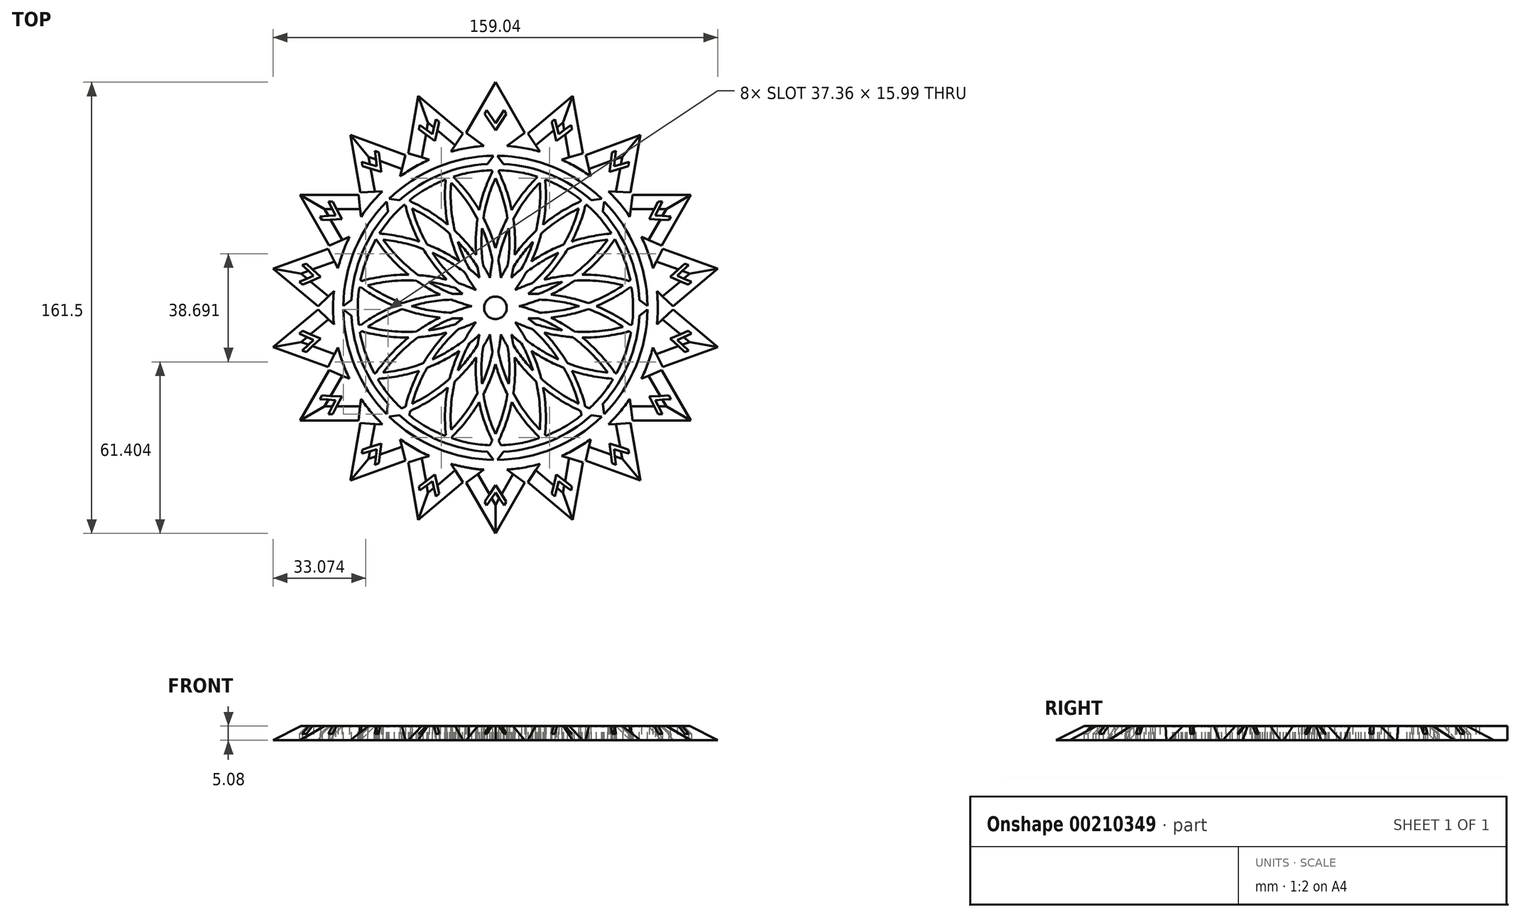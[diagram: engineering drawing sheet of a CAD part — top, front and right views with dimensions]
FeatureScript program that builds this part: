
annotation { "Feature Type Name" : "Feature", "Feature Type Description" : "" }
export const myFeature = defineFeature(function(context is Context, id is Id, definition is map)
    precondition{}
    {
        {
            var Q0;
            Q0=qCreatedBy(makeId("Top.planeOp"),FACE);
            var sketch = newSketch(context, id + "F0", { "sketchPlane" : qUnion([Q0])});
            skLineSegment(sketch, "E0", {"start": v(0, 0) * mm, "end": v(0, 63.5) * mm});
            skLineSegment(sketch, "E1", {"start": v(4.14, 57.94) * mm, "end": v(10.44, 62.64) * mm});
            skLineSegment(sketch, "E2", {"start": v(10.44, 62.64) * mm, "end": v(0, 80.75) * mm});
            skLineSegment(sketch, "E3", {"start": v(0, 80.75) * mm, "end": v(-10.44, 62.64) * mm});
            skLineSegment(sketch, "E4", {"start": v(-10.44, 62.64) * mm, "end": v(-4.14, 57.94) * mm});
            skLineSegment(sketch, "E5", {"start": v(0, 63.5) * mm, "end": v(3.84, 69.42) * mm});
            skLineSegment(sketch, "E6", {"start": v(3.08, 70.74) * mm, "end": v(0, 66.1) * mm});
            skLineSegment(sketch, "E7", {"start": v(0, 66.1) * mm, "end": v(-3.08, 70.74) * mm});
            skLineSegment(sketch, "E8", {"start": v(-3.84, 69.42) * mm, "end": v(0, 63.5) * mm});
            skLineSegment(sketch, "E9", {"start": v(0, 66.1) * mm, "end": v(0, 71.75) * mm});
            skLineSegment(sketch, "E10", {"start": v(-3.08, 70.74) * mm, "end": v(-3.84, 69.42) * mm});
            skLineSegment(sketch, "E11", {"start": v(3.08, 70.74) * mm, "end": v(3.84, 69.42) * mm});
            skLineSegment(sketch, "E12.1.0", {"start": v(31.24, 55.29) * mm, "end": v(27.62, 75.88) * mm});
            skLineSegment(sketch, "E12.1.1", {"start": v(27.62, 75.88) * mm, "end": v(11.6, 62.43) * mm});
            skLineSegment(sketch, "E12.1.2", {"start": v(22.61, 62.12) * mm, "end": v(21.3, 67.53) * mm});
            skLineSegment(sketch, "E12.1.3", {"start": v(21.3, 67.53) * mm, "end": v(20.13, 66.55) * mm});
            skLineSegment(sketch, "E12.1.4", {"start": v(20.13, 66.55) * mm, "end": v(21.72, 59.67) * mm});
            skLineSegment(sketch, "E12.1.5", {"start": v(21.72, 59.67) * mm, "end": v(27.35, 63.92) * mm});
            skLineSegment(sketch, "E12.1.6", {"start": v(27.09, 65.43) * mm, "end": v(27.35, 63.92) * mm});
            skLineSegment(sketch, "E12.1.7", {"start": v(27.09, 65.43) * mm, "end": v(22.61, 62.12) * mm});
            skLineSegment(sketch, "E12.1.10", {"start": v(11.6, 62.43) * mm, "end": v(15.93, 55.86) * mm});
            skLineSegment(sketch, "E12.1.11", {"start": v(23.7, 53.03) * mm, "end": v(31.24, 55.29) * mm});
            skLineSegment(sketch, "E12.2.0", {"start": v(48.26, 41.27) * mm, "end": v(51.9, 61.86) * mm});
            skLineSegment(sketch, "E12.2.1", {"start": v(51.9, 61.86) * mm, "end": v(32.26, 54.7) * mm});
            skLineSegment(sketch, "E12.2.2", {"start": v(42.5, 50.64) * mm, "end": v(43.12, 56.17) * mm});
            skLineSegment(sketch, "E12.2.3", {"start": v(43.12, 56.17) * mm, "end": v(41.68, 55.65) * mm});
            skLineSegment(sketch, "E12.2.4", {"start": v(41.68, 55.65) * mm, "end": v(40.82, 48.64) * mm});
            skLineSegment(sketch, "E12.2.5", {"start": v(40.82, 48.64) * mm, "end": v(47.56, 50.7) * mm});
            skLineSegment(sketch, "E12.2.6", {"start": v(47.83, 52.22) * mm, "end": v(47.56, 50.7) * mm});
            skLineSegment(sketch, "E12.2.7", {"start": v(47.83, 52.22) * mm, "end": v(42.5, 50.64) * mm});
            skLineSegment(sketch, "E12.2.10", {"start": v(32.26, 54.7) * mm, "end": v(34.07, 47.05) * mm});
            skLineSegment(sketch, "E12.2.11", {"start": v(40.41, 41.73) * mm, "end": v(48.26, 41.27) * mm});
            skLineSegment(sketch, "E12.3.0", {"start": v(59.47, 22.27) * mm, "end": v(69.93, 40.37) * mm});
            skLineSegment(sketch, "E12.3.1", {"start": v(69.93, 40.37) * mm, "end": v(49.02, 40.36) * mm});
            skLineSegment(sketch, "E12.3.2", {"start": v(57.25, 33.05) * mm, "end": v(59.73, 38.04) * mm});
            skLineSegment(sketch, "E12.3.3", {"start": v(59.73, 38.04) * mm, "end": v(58.2, 38.04) * mm});
            skLineSegment(sketch, "E12.3.4", {"start": v(58.2, 38.04) * mm, "end": v(55, 31.75) * mm});
            skLineSegment(sketch, "E12.3.5", {"start": v(55, 31.75) * mm, "end": v(62.04, 31.38) * mm});
            skLineSegment(sketch, "E12.3.6", {"start": v(62.8, 32.7) * mm, "end": v(62.04, 31.38) * mm});
            skLineSegment(sketch, "E12.3.7", {"start": v(62.8, 32.7) * mm, "end": v(57.25, 33.05) * mm});
            skLineSegment(sketch, "E12.3.10", {"start": v(49.02, 40.36) * mm, "end": v(48.1, 32.56) * mm});
            skLineSegment(sketch, "E12.3.11", {"start": v(52.25, 25.39) * mm, "end": v(59.47, 22.27) * mm});
            skLineSegment(sketch, "E12.4.0", {"start": v(63.5, 0.6) * mm, "end": v(79.52, 14.02) * mm});
            skLineSegment(sketch, "E12.4.1", {"start": v(79.52, 14.02) * mm, "end": v(59.87, 21.16) * mm});
            skLineSegment(sketch, "E12.4.2", {"start": v(65.1, 11.48) * mm, "end": v(69.14, 15.31) * mm});
            skLineSegment(sketch, "E12.4.3", {"start": v(69.14, 15.31) * mm, "end": v(67.7, 15.84) * mm});
            skLineSegment(sketch, "E12.4.4", {"start": v(67.7, 15.84) * mm, "end": v(62.54, 11.03) * mm});
            skLineSegment(sketch, "E12.4.5", {"start": v(62.54, 11.03) * mm, "end": v(69.03, 8.27) * mm});
            skLineSegment(sketch, "E12.4.6", {"start": v(70.2, 9.26) * mm, "end": v(69.03, 8.27) * mm});
            skLineSegment(sketch, "E12.4.7", {"start": v(70.2, 9.26) * mm, "end": v(65.1, 11.48) * mm});
            skLineSegment(sketch, "E12.4.10", {"start": v(59.87, 21.16) * mm, "end": v(56.34, 14.14) * mm});
            skLineSegment(sketch, "E12.4.11", {"start": v(57.78, 5.99) * mm, "end": v(63.5, 0.6) * mm});
            skLineSegment(sketch, "E12.5.0", {"start": v(59.87, -21.16) * mm, "end": v(79.52, -14.02) * mm});
            skLineSegment(sketch, "E12.5.1", {"start": v(79.52, -14.02) * mm, "end": v(63.5, -0.6) * mm});
            skLineSegment(sketch, "E12.5.2", {"start": v(65.1, -11.48) * mm, "end": v(70.2, -9.26) * mm});
            skLineSegment(sketch, "E12.5.3", {"start": v(70.2, -9.26) * mm, "end": v(69.03, -8.27) * mm});
            skLineSegment(sketch, "E12.5.4", {"start": v(69.03, -8.27) * mm, "end": v(62.54, -11.03) * mm});
            skLineSegment(sketch, "E12.5.5", {"start": v(62.54, -11.03) * mm, "end": v(67.7, -15.84) * mm});
            skLineSegment(sketch, "E12.5.6", {"start": v(69.14, -15.31) * mm, "end": v(67.7, -15.84) * mm});
            skLineSegment(sketch, "E12.5.7", {"start": v(69.14, -15.31) * mm, "end": v(65.1, -11.48) * mm});
            skLineSegment(sketch, "E12.5.10", {"start": v(63.5, -0.6) * mm, "end": v(57.78, -5.98) * mm});
            skLineSegment(sketch, "E12.5.11", {"start": v(56.34, -14.14) * mm, "end": v(59.87, -21.16) * mm});
            skLineSegment(sketch, "E12.6.0", {"start": v(49.02, -40.36) * mm, "end": v(69.93, -40.37) * mm});
            skLineSegment(sketch, "E12.6.1", {"start": v(69.93, -40.37) * mm, "end": v(59.47, -22.27) * mm});
            skLineSegment(sketch, "E12.6.2", {"start": v(57.25, -33.05) * mm, "end": v(62.8, -32.7) * mm});
            skLineSegment(sketch, "E12.6.3", {"start": v(62.8, -32.7) * mm, "end": v(62.04, -31.38) * mm});
            skLineSegment(sketch, "E12.6.4", {"start": v(62.04, -31.38) * mm, "end": v(55, -31.75) * mm});
            skLineSegment(sketch, "E12.6.5", {"start": v(55, -31.75) * mm, "end": v(58.2, -38.04) * mm});
            skLineSegment(sketch, "E12.6.6", {"start": v(59.73, -38.04) * mm, "end": v(58.2, -38.04) * mm});
            skLineSegment(sketch, "E12.6.7", {"start": v(59.73, -38.04) * mm, "end": v(57.25, -33.05) * mm});
            skLineSegment(sketch, "E12.6.10", {"start": v(59.47, -22.27) * mm, "end": v(52.25, -25.39) * mm});
            skLineSegment(sketch, "E12.6.11", {"start": v(48.1, -32.56) * mm, "end": v(49.02, -40.36) * mm});
            skLineSegment(sketch, "E12.7.0", {"start": v(32.26, -54.7) * mm, "end": v(51.9, -61.86) * mm});
            skLineSegment(sketch, "E12.7.1", {"start": v(51.9, -61.86) * mm, "end": v(48.26, -41.27) * mm});
            skLineSegment(sketch, "E12.7.2", {"start": v(42.5, -50.64) * mm, "end": v(47.83, -52.22) * mm});
            skLineSegment(sketch, "E12.7.3", {"start": v(47.83, -52.22) * mm, "end": v(47.56, -50.7) * mm});
            skLineSegment(sketch, "E12.7.4", {"start": v(47.56, -50.7) * mm, "end": v(40.82, -48.64) * mm});
            skLineSegment(sketch, "E12.7.5", {"start": v(40.82, -48.64) * mm, "end": v(41.68, -55.65) * mm});
            skLineSegment(sketch, "E12.7.6", {"start": v(43.12, -56.17) * mm, "end": v(41.68, -55.65) * mm});
            skLineSegment(sketch, "E12.7.7", {"start": v(43.12, -56.17) * mm, "end": v(42.5, -50.64) * mm});
            skLineSegment(sketch, "E12.7.10", {"start": v(48.26, -41.27) * mm, "end": v(40.42, -41.72) * mm});
            skLineSegment(sketch, "E12.7.11", {"start": v(34.07, -47.05) * mm, "end": v(32.26, -54.7) * mm});
            skLineSegment(sketch, "E12.8.0", {"start": v(11.6, -62.43) * mm, "end": v(27.62, -75.88) * mm});
            skLineSegment(sketch, "E12.8.1", {"start": v(27.62, -75.88) * mm, "end": v(31.24, -55.29) * mm});
            skLineSegment(sketch, "E12.8.2", {"start": v(22.61, -62.12) * mm, "end": v(27.09, -65.43) * mm});
            skLineSegment(sketch, "E12.8.3", {"start": v(27.09, -65.43) * mm, "end": v(27.35, -63.92) * mm});
            skLineSegment(sketch, "E12.8.4", {"start": v(27.35, -63.92) * mm, "end": v(21.72, -59.67) * mm});
            skLineSegment(sketch, "E12.8.5", {"start": v(21.72, -59.67) * mm, "end": v(20.13, -66.55) * mm});
            skLineSegment(sketch, "E12.8.6", {"start": v(21.3, -67.53) * mm, "end": v(20.13, -66.55) * mm});
            skLineSegment(sketch, "E12.8.7", {"start": v(21.3, -67.53) * mm, "end": v(22.61, -62.12) * mm});
            skLineSegment(sketch, "E12.8.10", {"start": v(31.24, -55.29) * mm, "end": v(23.7, -53.03) * mm});
            skLineSegment(sketch, "E12.8.11", {"start": v(15.93, -55.86) * mm, "end": v(11.6, -62.43) * mm});
            skLineSegment(sketch, "E12.9.0", {"start": v(-10.44, -62.64) * mm, "end": v(0, -80.75) * mm});
            skLineSegment(sketch, "E12.9.1", {"start": v(0, -80.75) * mm, "end": v(10.44, -62.64) * mm});
            skLineSegment(sketch, "E12.9.2", {"start": v(0, -66.1) * mm, "end": v(3.08, -70.74) * mm});
            skLineSegment(sketch, "E12.9.3", {"start": v(3.08, -70.74) * mm, "end": v(3.84, -69.42) * mm});
            skLineSegment(sketch, "E12.9.4", {"start": v(3.84, -69.42) * mm, "end": v(0, -63.5) * mm});
            skLineSegment(sketch, "E12.9.5", {"start": v(0, -63.5) * mm, "end": v(-3.84, -69.42) * mm});
            skLineSegment(sketch, "E12.9.6", {"start": v(-3.08, -70.74) * mm, "end": v(-3.84, -69.42) * mm});
            skLineSegment(sketch, "E12.9.7", {"start": v(-3.08, -70.74) * mm, "end": v(0, -66.1) * mm});
            skLineSegment(sketch, "E12.9.10", {"start": v(10.44, -62.64) * mm, "end": v(4.14, -57.94) * mm});
            skLineSegment(sketch, "E12.9.11", {"start": v(-4.14, -57.94) * mm, "end": v(-10.44, -62.64) * mm});
            skPoint(sketch, "E12.center", {"position": v(0, 0) * mm});
            skLineSegment(sketch, "E12.anchor1", {"start": v(0, 0) * mm, "end": v(10.44, 62.64) * mm, "construction": true});
            skLineSegment(sketch, "E12.anchor2", {"start": v(0, 0) * mm, "end": v(-10.44, -62.64) * mm, "construction": true});
            skLineSegment(sketch, "E13.1.0", {"start": v(-27.62, -75.88) * mm, "end": v(-11.6, -62.43) * mm});
            skLineSegment(sketch, "E13.1.1", {"start": v(-31.24, -55.29) * mm, "end": v(-27.62, -75.88) * mm});
            skLineSegment(sketch, "E13.1.2", {"start": v(-23.7, -53.03) * mm, "end": v(-31.24, -55.29) * mm});
            skLineSegment(sketch, "E13.1.5", {"start": v(-11.6, -62.43) * mm, "end": v(-15.93, -55.86) * mm});
            skLineSegment(sketch, "E13.1.6", {"start": v(-20.13, -66.55) * mm, "end": v(-21.72, -59.67) * mm});
            skLineSegment(sketch, "E13.1.7", {"start": v(-21.72, -59.67) * mm, "end": v(-27.35, -63.92) * mm});
            skLineSegment(sketch, "E13.1.8", {"start": v(-27.09, -65.43) * mm, "end": v(-27.35, -63.92) * mm});
            skLineSegment(sketch, "E13.1.9", {"start": v(-27.09, -65.43) * mm, "end": v(-22.61, -62.12) * mm});
            skLineSegment(sketch, "E13.1.10", {"start": v(-22.61, -62.12) * mm, "end": v(-21.3, -67.53) * mm});
            skLineSegment(sketch, "E13.1.11", {"start": v(-21.3, -67.53) * mm, "end": v(-20.13, -66.55) * mm});
            skLineSegment(sketch, "E13.2.0", {"start": v(-51.9, -61.86) * mm, "end": v(-32.26, -54.7) * mm});
            skLineSegment(sketch, "E13.2.1", {"start": v(-48.26, -41.27) * mm, "end": v(-51.9, -61.86) * mm});
            skLineSegment(sketch, "E13.2.2", {"start": v(-40.41, -41.73) * mm, "end": v(-48.26, -41.27) * mm});
            skLineSegment(sketch, "E13.2.5", {"start": v(-32.26, -54.7) * mm, "end": v(-34.07, -47.05) * mm});
            skLineSegment(sketch, "E13.2.6", {"start": v(-41.68, -55.65) * mm, "end": v(-40.82, -48.64) * mm});
            skLineSegment(sketch, "E13.2.7", {"start": v(-40.82, -48.64) * mm, "end": v(-47.56, -50.7) * mm});
            skLineSegment(sketch, "E13.2.8", {"start": v(-47.83, -52.22) * mm, "end": v(-47.56, -50.7) * mm});
            skLineSegment(sketch, "E13.2.9", {"start": v(-47.83, -52.22) * mm, "end": v(-42.5, -50.64) * mm});
            skLineSegment(sketch, "E13.2.10", {"start": v(-42.5, -50.64) * mm, "end": v(-43.12, -56.17) * mm});
            skLineSegment(sketch, "E13.2.11", {"start": v(-43.12, -56.17) * mm, "end": v(-41.68, -55.65) * mm});
            skLineSegment(sketch, "E13.3.0", {"start": v(-69.93, -40.37) * mm, "end": v(-49.02, -40.36) * mm});
            skLineSegment(sketch, "E13.3.1", {"start": v(-59.47, -22.27) * mm, "end": v(-69.93, -40.37) * mm});
            skLineSegment(sketch, "E13.3.2", {"start": v(-52.25, -25.39) * mm, "end": v(-59.47, -22.27) * mm});
            skLineSegment(sketch, "E13.3.5", {"start": v(-49.02, -40.36) * mm, "end": v(-48.1, -32.56) * mm});
            skLineSegment(sketch, "E13.3.6", {"start": v(-58.2, -38.04) * mm, "end": v(-55, -31.75) * mm});
            skLineSegment(sketch, "E13.3.7", {"start": v(-55, -31.75) * mm, "end": v(-62.04, -31.38) * mm});
            skLineSegment(sketch, "E13.3.8", {"start": v(-62.8, -32.7) * mm, "end": v(-62.04, -31.38) * mm});
            skLineSegment(sketch, "E13.3.9", {"start": v(-62.8, -32.7) * mm, "end": v(-57.25, -33.05) * mm});
            skLineSegment(sketch, "E13.3.10", {"start": v(-57.25, -33.05) * mm, "end": v(-59.73, -38.04) * mm});
            skLineSegment(sketch, "E13.3.11", {"start": v(-59.73, -38.04) * mm, "end": v(-58.2, -38.04) * mm});
            skLineSegment(sketch, "E13.4.0", {"start": v(-79.52, -14.02) * mm, "end": v(-59.87, -21.16) * mm});
            skLineSegment(sketch, "E13.4.1", {"start": v(-63.5, -0.6) * mm, "end": v(-79.52, -14.02) * mm});
            skLineSegment(sketch, "E13.4.2", {"start": v(-57.78, -5.99) * mm, "end": v(-63.5, -0.6) * mm});
            skLineSegment(sketch, "E13.4.5", {"start": v(-59.87, -21.16) * mm, "end": v(-56.34, -14.14) * mm});
            skLineSegment(sketch, "E13.4.6", {"start": v(-67.7, -15.84) * mm, "end": v(-62.54, -11.03) * mm});
            skLineSegment(sketch, "E13.4.7", {"start": v(-62.54, -11.03) * mm, "end": v(-69.03, -8.27) * mm});
            skLineSegment(sketch, "E13.4.8", {"start": v(-70.2, -9.26) * mm, "end": v(-69.03, -8.27) * mm});
            skLineSegment(sketch, "E13.4.9", {"start": v(-70.2, -9.26) * mm, "end": v(-65.1, -11.48) * mm});
            skLineSegment(sketch, "E13.4.10", {"start": v(-65.1, -11.48) * mm, "end": v(-69.14, -15.31) * mm});
            skLineSegment(sketch, "E13.4.11", {"start": v(-69.14, -15.31) * mm, "end": v(-67.7, -15.84) * mm});
            skLineSegment(sketch, "E13.5.0", {"start": v(-79.52, 14.02) * mm, "end": v(-63.5, 0.6) * mm});
            skLineSegment(sketch, "E13.5.1", {"start": v(-59.87, 21.16) * mm, "end": v(-79.52, 14.02) * mm});
            skLineSegment(sketch, "E13.5.2", {"start": v(-56.34, 14.14) * mm, "end": v(-59.87, 21.16) * mm});
            skLineSegment(sketch, "E13.5.5", {"start": v(-63.5, 0.6) * mm, "end": v(-57.78, 5.98) * mm});
            skLineSegment(sketch, "E13.5.6", {"start": v(-69.03, 8.27) * mm, "end": v(-62.54, 11.03) * mm});
            skLineSegment(sketch, "E13.5.7", {"start": v(-62.54, 11.03) * mm, "end": v(-67.7, 15.84) * mm});
            skLineSegment(sketch, "E13.5.8", {"start": v(-69.14, 15.31) * mm, "end": v(-67.7, 15.84) * mm});
            skLineSegment(sketch, "E13.5.9", {"start": v(-69.14, 15.31) * mm, "end": v(-65.1, 11.48) * mm});
            skLineSegment(sketch, "E13.5.10", {"start": v(-65.1, 11.48) * mm, "end": v(-70.2, 9.26) * mm});
            skLineSegment(sketch, "E13.5.11", {"start": v(-70.2, 9.26) * mm, "end": v(-69.03, 8.27) * mm});
            skLineSegment(sketch, "E13.6.0", {"start": v(-69.93, 40.37) * mm, "end": v(-59.47, 22.27) * mm});
            skLineSegment(sketch, "E13.6.1", {"start": v(-49.02, 40.36) * mm, "end": v(-69.93, 40.37) * mm});
            skLineSegment(sketch, "E13.6.2", {"start": v(-48.1, 32.56) * mm, "end": v(-49.02, 40.36) * mm});
            skLineSegment(sketch, "E13.6.5", {"start": v(-59.47, 22.27) * mm, "end": v(-52.25, 25.39) * mm});
            skLineSegment(sketch, "E13.6.6", {"start": v(-62.04, 31.38) * mm, "end": v(-55, 31.75) * mm});
            skLineSegment(sketch, "E13.6.7", {"start": v(-55, 31.75) * mm, "end": v(-58.2, 38.04) * mm});
            skLineSegment(sketch, "E13.6.8", {"start": v(-59.73, 38.04) * mm, "end": v(-58.2, 38.04) * mm});
            skLineSegment(sketch, "E13.6.9", {"start": v(-59.73, 38.04) * mm, "end": v(-57.25, 33.05) * mm});
            skLineSegment(sketch, "E13.6.10", {"start": v(-57.25, 33.05) * mm, "end": v(-62.8, 32.7) * mm});
            skLineSegment(sketch, "E13.6.11", {"start": v(-62.8, 32.7) * mm, "end": v(-62.04, 31.38) * mm});
            skLineSegment(sketch, "E13.7.0", {"start": v(-51.9, 61.86) * mm, "end": v(-48.26, 41.27) * mm});
            skLineSegment(sketch, "E13.7.1", {"start": v(-32.26, 54.7) * mm, "end": v(-51.9, 61.86) * mm});
            skLineSegment(sketch, "E13.7.2", {"start": v(-34.07, 47.05) * mm, "end": v(-32.26, 54.7) * mm});
            skLineSegment(sketch, "E13.7.5", {"start": v(-48.26, 41.27) * mm, "end": v(-40.42, 41.72) * mm});
            skLineSegment(sketch, "E13.7.6", {"start": v(-47.56, 50.7) * mm, "end": v(-40.82, 48.64) * mm});
            skLineSegment(sketch, "E13.7.7", {"start": v(-40.82, 48.64) * mm, "end": v(-41.68, 55.65) * mm});
            skLineSegment(sketch, "E13.7.8", {"start": v(-43.12, 56.17) * mm, "end": v(-41.68, 55.65) * mm});
            skLineSegment(sketch, "E13.7.9", {"start": v(-43.12, 56.17) * mm, "end": v(-42.5, 50.64) * mm});
            skLineSegment(sketch, "E13.7.10", {"start": v(-42.5, 50.64) * mm, "end": v(-47.83, 52.22) * mm});
            skLineSegment(sketch, "E13.7.11", {"start": v(-47.83, 52.22) * mm, "end": v(-47.56, 50.7) * mm});
            skLineSegment(sketch, "E13.8.0", {"start": v(-27.62, 75.88) * mm, "end": v(-31.24, 55.29) * mm});
            skLineSegment(sketch, "E13.8.1", {"start": v(-11.6, 62.43) * mm, "end": v(-27.62, 75.88) * mm});
            skLineSegment(sketch, "E13.8.2", {"start": v(-15.93, 55.86) * mm, "end": v(-11.6, 62.43) * mm});
            skLineSegment(sketch, "E13.8.5", {"start": v(-31.24, 55.29) * mm, "end": v(-23.7, 53.03) * mm});
            skLineSegment(sketch, "E13.8.6", {"start": v(-27.35, 63.92) * mm, "end": v(-21.72, 59.67) * mm});
            skLineSegment(sketch, "E13.8.7", {"start": v(-21.72, 59.67) * mm, "end": v(-20.13, 66.55) * mm});
            skLineSegment(sketch, "E13.8.8", {"start": v(-21.3, 67.53) * mm, "end": v(-20.13, 66.55) * mm});
            skLineSegment(sketch, "E13.8.9", {"start": v(-21.3, 67.53) * mm, "end": v(-22.61, 62.12) * mm});
            skLineSegment(sketch, "E13.8.10", {"start": v(-22.61, 62.12) * mm, "end": v(-27.09, 65.43) * mm});
            skLineSegment(sketch, "E13.8.11", {"start": v(-27.09, 65.43) * mm, "end": v(-27.35, 63.92) * mm});
            skLineSegment(sketch, "E13.anchor1", {"start": v(0, 0) * mm, "end": v(0, -80.75) * mm, "construction": true});
            skLineSegment(sketch, "E13.anchor2", {"start": v(0, 0) * mm, "end": v(0, 80.75) * mm, "construction": true});
            skArc(sketch, "E14", {"start": v(-56.34, -14.14) * mm, "mid": v(-54.59, -19.87) * mm, "end": v(-52.25, -25.39) * mm});
            skCircle(sketch, "E15", {"center": v(0, 0) * mm, "radius": 53.43 * mm});
            skArc(sketch, "E16.trimOffspring", {"start": v(10.44, -62.64) * mm, "mid": v(11.03, -62.54) * mm, "end": v(11.6, -62.43) * mm});
            skArc(sketch, "E17.trimOffspring", {"start": v(59.87, 21.16) * mm, "mid": v(59.67, 21.72) * mm, "end": v(59.47, 22.27) * mm});
            skArc(sketch, "E18.trimOffspring", {"start": v(-10.44, 62.64) * mm, "mid": v(-11.03, 62.54) * mm, "end": v(-11.6, 62.43) * mm});
            skArc(sketch, "E19.trimOffspring", {"start": v(-59.47, 22.27) * mm, "mid": v(-59.67, 21.72) * mm, "end": v(-59.87, 21.16) * mm});
            skArc(sketch, "E20.trimOffspring", {"start": v(-57.78, 5.98) * mm, "mid": v(-58.09, 0) * mm, "end": v(-57.78, -5.99) * mm});
            skArc(sketch, "E21.trimOffspring", {"start": v(-52.25, 25.39) * mm, "mid": v(-54.59, 19.87) * mm, "end": v(-56.34, 14.14) * mm});
            skArc(sketch, "E22.trimOffspring", {"start": v(-48.1, -32.56) * mm, "mid": v(-44.5, -37.34) * mm, "end": v(-40.41, -41.73) * mm});
            skArc(sketch, "E23.trimOffspring", {"start": v(-34.07, -47.05) * mm, "mid": v(-29.04, -50.3) * mm, "end": v(-23.7, -53.03) * mm});
            skArc(sketch, "E24.trimOffspring", {"start": v(-40.42, 41.72) * mm, "mid": v(-44.5, 37.34) * mm, "end": v(-48.1, 32.56) * mm});
            skArc(sketch, "E25.trimOffspring", {"start": v(-23.7, 53.03) * mm, "mid": v(-29.04, 50.3) * mm, "end": v(-34.07, 47.05) * mm});
            skArc(sketch, "E26.trimOffspring", {"start": v(-4.14, 57.94) * mm, "mid": v(-10.09, 57.2) * mm, "end": v(-15.93, 55.86) * mm});
            skArc(sketch, "E27.trimOffspring", {"start": v(15.93, 55.86) * mm, "mid": v(10.09, 57.2) * mm, "end": v(4.14, 57.94) * mm});
            skArc(sketch, "E28.trimOffspring", {"start": v(-15.93, -55.86) * mm, "mid": v(-12.76, -56.67) * mm, "end": v(-9.55, -57.3) * mm});
            skArc(sketch, "E29.trimOffspring", {"start": v(4.14, -57.94) * mm, "mid": v(10.09, -57.2) * mm, "end": v(15.93, -55.86) * mm});
            skArc(sketch, "E30.trimOffspring", {"start": v(23.7, -53.03) * mm, "mid": v(29.04, -50.3) * mm, "end": v(34.07, -47.05) * mm});
            skArc(sketch, "E31.trimOffspring", {"start": v(40.42, -41.72) * mm, "mid": v(44.5, -37.34) * mm, "end": v(48.1, -32.56) * mm});
            skArc(sketch, "E32.trimOffspring", {"start": v(52.25, -25.39) * mm, "mid": v(54.59, -19.87) * mm, "end": v(56.34, -14.14) * mm});
            skArc(sketch, "E33.trimOffspring", {"start": v(57.78, -5.98) * mm, "mid": v(58.09, 0) * mm, "end": v(57.78, 5.99) * mm});
            skArc(sketch, "E34.trimOffspring", {"start": v(56.34, 14.14) * mm, "mid": v(54.59, 19.87) * mm, "end": v(52.25, 25.39) * mm});
            skArc(sketch, "E35.trimOffspring", {"start": v(48.1, 32.56) * mm, "mid": v(44.5, 37.34) * mm, "end": v(40.41, 41.73) * mm});
            skArc(sketch, "E36.trimOffspring", {"start": v(34.07, 47.05) * mm, "mid": v(29.04, 50.3) * mm, "end": v(23.7, 53.03) * mm});
            skArc(sketch, "E37", {"start": v(-9.55, -57.3) * mm, "mid": v(-6.86, -57.72) * mm, "end": v(-4.14, -57.94) * mm});
            skSolve(sketch);
        }
        {
            var Q0;
            Q0=makeQuery(id+"F0.imprint","IMPRINT",FACE,{"disambiguationData":[TD([[makeQuery(id+"F0.imprint","IMPRINT",EDGE,{"derivedFrom":sQuery(id+"F0.wireOp",EDGE,"E12.1.0")}),1.0]])]});
            extrude(context, id + "F1", {"entities" : qUnion([Q0]), "depth" : 5.08 * mm});
        }
        {
            var Q0;
            Q0=makeQuery(id+"F1.opExtrude","CAP_EDGE",EDGE,{"disambiguationData":[OSD([sQuery(id+"F0.wireOp",EDGE,"E13.2.1")])],"isStart":false});
            var Q1;
            Q1=makeQuery(id+"F1.opExtrude","CAP_EDGE",EDGE,{"disambiguationData":[OSD([sQuery(id+"F0.wireOp",EDGE,"E13.2.0")])],"isStart":false});
            var Q2;
            Q2=makeQuery(id+"F1.opExtrude","CAP_EDGE",EDGE,{"disambiguationData":[OSD([sQuery(id+"F0.wireOp",EDGE,"E13.1.1")])],"isStart":false});
            var Q3;
            Q3=makeQuery(id+"F1.opExtrude","CAP_EDGE",EDGE,{"disambiguationData":[OSD([sQuery(id+"F0.wireOp",EDGE,"E13.1.0")])],"isStart":false});
            var Q4;
            Q4=makeQuery(id+"F1.opExtrude","CAP_EDGE",EDGE,{"disambiguationData":[OSD([sQuery(id+"F0.wireOp",EDGE,"E12.9.0")])],"isStart":false});
            var Q5;
            Q5=makeQuery(id+"F1.opExtrude","CAP_EDGE",EDGE,{"disambiguationData":[OSD([sQuery(id+"F0.wireOp",EDGE,"E12.9.1")])],"isStart":false});
            var Q6;
            Q6=makeQuery(id+"F1.opExtrude","CAP_EDGE",EDGE,{"disambiguationData":[OSD([sQuery(id+"F0.wireOp",EDGE,"E12.8.0")])],"isStart":false});
            var Q7;
            Q7=makeQuery(id+"F1.opExtrude","CAP_EDGE",EDGE,{"disambiguationData":[OSD([sQuery(id+"F0.wireOp",EDGE,"E12.8.1")])],"isStart":false});
            var Q8;
            Q8=makeQuery(id+"F1.opExtrude","CAP_EDGE",EDGE,{"disambiguationData":[OSD([sQuery(id+"F0.wireOp",EDGE,"E12.7.0")])],"isStart":false});
            var Q9;
            Q9=makeQuery(id+"F1.opExtrude","CAP_EDGE",EDGE,{"disambiguationData":[OSD([sQuery(id+"F0.wireOp",EDGE,"E12.7.1")])],"isStart":false});
            var Q10;
            Q10=makeQuery(id+"F1.opExtrude","CAP_EDGE",EDGE,{"disambiguationData":[OSD([sQuery(id+"F0.wireOp",EDGE,"E12.6.0")])],"isStart":false});
            var Q11;
            Q11=makeQuery(id+"F1.opExtrude","CAP_EDGE",EDGE,{"disambiguationData":[OSD([sQuery(id+"F0.wireOp",EDGE,"E12.6.1")])],"isStart":false});
            var Q12;
            Q12=makeQuery(id+"F1.opExtrude","CAP_EDGE",EDGE,{"disambiguationData":[OSD([sQuery(id+"F0.wireOp",EDGE,"E12.5.0")])],"isStart":false});
            var Q13;
            Q13=makeQuery(id+"F1.opExtrude","CAP_EDGE",EDGE,{"disambiguationData":[OSD([sQuery(id+"F0.wireOp",EDGE,"E12.5.1")])],"isStart":false});
            var Q14;
            Q14=makeQuery(id+"F1.opExtrude","CAP_EDGE",EDGE,{"disambiguationData":[OSD([sQuery(id+"F0.wireOp",EDGE,"E12.4.0")])],"isStart":false});
            var Q15;
            Q15=makeQuery(id+"F1.opExtrude","CAP_EDGE",EDGE,{"disambiguationData":[OSD([sQuery(id+"F0.wireOp",EDGE,"E12.4.1")])],"isStart":false});
            var Q16;
            Q16=makeQuery(id+"F1.opExtrude","CAP_EDGE",EDGE,{"disambiguationData":[OSD([sQuery(id+"F0.wireOp",EDGE,"E3")])],"isStart":false});
            var Q17;
            Q17=makeQuery(id+"F1.opExtrude","CAP_EDGE",EDGE,{"disambiguationData":[OSD([sQuery(id+"F0.wireOp",EDGE,"E13.8.1")])],"isStart":false});
            var Q18;
            Q18=makeQuery(id+"F1.opExtrude","CAP_EDGE",EDGE,{"disambiguationData":[OSD([sQuery(id+"F0.wireOp",EDGE,"E13.8.0")])],"isStart":false});
            var Q19;
            Q19=makeQuery(id+"F1.opExtrude","CAP_EDGE",EDGE,{"disambiguationData":[OSD([sQuery(id+"F0.wireOp",EDGE,"E13.7.1")])],"isStart":false});
            var Q20;
            Q20=makeQuery(id+"F1.opExtrude","CAP_EDGE",EDGE,{"disambiguationData":[OSD([sQuery(id+"F0.wireOp",EDGE,"E13.7.0")])],"isStart":false});
            var Q21;
            Q21=makeQuery(id+"F1.opExtrude","CAP_EDGE",EDGE,{"disambiguationData":[OSD([sQuery(id+"F0.wireOp",EDGE,"E13.6.1")])],"isStart":false});
            var Q22;
            Q22=makeQuery(id+"F1.opExtrude","CAP_EDGE",EDGE,{"disambiguationData":[OSD([sQuery(id+"F0.wireOp",EDGE,"E13.6.0")])],"isStart":false});
            var Q23;
            Q23=makeQuery(id+"F1.opExtrude","CAP_EDGE",EDGE,{"disambiguationData":[OSD([sQuery(id+"F0.wireOp",EDGE,"E13.5.1")])],"isStart":false});
            var Q24;
            Q24=makeQuery(id+"F1.opExtrude","CAP_EDGE",EDGE,{"disambiguationData":[OSD([sQuery(id+"F0.wireOp",EDGE,"E13.5.0")])],"isStart":false});
            var Q25;
            Q25=makeQuery(id+"F1.opExtrude","CAP_EDGE",EDGE,{"disambiguationData":[OSD([sQuery(id+"F0.wireOp",EDGE,"E13.4.1")])],"isStart":false});
            var Q26;
            Q26=makeQuery(id+"F1.opExtrude","CAP_EDGE",EDGE,{"disambiguationData":[OSD([sQuery(id+"F0.wireOp",EDGE,"E13.4.0")])],"isStart":false});
            var Q27;
            Q27=makeQuery(id+"F1.opExtrude","CAP_EDGE",EDGE,{"disambiguationData":[OSD([sQuery(id+"F0.wireOp",EDGE,"E13.3.1")])],"isStart":false});
            var Q28;
            Q28=makeQuery(id+"F1.opExtrude","CAP_EDGE",EDGE,{"disambiguationData":[OSD([sQuery(id+"F0.wireOp",EDGE,"E13.3.0")])],"isStart":false});
            var Q29;
            Q29=makeQuery(id+"F1.opExtrude","CAP_EDGE",EDGE,{"disambiguationData":[OSD([sQuery(id+"F0.wireOp",EDGE,"E2")])],"isStart":false});
            var Q30;
            Q30=makeQuery(id+"F1.opExtrude","CAP_EDGE",EDGE,{"disambiguationData":[OSD([sQuery(id+"F0.wireOp",EDGE,"E12.1.1")])],"isStart":false});
            var Q31;
            Q31=makeQuery(id+"F1.opExtrude","CAP_EDGE",EDGE,{"disambiguationData":[OSD([sQuery(id+"F0.wireOp",EDGE,"E12.1.0")])],"isStart":false});
            var Q32;
            Q32=makeQuery(id+"F1.opExtrude","CAP_EDGE",EDGE,{"disambiguationData":[OSD([sQuery(id+"F0.wireOp",EDGE,"E12.2.1")])],"isStart":false});
            var Q33;
            Q33=makeQuery(id+"F1.opExtrude","CAP_EDGE",EDGE,{"disambiguationData":[OSD([sQuery(id+"F0.wireOp",EDGE,"E12.2.0")])],"isStart":false});
            var Q34;
            Q34=makeQuery(id+"F1.opExtrude","CAP_EDGE",EDGE,{"disambiguationData":[OSD([sQuery(id+"F0.wireOp",EDGE,"E12.3.1")])],"isStart":false});
            var Q35;
            Q35=makeQuery(id+"F1.opExtrude","CAP_EDGE",EDGE,{"disambiguationData":[OSD([sQuery(id+"F0.wireOp",EDGE,"E12.3.0")])],"isStart":false});
            chamfer(context, id + "F2", {"entities" : qUnion([Q0, Q1, Q2, Q3, Q4, Q5, Q6, Q7, Q8, Q9, Q10, Q11, Q12, Q13, Q14, Q15, Q16, Q17, Q18, Q19, Q20, Q21, Q22, Q23, Q24, Q25, Q26, Q27, Q28, Q29, Q30, Q31, Q32, Q33, Q34, Q35]), "width" : 5.08 * mm, "tangentPropagation" : true});
        }
        {
            var Q0;
            Q0=makeQuery(id+"F1.opExtrude","CAP_FACE",FACE,{"disambiguationData":[OSD([sQuery(id+"F0.wireOp",EDGE,"E12.1.0"),sQuery(id+"F0.wireOp",EDGE,"E12.1.1"),sQuery(id+"F0.wireOp",EDGE,"E12.1.2"),sQuery(id+"F0.wireOp",EDGE,"E12.1.3"),sQuery(id+"F0.wireOp",EDGE,"E12.1.4"),sQuery(id+"F0.wireOp",EDGE,"E12.1.5"),sQuery(id+"F0.wireOp",EDGE,"E12.1.6"),sQuery(id+"F0.wireOp",EDGE,"E12.1.7"),sQuery(id+"F0.wireOp",EDGE,"E12.1.10"),sQuery(id+"F0.wireOp",EDGE,"E12.1.11"),sQuery(id+"F0.wireOp",EDGE,"E12.2.0"),sQuery(id+"F0.wireOp",EDGE,"E12.2.1"),sQuery(id+"F0.wireOp",EDGE,"E12.2.2"),sQuery(id+"F0.wireOp",EDGE,"E12.2.3"),sQuery(id+"F0.wireOp",EDGE,"E12.2.4"),sQuery(id+"F0.wireOp",EDGE,"E12.2.5"),sQuery(id+"F0.wireOp",EDGE,"E12.2.6"),sQuery(id+"F0.wireOp",EDGE,"E12.2.7"),sQuery(id+"F0.wireOp",EDGE,"E12.2.10"),sQuery(id+"F0.wireOp",EDGE,"E12.2.11"),sQuery(id+"F0.wireOp",EDGE,"E12.3.0"),sQuery(id+"F0.wireOp",EDGE,"E12.3.1"),sQuery(id+"F0.wireOp",EDGE,"E12.3.2"),sQuery(id+"F0.wireOp",EDGE,"E12.3.3"),sQuery(id+"F0.wireOp",EDGE,"E12.3.4"),sQuery(id+"F0.wireOp",EDGE,"E12.3.5"),sQuery(id+"F0.wireOp",EDGE,"E12.3.6"),sQuery(id+"F0.wireOp",EDGE,"E12.3.7"),sQuery(id+"F0.wireOp",EDGE,"E12.3.10"),sQuery(id+"F0.wireOp",EDGE,"E12.3.11"),sQuery(id+"F0.wireOp",EDGE,"E12.4.0"),sQuery(id+"F0.wireOp",EDGE,"E12.4.1"),sQuery(id+"F0.wireOp",EDGE,"E12.4.2"),sQuery(id+"F0.wireOp",EDGE,"E12.4.3"),sQuery(id+"F0.wireOp",EDGE,"E12.4.4"),sQuery(id+"F0.wireOp",EDGE,"E12.4.5"),sQuery(id+"F0.wireOp",EDGE,"E12.4.6"),sQuery(id+"F0.wireOp",EDGE,"E12.4.7"),sQuery(id+"F0.wireOp",EDGE,"E12.4.10"),sQuery(id+"F0.wireOp",EDGE,"E12.4.11"),sQuery(id+"F0.wireOp",EDGE,"E12.5.0"),sQuery(id+"F0.wireOp",EDGE,"E12.5.1"),sQuery(id+"F0.wireOp",EDGE,"E12.5.2"),sQuery(id+"F0.wireOp",EDGE,"E12.5.3"),sQuery(id+"F0.wireOp",EDGE,"E12.5.4"),sQuery(id+"F0.wireOp",EDGE,"E12.5.5"),sQuery(id+"F0.wireOp",EDGE,"E12.5.6"),sQuery(id+"F0.wireOp",EDGE,"E12.5.7"),sQuery(id+"F0.wireOp",EDGE,"E12.5.10"),sQuery(id+"F0.wireOp",EDGE,"E12.5.11"),sQuery(id+"F0.wireOp",EDGE,"E12.6.0"),sQuery(id+"F0.wireOp",EDGE,"E12.6.1"),sQuery(id+"F0.wireOp",EDGE,"E12.6.2"),sQuery(id+"F0.wireOp",EDGE,"E12.6.3"),sQuery(id+"F0.wireOp",EDGE,"E12.6.4"),sQuery(id+"F0.wireOp",EDGE,"E12.6.5"),sQuery(id+"F0.wireOp",EDGE,"E12.6.6"),sQuery(id+"F0.wireOp",EDGE,"E12.6.7"),sQuery(id+"F0.wireOp",EDGE,"E12.6.10"),sQuery(id+"F0.wireOp",EDGE,"E12.6.11"),sQuery(id+"F0.wireOp",EDGE,"E12.7.0"),sQuery(id+"F0.wireOp",EDGE,"E12.7.1"),sQuery(id+"F0.wireOp",EDGE,"E12.7.2"),sQuery(id+"F0.wireOp",EDGE,"E12.7.3"),sQuery(id+"F0.wireOp",EDGE,"E12.7.4"),sQuery(id+"F0.wireOp",EDGE,"E12.7.5"),sQuery(id+"F0.wireOp",EDGE,"E12.7.6"),sQuery(id+"F0.wireOp",EDGE,"E12.7.7"),sQuery(id+"F0.wireOp",EDGE,"E12.7.10"),sQuery(id+"F0.wireOp",EDGE,"E12.7.11"),sQuery(id+"F0.wireOp",EDGE,"E12.8.0"),sQuery(id+"F0.wireOp",EDGE,"E12.8.1"),sQuery(id+"F0.wireOp",EDGE,"E12.8.2"),sQuery(id+"F0.wireOp",EDGE,"E12.8.3"),sQuery(id+"F0.wireOp",EDGE,"E12.8.4"),sQuery(id+"F0.wireOp",EDGE,"E12.8.5"),sQuery(id+"F0.wireOp",EDGE,"E12.8.6"),sQuery(id+"F0.wireOp",EDGE,"E12.8.7"),sQuery(id+"F0.wireOp",EDGE,"E12.8.10"),sQuery(id+"F0.wireOp",EDGE,"E12.8.11"),sQuery(id+"F0.wireOp",EDGE,"E12.9.0"),sQuery(id+"F0.wireOp",EDGE,"E12.9.1"),sQuery(id+"F0.wireOp",EDGE,"E12.9.2"),sQuery(id+"F0.wireOp",EDGE,"E12.9.3"),sQuery(id+"F0.wireOp",EDGE,"E12.9.4"),sQuery(id+"F0.wireOp",EDGE,"E12.9.5"),sQuery(id+"F0.wireOp",EDGE,"E12.9.6"),sQuery(id+"F0.wireOp",EDGE,"E12.9.7"),sQuery(id+"F0.wireOp",EDGE,"E12.9.10"),sQuery(id+"F0.wireOp",EDGE,"E12.9.11"),sQuery(id+"F0.wireOp",EDGE,"E13.1.0"),sQuery(id+"F0.wireOp",EDGE,"E13.1.1"),sQuery(id+"F0.wireOp",EDGE,"E13.1.2"),sQuery(id+"F0.wireOp",EDGE,"E13.1.5"),sQuery(id+"F0.wireOp",EDGE,"E13.1.6"),sQuery(id+"F0.wireOp",EDGE,"E13.1.7"),sQuery(id+"F0.wireOp",EDGE,"E13.1.8"),sQuery(id+"F0.wireOp",EDGE,"E13.1.9"),sQuery(id+"F0.wireOp",EDGE,"E13.1.10"),sQuery(id+"F0.wireOp",EDGE,"E13.1.11"),sQuery(id+"F0.wireOp",EDGE,"E13.2.0"),sQuery(id+"F0.wireOp",EDGE,"E13.2.1"),sQuery(id+"F0.wireOp",EDGE,"E13.2.2"),sQuery(id+"F0.wireOp",EDGE,"E13.2.5"),sQuery(id+"F0.wireOp",EDGE,"E13.2.6"),sQuery(id+"F0.wireOp",EDGE,"E13.2.7"),sQuery(id+"F0.wireOp",EDGE,"E13.2.8"),sQuery(id+"F0.wireOp",EDGE,"E13.2.9"),sQuery(id+"F0.wireOp",EDGE,"E13.2.10"),sQuery(id+"F0.wireOp",EDGE,"E13.2.11"),sQuery(id+"F0.wireOp",EDGE,"E13.3.0"),sQuery(id+"F0.wireOp",EDGE,"E13.3.1"),sQuery(id+"F0.wireOp",EDGE,"E13.3.2"),sQuery(id+"F0.wireOp",EDGE,"E13.3.5"),sQuery(id+"F0.wireOp",EDGE,"E13.3.6"),sQuery(id+"F0.wireOp",EDGE,"E13.3.7"),sQuery(id+"F0.wireOp",EDGE,"E13.3.8"),sQuery(id+"F0.wireOp",EDGE,"E13.3.9"),sQuery(id+"F0.wireOp",EDGE,"E13.3.10"),sQuery(id+"F0.wireOp",EDGE,"E13.3.11"),sQuery(id+"F0.wireOp",EDGE,"E13.4.0"),sQuery(id+"F0.wireOp",EDGE,"E13.4.1"),sQuery(id+"F0.wireOp",EDGE,"E13.4.2"),sQuery(id+"F0.wireOp",EDGE,"E13.4.5"),sQuery(id+"F0.wireOp",EDGE,"E13.4.6"),sQuery(id+"F0.wireOp",EDGE,"E13.4.7"),sQuery(id+"F0.wireOp",EDGE,"E13.4.8"),sQuery(id+"F0.wireOp",EDGE,"E13.4.9"),sQuery(id+"F0.wireOp",EDGE,"E13.4.10"),sQuery(id+"F0.wireOp",EDGE,"E13.4.11"),sQuery(id+"F0.wireOp",EDGE,"E13.5.0"),sQuery(id+"F0.wireOp",EDGE,"E13.5.1"),sQuery(id+"F0.wireOp",EDGE,"E13.5.2"),sQuery(id+"F0.wireOp",EDGE,"E13.5.5"),sQuery(id+"F0.wireOp",EDGE,"E13.5.6"),sQuery(id+"F0.wireOp",EDGE,"E13.5.7"),sQuery(id+"F0.wireOp",EDGE,"E13.5.8"),sQuery(id+"F0.wireOp",EDGE,"E13.5.9"),sQuery(id+"F0.wireOp",EDGE,"E13.5.10"),sQuery(id+"F0.wireOp",EDGE,"E13.5.11"),sQuery(id+"F0.wireOp",EDGE,"E13.6.0"),sQuery(id+"F0.wireOp",EDGE,"E13.6.1"),sQuery(id+"F0.wireOp",EDGE,"E13.6.2"),sQuery(id+"F0.wireOp",EDGE,"E13.6.5"),sQuery(id+"F0.wireOp",EDGE,"E13.6.6"),sQuery(id+"F0.wireOp",EDGE,"E13.6.7"),sQuery(id+"F0.wireOp",EDGE,"E13.6.8"),sQuery(id+"F0.wireOp",EDGE,"E13.6.9"),sQuery(id+"F0.wireOp",EDGE,"E13.6.10"),sQuery(id+"F0.wireOp",EDGE,"E13.6.11"),sQuery(id+"F0.wireOp",EDGE,"E13.7.0"),sQuery(id+"F0.wireOp",EDGE,"E13.7.1"),sQuery(id+"F0.wireOp",EDGE,"E13.7.2"),sQuery(id+"F0.wireOp",EDGE,"E13.7.5"),sQuery(id+"F0.wireOp",EDGE,"E13.7.6"),sQuery(id+"F0.wireOp",EDGE,"E13.7.7"),sQuery(id+"F0.wireOp",EDGE,"E13.7.8"),sQuery(id+"F0.wireOp",EDGE,"E13.7.9"),sQuery(id+"F0.wireOp",EDGE,"E13.7.10"),sQuery(id+"F0.wireOp",EDGE,"E13.7.11"),sQuery(id+"F0.wireOp",EDGE,"E13.8.0"),sQuery(id+"F0.wireOp",EDGE,"E13.8.1"),sQuery(id+"F0.wireOp",EDGE,"E13.8.2"),sQuery(id+"F0.wireOp",EDGE,"E13.8.5"),sQuery(id+"F0.wireOp",EDGE,"E13.8.6"),sQuery(id+"F0.wireOp",EDGE,"E13.8.7"),sQuery(id+"F0.wireOp",EDGE,"E13.8.8"),sQuery(id+"F0.wireOp",EDGE,"E13.8.9"),sQuery(id+"F0.wireOp",EDGE,"E13.8.10"),sQuery(id+"F0.wireOp",EDGE,"E13.8.11"),sQuery(id+"F0.wireOp",EDGE,"E3"),sQuery(id+"F0.wireOp",EDGE,"E2"),sQuery(id+"F0.wireOp",EDGE,"E1"),sQuery(id+"F0.wireOp",EDGE,"E4"),sQuery(id+"F0.wireOp",EDGE,"E8"),sQuery(id+"F0.wireOp",EDGE,"E5"),sQuery(id+"F0.wireOp",EDGE,"E11"),sQuery(id+"F0.wireOp",EDGE,"E6"),sQuery(id+"F0.wireOp",EDGE,"E7"),sQuery(id+"F0.wireOp",EDGE,"E10"),sQuery(id+"F0.wireOp",EDGE,"E14"),sQuery(id+"F0.wireOp",EDGE,"E15"),sQuery(id+"F0.wireOp",EDGE,"E20.trimOffspring"),sQuery(id+"F0.wireOp",EDGE,"E21.trimOffspring"),sQuery(id+"F0.wireOp",EDGE,"E22.trimOffspring"),sQuery(id+"F0.wireOp",EDGE,"E23.trimOffspring"),sQuery(id+"F0.wireOp",EDGE,"E24.trimOffspring"),sQuery(id+"F0.wireOp",EDGE,"E25.trimOffspring"),sQuery(id+"F0.wireOp",EDGE,"E26.trimOffspring"),sQuery(id+"F0.wireOp",EDGE,"E27.trimOffspring"),sQuery(id+"F0.wireOp",EDGE,"E28.trimOffspring"),sQuery(id+"F0.wireOp",EDGE,"E29.trimOffspring"),sQuery(id+"F0.wireOp",EDGE,"E30.trimOffspring"),sQuery(id+"F0.wireOp",EDGE,"E31.trimOffspring"),sQuery(id+"F0.wireOp",EDGE,"E32.trimOffspring"),sQuery(id+"F0.wireOp",EDGE,"E33.trimOffspring"),sQuery(id+"F0.wireOp",EDGE,"E34.trimOffspring"),sQuery(id+"F0.wireOp",EDGE,"E35.trimOffspring"),sQuery(id+"F0.wireOp",EDGE,"E36.trimOffspring"),sQuery(id+"F0.wireOp",EDGE,"E37")])],"isStart":true});
            var sketch = newSketch(context, id + "F3", { "sketchPlane" : qUnion([Q0])});
            skCircle(sketch, "E38", {"center": v(0, 0) * mm, "radius": 53.54 * mm});
            skLineSegment(sketch, "E39", {"start": v(0, 0) * mm, "end": v(0, -53.43) * mm});
            skLineSegment(sketch, "E40", {"start": v(0, -53.43) * mm, "end": v(3.81, -53.43) * mm});
            skLineSegment(sketch, "E41", {"start": v(0, -53.43) * mm, "end": v(-3.8, -53.43) * mm});
            skArc(sketch, "E42", {"start": v(-3.8, -53.43) * mm, "mid": v(-2.42, -51.12) * mm, "end": v(-1.14, -48.75) * mm});
            skArc(sketch, "E43.0", {"start": v(-2.1, -54.52) * mm, "mid": v(-1.02, -52.76) * mm, "end": v(0, -50.96) * mm});
            skLineSegment(sketch, "E44", {"start": v(-2.1, -54.52) * mm, "end": v(-3.8, -53.43) * mm});
            skLineSegment(sketch, "E45", {"start": v(2.1, -54.52) * mm, "end": v(3.81, -53.43) * mm});
            skArc(sketch, "E46.trimOffspring", {"start": v(0, -46.4) * mm, "mid": v(4.44, -31.13) * mm, "end": v(4.44, -15.23) * mm});
            skArc(sketch, "E47.trimOffspring", {"start": v(1.14, -48.75) * mm, "mid": v(2.42, -51.12) * mm, "end": v(3.81, -53.43) * mm});
            skArc(sketch, "E48.trimOffspring", {"start": v(1.14, -48.75) * mm, "mid": v(5.99, -34.21) * mm, "end": v(6.88, -18.9) * mm});
            skArc(sketch, "E49.trimOffspring", {"start": v(0, -50.96) * mm, "mid": v(1.02, -52.76) * mm, "end": v(2.1, -54.52) * mm});
            skArc(sketch, "E50.1.0", {"start": v(32.2, -36.62) * mm, "mid": v(26.58, -22.36) * mm, "end": v(17.42, -10.06) * mm});
            skArc(sketch, "E50.1.1", {"start": v(29.82, -35.54) * mm, "mid": v(23.42, -21) * mm, "end": v(13.2, -8.82) * mm});
            skArc(sketch, "E50.1.5", {"start": v(32.2, -36.62) * mm, "mid": v(34.71, -37.6) * mm, "end": v(37.26, -38.48) * mm});
            skArc(sketch, "E50.1.6", {"start": v(32.76, -39.04) * mm, "mid": v(34.7, -39.76) * mm, "end": v(36.65, -40.42) * mm});
            skLineSegment(sketch, "E50.1.7", {"start": v(36.65, -40.42) * mm, "end": v(37.26, -38.48) * mm});
            skArc(sketch, "E50.1.8", {"start": v(33.44, -43.11) * mm, "mid": v(33.13, -41.07) * mm, "end": v(32.76, -39.04) * mm});
            skLineSegment(sketch, "E50.1.9", {"start": v(33.44, -43.11) * mm, "end": v(31.42, -43.38) * mm});
            skArc(sketch, "E50.1.10", {"start": v(31.42, -43.38) * mm, "mid": v(31.01, -40.72) * mm, "end": v(30.47, -38.08) * mm});
            skArc(sketch, "E50.2.0", {"start": v(48.21, -7.35) * mm, "mid": v(34.73, -0.04) * mm, "end": v(19.81, 3.5) * mm});
            skArc(sketch, "E50.2.1", {"start": v(45.69, -8.06) * mm, "mid": v(31.43, -1.03) * mm, "end": v(15.77, 1.73) * mm});
            skArc(sketch, "E50.2.5", {"start": v(48.21, -7.35) * mm, "mid": v(50.77, -6.5) * mm, "end": v(53.28, -5.53) * mm});
            skArc(sketch, "E50.2.6", {"start": v(50.19, -8.85) * mm, "mid": v(52.13, -8.16) * mm, "end": v(54.06, -7.4) * mm});
            skLineSegment(sketch, "E50.2.7", {"start": v(54.06, -7.4) * mm, "end": v(53.28, -5.53) * mm});
            skArc(sketch, "E50.2.8", {"start": v(53.33, -11.53) * mm, "mid": v(51.78, -10.16) * mm, "end": v(50.19, -8.85) * mm});
            skLineSegment(sketch, "E50.2.9", {"start": v(53.33, -11.53) * mm, "end": v(51.96, -13.03) * mm});
            skArc(sketch, "E50.2.10", {"start": v(51.96, -13.03) * mm, "mid": v(49.93, -11.26) * mm, "end": v(47.82, -9.58) * mm});
            skArc(sketch, "E50.3.0", {"start": v(41.65, 25.36) * mm, "mid": v(26.63, 22.3) * mm, "end": v(12.93, 15.41) * mm});
            skArc(sketch, "E50.3.1", {"start": v(40.18, 23.2) * mm, "mid": v(24.74, 19.41) * mm, "end": v(10.97, 11.46) * mm});
            skArc(sketch, "E50.3.5", {"start": v(41.65, 25.36) * mm, "mid": v(43.07, 27.65) * mm, "end": v(44.37, 30.01) * mm});
            skArc(sketch, "E50.3.6", {"start": v(44.13, 25.48) * mm, "mid": v(45.18, 27.26) * mm, "end": v(46.17, 29.08) * mm});
            skLineSegment(sketch, "E50.3.7", {"start": v(46.17, 29.08) * mm, "end": v(44.37, 30.01) * mm});
            skArc(sketch, "E50.3.8", {"start": v(48.27, 25.44) * mm, "mid": v(46.2, 25.5) * mm, "end": v(44.13, 25.48) * mm});
            skLineSegment(sketch, "E50.3.9", {"start": v(48.27, 25.44) * mm, "end": v(48.18, 23.41) * mm});
            skArc(sketch, "E50.3.10", {"start": v(48.18, 23.41) * mm, "mid": v(45.48, 23.47) * mm, "end": v(42.79, 23.4) * mm});
            skArc(sketch, "E50.4.0", {"start": v(15.6, 46.2) * mm, "mid": v(6.07, 34.2) * mm, "end": v(0, 20.12) * mm});
            skArc(sketch, "E50.4.1", {"start": v(15.87, 43.6) * mm, "mid": v(6.47, 30.77) * mm, "end": v(1.04, 15.83) * mm});
            skArc(sketch, "E50.4.5", {"start": v(15.6, 46.2) * mm, "mid": v(15.21, 48.87) * mm, "end": v(14.7, 51.5) * mm});
            skArc(sketch, "E50.4.6", {"start": v(17.43, 47.89) * mm, "mid": v(17.09, 49.93) * mm, "end": v(16.68, 51.95) * mm});
            skLineSegment(sketch, "E50.4.7", {"start": v(16.68, 51.95) * mm, "end": v(14.7, 51.5) * mm});
            skArc(sketch, "E50.4.8", {"start": v(20.62, 50.52) * mm, "mid": v(19, 49.23) * mm, "end": v(17.43, 47.89) * mm});
            skLineSegment(sketch, "E50.4.9", {"start": v(20.62, 50.52) * mm, "end": v(21.85, 48.9) * mm});
            skArc(sketch, "E50.4.10", {"start": v(21.85, 48.9) * mm, "mid": v(19.76, 47.21) * mm, "end": v(17.74, 45.43) * mm});
            skArc(sketch, "E50.5.0", {"start": v(-17.74, 45.43) * mm, "mid": v(-17.33, 30.1) * mm, "end": v(-12.93, 15.41) * mm});
            skArc(sketch, "E50.5.1", {"start": v(-15.87, 43.6) * mm, "mid": v(-14.82, 27.73) * mm, "end": v(-9.38, 12.8) * mm});
            skArc(sketch, "E50.5.5", {"start": v(-17.74, 45.43) * mm, "mid": v(-19.76, 47.21) * mm, "end": v(-21.85, 48.9) * mm});
            skArc(sketch, "E50.5.6", {"start": v(-17.43, 47.89) * mm, "mid": v(-19, 49.23) * mm, "end": v(-20.62, 50.52) * mm});
            skLineSegment(sketch, "E50.5.7", {"start": v(-20.62, 50.52) * mm, "end": v(-21.85, 48.9) * mm});
            skArc(sketch, "E50.5.8", {"start": v(-16.68, 51.95) * mm, "mid": v(-17.09, 49.93) * mm, "end": v(-17.43, 47.89) * mm});
            skLineSegment(sketch, "E50.5.9", {"start": v(-16.68, 51.95) * mm, "end": v(-14.7, 51.5) * mm});
            skArc(sketch, "E50.5.10", {"start": v(-14.7, 51.5) * mm, "mid": v(-15.21, 48.87) * mm, "end": v(-15.6, 46.2) * mm});
            skArc(sketch, "E50.6.0", {"start": v(-42.79, 23.4) * mm, "mid": v(-32.62, 11.92) * mm, "end": v(-19.81, 3.5) * mm});
            skArc(sketch, "E50.6.1", {"start": v(-40.18, 23.2) * mm, "mid": v(-29.18, 11.72) * mm, "end": v(-15.41, 3.77) * mm});
            skArc(sketch, "E50.6.5", {"start": v(-42.79, 23.4) * mm, "mid": v(-45.48, 23.47) * mm, "end": v(-48.18, 23.41) * mm});
            skArc(sketch, "E50.6.6", {"start": v(-44.13, 25.48) * mm, "mid": v(-46.2, 25.5) * mm, "end": v(-48.27, 25.44) * mm});
            skLineSegment(sketch, "E50.6.7", {"start": v(-48.27, 25.44) * mm, "end": v(-48.18, 23.41) * mm});
            skArc(sketch, "E50.6.8", {"start": v(-46.17, 29.08) * mm, "mid": v(-45.18, 27.26) * mm, "end": v(-44.13, 25.48) * mm});
            skLineSegment(sketch, "E50.6.9", {"start": v(-46.17, 29.08) * mm, "end": v(-44.37, 30.01) * mm});
            skArc(sketch, "E50.6.10", {"start": v(-44.37, 30.01) * mm, "mid": v(-43.07, 27.65) * mm, "end": v(-41.65, 25.36) * mm});
            skArc(sketch, "E50.7.0", {"start": v(-47.82, -9.58) * mm, "mid": v(-32.65, -11.84) * mm, "end": v(-17.42, -10.06) * mm});
            skArc(sketch, "E50.7.1", {"start": v(-45.69, -8.06) * mm, "mid": v(-29.89, -9.78) * mm, "end": v(-14.23, -7.02) * mm});
            skArc(sketch, "E50.7.5", {"start": v(-47.82, -9.58) * mm, "mid": v(-49.93, -11.26) * mm, "end": v(-51.96, -13.03) * mm});
            skArc(sketch, "E50.7.6", {"start": v(-50.19, -8.85) * mm, "mid": v(-51.78, -10.16) * mm, "end": v(-53.33, -11.53) * mm});
            skLineSegment(sketch, "E50.7.7", {"start": v(-53.33, -11.53) * mm, "end": v(-51.96, -13.03) * mm});
            skArc(sketch, "E50.7.8", {"start": v(-54.06, -7.4) * mm, "mid": v(-52.13, -8.16) * mm, "end": v(-50.19, -8.85) * mm});
            skLineSegment(sketch, "E50.7.9", {"start": v(-54.06, -7.4) * mm, "end": v(-53.28, -5.53) * mm});
            skArc(sketch, "E50.7.10", {"start": v(-53.28, -5.53) * mm, "mid": v(-50.77, -6.5) * mm, "end": v(-48.21, -7.35) * mm});
            skArc(sketch, "E50.8.0", {"start": v(-30.47, -38.08) * mm, "mid": v(-17.4, -30.06) * mm, "end": v(-6.88, -18.9) * mm});
            skArc(sketch, "E50.8.1", {"start": v(-29.82, -35.54) * mm, "mid": v(-16.6, -26.7) * mm, "end": v(-6.4, -14.52) * mm});
            skArc(sketch, "E50.8.5", {"start": v(-30.47, -38.08) * mm, "mid": v(-31.01, -40.72) * mm, "end": v(-31.42, -43.38) * mm});
            skArc(sketch, "E50.8.6", {"start": v(-32.76, -39.04) * mm, "mid": v(-33.13, -41.07) * mm, "end": v(-33.44, -43.11) * mm});
            skLineSegment(sketch, "E50.8.7", {"start": v(-33.44, -43.11) * mm, "end": v(-31.42, -43.38) * mm});
            skArc(sketch, "E50.8.8", {"start": v(-36.65, -40.42) * mm, "mid": v(-34.7, -39.76) * mm, "end": v(-32.76, -39.04) * mm});
            skLineSegment(sketch, "E50.8.9", {"start": v(-36.65, -40.42) * mm, "end": v(-37.26, -38.48) * mm});
            skArc(sketch, "E50.8.10", {"start": v(-37.26, -38.48) * mm, "mid": v(-34.71, -37.6) * mm, "end": v(-32.2, -36.62) * mm});
            skArc(sketch, "E51.trimOffspring", {"start": v(-17.42, -10.06) * mm, "mid": v(-26.58, -22.36) * mm, "end": v(-32.2, -36.62) * mm});
            skArc(sketch, "E52.trimOffspring", {"start": v(-13.2, -8.82) * mm, "mid": v(-8.55, -7.03) * mm, "end": v(-4.08, -4.86) * mm});
            skArc(sketch, "E53.trimOffspring", {"start": v(-13.2, -8.82) * mm, "mid": v(-23.42, -21) * mm, "end": v(-29.82, -35.54) * mm});
            skArc(sketch, "E54.trimOffspring", {"start": v(-15.77, 1.73) * mm, "mid": v(-11.07, 0.1) * mm, "end": v(-6.25, -1.1) * mm});
            skArc(sketch, "E55.trimOffspring", {"start": v(-19.81, 3.5) * mm, "mid": v(-34.73, -0.04) * mm, "end": v(-48.21, -7.35) * mm});
            skArc(sketch, "E56.trimOffspring", {"start": v(-15.77, 1.73) * mm, "mid": v(-31.43, -1.03) * mm, "end": v(-45.69, -8.06) * mm});
            skArc(sketch, "E57.trimOffspring", {"start": v(-10.97, 11.46) * mm, "mid": v(-24.74, 19.41) * mm, "end": v(-40.18, 23.2) * mm});
            skArc(sketch, "E58.trimOffspring", {"start": v(-12.93, 15.41) * mm, "mid": v(-26.63, 22.3) * mm, "end": v(-41.65, 25.36) * mm});
            skArc(sketch, "E59.trimOffspring", {"start": v(-10.97, 11.46) * mm, "mid": v(-8.41, 7.2) * mm, "end": v(-5.5, 3.17) * mm});
            skArc(sketch, "E60.trimOffspring", {"start": v(-1.04, 15.83) * mm, "mid": v(-6.47, 30.77) * mm, "end": v(-15.87, 43.6) * mm});
            skArc(sketch, "E61.trimOffspring", {"start": v(-1.04, 15.83) * mm, "mid": v(-1.81, 10.92) * mm, "end": v(-2.17, 5.96) * mm});
            skArc(sketch, "E62.trimOffspring", {"start": v(0, 20.12) * mm, "mid": v(-6.07, 34.2) * mm, "end": v(-15.6, 46.2) * mm});
            skArc(sketch, "E63.trimOffspring", {"start": v(9.38, 12.8) * mm, "mid": v(14.82, 27.73) * mm, "end": v(15.87, 43.6) * mm});
            skArc(sketch, "E64.trimOffspring", {"start": v(9.38, 12.8) * mm, "mid": v(5.63, 9.53) * mm, "end": v(2.17, 5.96) * mm});
            skArc(sketch, "E65.trimOffspring", {"start": v(12.93, 15.41) * mm, "mid": v(17.33, 30.1) * mm, "end": v(17.74, 45.43) * mm});
            skArc(sketch, "E66.trimOffspring", {"start": v(19.81, 3.5) * mm, "mid": v(32.62, 11.92) * mm, "end": v(42.79, 23.4) * mm});
            skArc(sketch, "E67.trimOffspring", {"start": v(15.41, 3.77) * mm, "mid": v(10.44, 3.68) * mm, "end": v(5.5, 3.17) * mm});
            skArc(sketch, "E68.trimOffspring", {"start": v(15.41, 3.77) * mm, "mid": v(29.18, 11.72) * mm, "end": v(40.18, 23.2) * mm});
            skArc(sketch, "E69.trimOffspring", {"start": v(14.23, -7.02) * mm, "mid": v(29.89, -9.78) * mm, "end": v(45.69, -8.06) * mm});
            skArc(sketch, "E70.trimOffspring", {"start": v(17.42, -10.06) * mm, "mid": v(32.65, -11.84) * mm, "end": v(47.82, -9.58) * mm});
            skArc(sketch, "E71.trimOffspring", {"start": v(14.23, -7.02) * mm, "mid": v(10.37, -3.89) * mm, "end": v(6.25, -1.1) * mm});
            skArc(sketch, "E72.trimOffspring", {"start": v(6.88, -18.9) * mm, "mid": v(17.4, -30.06) * mm, "end": v(30.47, -38.08) * mm});
            skArc(sketch, "E73.trimOffspring", {"start": v(6.4, -14.52) * mm, "mid": v(5.44, -9.64) * mm, "end": v(4.08, -4.86) * mm});
            skArc(sketch, "E74.trimOffspring", {"start": v(6.4, -14.52) * mm, "mid": v(16.6, -26.7) * mm, "end": v(29.82, -35.54) * mm});
            skArc(sketch, "E75.trimOffspring", {"start": v(-4.44, -15.23) * mm, "mid": v(-4.44, -31.13) * mm, "end": v(0, -46.4) * mm});
            skArc(sketch, "E76.trimOffspring", {"start": v(-4.44, -15.23) * mm, "mid": v(-2.03, -10.88) * mm, "end": v(0, -6.35) * mm});
            skArc(sketch, "E77.trimOffspring", {"start": v(-6.88, -18.9) * mm, "mid": v(-5.99, -34.21) * mm, "end": v(-1.14, -48.75) * mm});
            skArc(sketch, "E78.trimOffspring", {"start": v(-6.25, -1.1) * mm, "mid": v(-10.37, -3.89) * mm, "end": v(-14.23, -7.02) * mm});
            skArc(sketch, "E79.trimOffspring", {"start": v(-4.08, -4.86) * mm, "mid": v(-5.44, -9.64) * mm, "end": v(-6.4, -14.52) * mm});
            skArc(sketch, "E80.trimOffspring", {"start": v(0, -6.35) * mm, "mid": v(2.03, -10.88) * mm, "end": v(4.44, -15.23) * mm});
            skArc(sketch, "E81.trimOffspring", {"start": v(4.08, -4.86) * mm, "mid": v(8.55, -7.03) * mm, "end": v(13.2, -8.82) * mm});
            skArc(sketch, "E82.trimOffspring", {"start": v(6.25, -1.1) * mm, "mid": v(11.07, 0.1) * mm, "end": v(15.77, 1.73) * mm});
            skArc(sketch, "E83.trimOffspring", {"start": v(5.5, 3.17) * mm, "mid": v(8.41, 7.2) * mm, "end": v(10.97, 11.46) * mm});
            skArc(sketch, "E84.trimOffspring", {"start": v(2.17, 5.96) * mm, "mid": v(1.81, 10.92) * mm, "end": v(1.04, 15.83) * mm});
            skArc(sketch, "E85.trimOffspring", {"start": v(-2.17, 5.96) * mm, "mid": v(-5.63, 9.53) * mm, "end": v(-9.38, 12.8) * mm});
            skArc(sketch, "E86.trimOffspring", {"start": v(-5.5, 3.17) * mm, "mid": v(-10.44, 3.68) * mm, "end": v(-15.41, 3.77) * mm});
            skSolve(sketch);
        }
        {
            var Q0;
            Q0=makeQuery(id+"F3.imprint","IMPRINT",FACE,{"disambiguationData":[TD([[makeQuery(id+"F3.imprint","IMPRINT",EDGE,{"derivedFrom":sQuery(id+"F3.wireOp",EDGE,"E46.trimOffspring")}),-1.0]])]});
            extrude(context, id + "F4", {"entities" : qUnion([Q0]), "operationType" : NewBodyOperationType.ADD, "oppositeDirection" : true, "depth" : 5.08 * mm});
        }
        {
            var Q0;
            {var subQ0=sQuery(id+"F0.wireOp",EDGE,"E15");Q0=makeQuery(id+"F4.boolean.opBoolean","MERGE",FACE,{"derivedFrom":[makeQuery(id+"F2.opChamfer","SPLIT",FACE,{"disambiguationData":[OD(18.0)],"derivedFrom":makeQuery(id+"F1.opExtrude","CAP_FACE",FACE,{"disambiguationData":[OSD([sQuery(id+"F0.wireOp",EDGE,"E12.1.0"),sQuery(id+"F0.wireOp",EDGE,"E12.1.1"),sQuery(id+"F0.wireOp",EDGE,"E12.1.2"),sQuery(id+"F0.wireOp",EDGE,"E12.1.3"),sQuery(id+"F0.wireOp",EDGE,"E12.1.4"),sQuery(id+"F0.wireOp",EDGE,"E12.1.5"),sQuery(id+"F0.wireOp",EDGE,"E12.1.6"),sQuery(id+"F0.wireOp",EDGE,"E12.1.7"),sQuery(id+"F0.wireOp",EDGE,"E12.1.10"),sQuery(id+"F0.wireOp",EDGE,"E12.1.11"),sQuery(id+"F0.wireOp",EDGE,"E12.2.0"),sQuery(id+"F0.wireOp",EDGE,"E12.2.1"),sQuery(id+"F0.wireOp",EDGE,"E12.2.2"),sQuery(id+"F0.wireOp",EDGE,"E12.2.3"),sQuery(id+"F0.wireOp",EDGE,"E12.2.4"),sQuery(id+"F0.wireOp",EDGE,"E12.2.5"),sQuery(id+"F0.wireOp",EDGE,"E12.2.6"),sQuery(id+"F0.wireOp",EDGE,"E12.2.7"),sQuery(id+"F0.wireOp",EDGE,"E12.2.10"),sQuery(id+"F0.wireOp",EDGE,"E12.2.11"),sQuery(id+"F0.wireOp",EDGE,"E12.3.0"),sQuery(id+"F0.wireOp",EDGE,"E12.3.1"),sQuery(id+"F0.wireOp",EDGE,"E12.3.2"),sQuery(id+"F0.wireOp",EDGE,"E12.3.3"),sQuery(id+"F0.wireOp",EDGE,"E12.3.4"),sQuery(id+"F0.wireOp",EDGE,"E12.3.5"),sQuery(id+"F0.wireOp",EDGE,"E12.3.6"),sQuery(id+"F0.wireOp",EDGE,"E12.3.7"),sQuery(id+"F0.wireOp",EDGE,"E12.3.10"),sQuery(id+"F0.wireOp",EDGE,"E12.3.11"),sQuery(id+"F0.wireOp",EDGE,"E12.4.0"),sQuery(id+"F0.wireOp",EDGE,"E12.4.1"),sQuery(id+"F0.wireOp",EDGE,"E12.4.2"),sQuery(id+"F0.wireOp",EDGE,"E12.4.3"),sQuery(id+"F0.wireOp",EDGE,"E12.4.4"),sQuery(id+"F0.wireOp",EDGE,"E12.4.5"),sQuery(id+"F0.wireOp",EDGE,"E12.4.6"),sQuery(id+"F0.wireOp",EDGE,"E12.4.7"),sQuery(id+"F0.wireOp",EDGE,"E12.4.10"),sQuery(id+"F0.wireOp",EDGE,"E12.4.11"),sQuery(id+"F0.wireOp",EDGE,"E12.5.0"),sQuery(id+"F0.wireOp",EDGE,"E12.5.1"),sQuery(id+"F0.wireOp",EDGE,"E12.5.2"),sQuery(id+"F0.wireOp",EDGE,"E12.5.3"),sQuery(id+"F0.wireOp",EDGE,"E12.5.4"),sQuery(id+"F0.wireOp",EDGE,"E12.5.5"),sQuery(id+"F0.wireOp",EDGE,"E12.5.6"),sQuery(id+"F0.wireOp",EDGE,"E12.5.7"),sQuery(id+"F0.wireOp",EDGE,"E12.5.10"),sQuery(id+"F0.wireOp",EDGE,"E12.5.11"),sQuery(id+"F0.wireOp",EDGE,"E12.6.0"),sQuery(id+"F0.wireOp",EDGE,"E12.6.1"),sQuery(id+"F0.wireOp",EDGE,"E12.6.2"),sQuery(id+"F0.wireOp",EDGE,"E12.6.3"),sQuery(id+"F0.wireOp",EDGE,"E12.6.4"),sQuery(id+"F0.wireOp",EDGE,"E12.6.5"),sQuery(id+"F0.wireOp",EDGE,"E12.6.6"),sQuery(id+"F0.wireOp",EDGE,"E12.6.7"),sQuery(id+"F0.wireOp",EDGE,"E12.6.10"),sQuery(id+"F0.wireOp",EDGE,"E12.6.11"),sQuery(id+"F0.wireOp",EDGE,"E12.7.0"),sQuery(id+"F0.wireOp",EDGE,"E12.7.1"),sQuery(id+"F0.wireOp",EDGE,"E12.7.2"),sQuery(id+"F0.wireOp",EDGE,"E12.7.3"),sQuery(id+"F0.wireOp",EDGE,"E12.7.4"),sQuery(id+"F0.wireOp",EDGE,"E12.7.5"),sQuery(id+"F0.wireOp",EDGE,"E12.7.6"),sQuery(id+"F0.wireOp",EDGE,"E12.7.7"),sQuery(id+"F0.wireOp",EDGE,"E12.7.10"),sQuery(id+"F0.wireOp",EDGE,"E12.7.11"),sQuery(id+"F0.wireOp",EDGE,"E12.8.0"),sQuery(id+"F0.wireOp",EDGE,"E12.8.1"),sQuery(id+"F0.wireOp",EDGE,"E12.8.2"),sQuery(id+"F0.wireOp",EDGE,"E12.8.3"),sQuery(id+"F0.wireOp",EDGE,"E12.8.4"),sQuery(id+"F0.wireOp",EDGE,"E12.8.5"),sQuery(id+"F0.wireOp",EDGE,"E12.8.6"),sQuery(id+"F0.wireOp",EDGE,"E12.8.7"),sQuery(id+"F0.wireOp",EDGE,"E12.8.10"),sQuery(id+"F0.wireOp",EDGE,"E12.8.11"),sQuery(id+"F0.wireOp",EDGE,"E12.9.0"),sQuery(id+"F0.wireOp",EDGE,"E12.9.1"),sQuery(id+"F0.wireOp",EDGE,"E12.9.2"),sQuery(id+"F0.wireOp",EDGE,"E12.9.3"),sQuery(id+"F0.wireOp",EDGE,"E12.9.4"),sQuery(id+"F0.wireOp",EDGE,"E12.9.5"),sQuery(id+"F0.wireOp",EDGE,"E12.9.6"),sQuery(id+"F0.wireOp",EDGE,"E12.9.7"),sQuery(id+"F0.wireOp",EDGE,"E12.9.10"),sQuery(id+"F0.wireOp",EDGE,"E12.9.11"),sQuery(id+"F0.wireOp",EDGE,"E13.1.0"),sQuery(id+"F0.wireOp",EDGE,"E13.1.1"),sQuery(id+"F0.wireOp",EDGE,"E13.1.2"),sQuery(id+"F0.wireOp",EDGE,"E13.1.5"),sQuery(id+"F0.wireOp",EDGE,"E13.1.6"),sQuery(id+"F0.wireOp",EDGE,"E13.1.7"),sQuery(id+"F0.wireOp",EDGE,"E13.1.8"),sQuery(id+"F0.wireOp",EDGE,"E13.1.9"),sQuery(id+"F0.wireOp",EDGE,"E13.1.10"),sQuery(id+"F0.wireOp",EDGE,"E13.1.11"),sQuery(id+"F0.wireOp",EDGE,"E13.2.0"),sQuery(id+"F0.wireOp",EDGE,"E13.2.1"),sQuery(id+"F0.wireOp",EDGE,"E13.2.2"),sQuery(id+"F0.wireOp",EDGE,"E13.2.5"),sQuery(id+"F0.wireOp",EDGE,"E13.2.6"),sQuery(id+"F0.wireOp",EDGE,"E13.2.7"),sQuery(id+"F0.wireOp",EDGE,"E13.2.8"),sQuery(id+"F0.wireOp",EDGE,"E13.2.9"),sQuery(id+"F0.wireOp",EDGE,"E13.2.10"),sQuery(id+"F0.wireOp",EDGE,"E13.2.11"),sQuery(id+"F0.wireOp",EDGE,"E13.3.0"),sQuery(id+"F0.wireOp",EDGE,"E13.3.1"),sQuery(id+"F0.wireOp",EDGE,"E13.3.2"),sQuery(id+"F0.wireOp",EDGE,"E13.3.5"),sQuery(id+"F0.wireOp",EDGE,"E13.3.6"),sQuery(id+"F0.wireOp",EDGE,"E13.3.7"),sQuery(id+"F0.wireOp",EDGE,"E13.3.8"),sQuery(id+"F0.wireOp",EDGE,"E13.3.9"),sQuery(id+"F0.wireOp",EDGE,"E13.3.10"),sQuery(id+"F0.wireOp",EDGE,"E13.3.11"),sQuery(id+"F0.wireOp",EDGE,"E13.4.0"),sQuery(id+"F0.wireOp",EDGE,"E13.4.1"),sQuery(id+"F0.wireOp",EDGE,"E13.4.2"),sQuery(id+"F0.wireOp",EDGE,"E13.4.5"),sQuery(id+"F0.wireOp",EDGE,"E13.4.6"),sQuery(id+"F0.wireOp",EDGE,"E13.4.7"),sQuery(id+"F0.wireOp",EDGE,"E13.4.8"),sQuery(id+"F0.wireOp",EDGE,"E13.4.9"),sQuery(id+"F0.wireOp",EDGE,"E13.4.10"),sQuery(id+"F0.wireOp",EDGE,"E13.4.11"),sQuery(id+"F0.wireOp",EDGE,"E13.5.0"),sQuery(id+"F0.wireOp",EDGE,"E13.5.1"),sQuery(id+"F0.wireOp",EDGE,"E13.5.2"),sQuery(id+"F0.wireOp",EDGE,"E13.5.5"),sQuery(id+"F0.wireOp",EDGE,"E13.5.6"),sQuery(id+"F0.wireOp",EDGE,"E13.5.7"),sQuery(id+"F0.wireOp",EDGE,"E13.5.8"),sQuery(id+"F0.wireOp",EDGE,"E13.5.9"),sQuery(id+"F0.wireOp",EDGE,"E13.5.10"),sQuery(id+"F0.wireOp",EDGE,"E13.5.11"),sQuery(id+"F0.wireOp",EDGE,"E13.6.0"),sQuery(id+"F0.wireOp",EDGE,"E13.6.1"),sQuery(id+"F0.wireOp",EDGE,"E13.6.2"),sQuery(id+"F0.wireOp",EDGE,"E13.6.5"),sQuery(id+"F0.wireOp",EDGE,"E13.6.6"),sQuery(id+"F0.wireOp",EDGE,"E13.6.7"),sQuery(id+"F0.wireOp",EDGE,"E13.6.8"),sQuery(id+"F0.wireOp",EDGE,"E13.6.9"),sQuery(id+"F0.wireOp",EDGE,"E13.6.10"),sQuery(id+"F0.wireOp",EDGE,"E13.6.11"),sQuery(id+"F0.wireOp",EDGE,"E13.7.0"),sQuery(id+"F0.wireOp",EDGE,"E13.7.1"),sQuery(id+"F0.wireOp",EDGE,"E13.7.2"),sQuery(id+"F0.wireOp",EDGE,"E13.7.5"),sQuery(id+"F0.wireOp",EDGE,"E13.7.6"),sQuery(id+"F0.wireOp",EDGE,"E13.7.7"),sQuery(id+"F0.wireOp",EDGE,"E13.7.8"),sQuery(id+"F0.wireOp",EDGE,"E13.7.9"),sQuery(id+"F0.wireOp",EDGE,"E13.7.10"),sQuery(id+"F0.wireOp",EDGE,"E13.7.11"),sQuery(id+"F0.wireOp",EDGE,"E13.8.0"),sQuery(id+"F0.wireOp",EDGE,"E13.8.1"),sQuery(id+"F0.wireOp",EDGE,"E13.8.2"),sQuery(id+"F0.wireOp",EDGE,"E13.8.5"),sQuery(id+"F0.wireOp",EDGE,"E13.8.6"),sQuery(id+"F0.wireOp",EDGE,"E13.8.7"),sQuery(id+"F0.wireOp",EDGE,"E13.8.8"),sQuery(id+"F0.wireOp",EDGE,"E13.8.9"),sQuery(id+"F0.wireOp",EDGE,"E13.8.10"),sQuery(id+"F0.wireOp",EDGE,"E13.8.11"),sQuery(id+"F0.wireOp",EDGE,"E3"),sQuery(id+"F0.wireOp",EDGE,"E2"),sQuery(id+"F0.wireOp",EDGE,"E1"),sQuery(id+"F0.wireOp",EDGE,"E4"),sQuery(id+"F0.wireOp",EDGE,"E8"),sQuery(id+"F0.wireOp",EDGE,"E5"),sQuery(id+"F0.wireOp",EDGE,"E11"),sQuery(id+"F0.wireOp",EDGE,"E6"),sQuery(id+"F0.wireOp",EDGE,"E7"),sQuery(id+"F0.wireOp",EDGE,"E10"),sQuery(id+"F0.wireOp",EDGE,"E14"),subQ0,sQuery(id+"F0.wireOp",EDGE,"E20.trimOffspring"),sQuery(id+"F0.wireOp",EDGE,"E21.trimOffspring"),sQuery(id+"F0.wireOp",EDGE,"E22.trimOffspring"),sQuery(id+"F0.wireOp",EDGE,"E23.trimOffspring"),sQuery(id+"F0.wireOp",EDGE,"E24.trimOffspring"),sQuery(id+"F0.wireOp",EDGE,"E25.trimOffspring"),sQuery(id+"F0.wireOp",EDGE,"E26.trimOffspring"),sQuery(id+"F0.wireOp",EDGE,"E27.trimOffspring"),sQuery(id+"F0.wireOp",EDGE,"E28.trimOffspring"),sQuery(id+"F0.wireOp",EDGE,"E29.trimOffspring"),sQuery(id+"F0.wireOp",EDGE,"E30.trimOffspring"),sQuery(id+"F0.wireOp",EDGE,"E31.trimOffspring"),sQuery(id+"F0.wireOp",EDGE,"E32.trimOffspring"),sQuery(id+"F0.wireOp",EDGE,"E33.trimOffspring"),sQuery(id+"F0.wireOp",EDGE,"E34.trimOffspring"),sQuery(id+"F0.wireOp",EDGE,"E35.trimOffspring"),sQuery(id+"F0.wireOp",EDGE,"E36.trimOffspring"),sQuery(id+"F0.wireOp",EDGE,"E37")])],"isStart":false})}),makeQuery(id+"F4.opExtrude","CAP_FACE",FACE,{"disambiguationData":[OSD([subQ0,sQuery(id+"F3.wireOp",EDGE,"E42"),sQuery(id+"F3.wireOp",EDGE,"E43.0"),sQuery(id+"F3.wireOp",EDGE,"E46.trimOffspring"),sQuery(id+"F3.wireOp",EDGE,"E47.trimOffspring"),sQuery(id+"F3.wireOp",EDGE,"E48.trimOffspring"),sQuery(id+"F3.wireOp",EDGE,"E49.trimOffspring"),sQuery(id+"F3.wireOp",EDGE,"E50.1.0"),sQuery(id+"F3.wireOp",EDGE,"E50.1.1"),sQuery(id+"F3.wireOp",EDGE,"E50.1.5"),sQuery(id+"F3.wireOp",EDGE,"E50.1.6"),sQuery(id+"F3.wireOp",EDGE,"E50.1.8"),sQuery(id+"F3.wireOp",EDGE,"E50.1.10"),sQuery(id+"F3.wireOp",EDGE,"E50.2.0"),sQuery(id+"F3.wireOp",EDGE,"E50.2.1"),sQuery(id+"F3.wireOp",EDGE,"E50.2.5"),sQuery(id+"F3.wireOp",EDGE,"E50.2.6"),sQuery(id+"F3.wireOp",EDGE,"E50.2.8"),sQuery(id+"F3.wireOp",EDGE,"E50.2.10"),sQuery(id+"F3.wireOp",EDGE,"E50.3.0"),sQuery(id+"F3.wireOp",EDGE,"E50.3.1"),sQuery(id+"F3.wireOp",EDGE,"E50.3.5"),sQuery(id+"F3.wireOp",EDGE,"E50.3.6"),sQuery(id+"F3.wireOp",EDGE,"E50.3.8"),sQuery(id+"F3.wireOp",EDGE,"E50.3.10"),sQuery(id+"F3.wireOp",EDGE,"E50.4.0"),sQuery(id+"F3.wireOp",EDGE,"E50.4.1"),sQuery(id+"F3.wireOp",EDGE,"E50.4.5"),sQuery(id+"F3.wireOp",EDGE,"E50.4.6"),sQuery(id+"F3.wireOp",EDGE,"E50.4.8"),sQuery(id+"F3.wireOp",EDGE,"E50.4.10"),sQuery(id+"F3.wireOp",EDGE,"E50.5.0"),sQuery(id+"F3.wireOp",EDGE,"E50.5.1"),sQuery(id+"F3.wireOp",EDGE,"E50.5.5"),sQuery(id+"F3.wireOp",EDGE,"E50.5.6"),sQuery(id+"F3.wireOp",EDGE,"E50.5.8"),sQuery(id+"F3.wireOp",EDGE,"E50.5.10"),sQuery(id+"F3.wireOp",EDGE,"E50.6.0"),sQuery(id+"F3.wireOp",EDGE,"E50.6.1"),sQuery(id+"F3.wireOp",EDGE,"E50.6.5"),sQuery(id+"F3.wireOp",EDGE,"E50.6.6"),sQuery(id+"F3.wireOp",EDGE,"E50.6.8"),sQuery(id+"F3.wireOp",EDGE,"E50.6.10"),sQuery(id+"F3.wireOp",EDGE,"E50.7.0"),sQuery(id+"F3.wireOp",EDGE,"E50.7.1"),sQuery(id+"F3.wireOp",EDGE,"E50.7.5"),sQuery(id+"F3.wireOp",EDGE,"E50.7.6"),sQuery(id+"F3.wireOp",EDGE,"E50.7.8"),sQuery(id+"F3.wireOp",EDGE,"E50.7.10"),sQuery(id+"F3.wireOp",EDGE,"E50.8.0"),sQuery(id+"F3.wireOp",EDGE,"E50.8.1"),sQuery(id+"F3.wireOp",EDGE,"E50.8.5"),sQuery(id+"F3.wireOp",EDGE,"E50.8.6"),sQuery(id+"F3.wireOp",EDGE,"E50.8.8"),sQuery(id+"F3.wireOp",EDGE,"E50.8.10"),sQuery(id+"F3.wireOp",EDGE,"E51.trimOffspring"),sQuery(id+"F3.wireOp",EDGE,"E52.trimOffspring"),sQuery(id+"F3.wireOp",EDGE,"E53.trimOffspring"),sQuery(id+"F3.wireOp",EDGE,"E54.trimOffspring"),sQuery(id+"F3.wireOp",EDGE,"E55.trimOffspring"),sQuery(id+"F3.wireOp",EDGE,"E56.trimOffspring"),sQuery(id+"F3.wireOp",EDGE,"E57.trimOffspring"),sQuery(id+"F3.wireOp",EDGE,"E58.trimOffspring"),sQuery(id+"F3.wireOp",EDGE,"E59.trimOffspring"),sQuery(id+"F3.wireOp",EDGE,"E60.trimOffspring"),sQuery(id+"F3.wireOp",EDGE,"E61.trimOffspring"),sQuery(id+"F3.wireOp",EDGE,"E62.trimOffspring"),sQuery(id+"F3.wireOp",EDGE,"E63.trimOffspring"),sQuery(id+"F3.wireOp",EDGE,"E64.trimOffspring"),sQuery(id+"F3.wireOp",EDGE,"E65.trimOffspring"),sQuery(id+"F3.wireOp",EDGE,"E66.trimOffspring"),sQuery(id+"F3.wireOp",EDGE,"E67.trimOffspring"),sQuery(id+"F3.wireOp",EDGE,"E68.trimOffspring"),sQuery(id+"F3.wireOp",EDGE,"E69.trimOffspring"),sQuery(id+"F3.wireOp",EDGE,"E70.trimOffspring"),sQuery(id+"F3.wireOp",EDGE,"E71.trimOffspring"),sQuery(id+"F3.wireOp",EDGE,"E72.trimOffspring"),sQuery(id+"F3.wireOp",EDGE,"E73.trimOffspring"),sQuery(id+"F3.wireOp",EDGE,"E74.trimOffspring"),sQuery(id+"F3.wireOp",EDGE,"E75.trimOffspring"),sQuery(id+"F3.wireOp",EDGE,"E76.trimOffspring"),sQuery(id+"F3.wireOp",EDGE,"E77.trimOffspring"),sQuery(id+"F3.wireOp",EDGE,"E78.trimOffspring"),sQuery(id+"F3.wireOp",EDGE,"E79.trimOffspring"),sQuery(id+"F3.wireOp",EDGE,"E80.trimOffspring"),sQuery(id+"F3.wireOp",EDGE,"E81.trimOffspring"),sQuery(id+"F3.wireOp",EDGE,"E82.trimOffspring"),sQuery(id+"F3.wireOp",EDGE,"E83.trimOffspring"),sQuery(id+"F3.wireOp",EDGE,"E84.trimOffspring"),sQuery(id+"F3.wireOp",EDGE,"E85.trimOffspring"),sQuery(id+"F3.wireOp",EDGE,"E86.trimOffspring")])],"isStart":false})]});}
            var sketch = newSketch(context, id + "F5", { "sketchPlane" : qUnion([Q0])});
            skLineSegment(sketch, "E87", {"start": v(0, 1.2) * mm, "end": v(0, -52.24) * mm});
            skLineSegment(sketch, "E88", {"start": v(0, -52.24) * mm, "end": v(3.8, -52.24) * mm});
            skLineSegment(sketch, "E89", {"start": v(0, -52.24) * mm, "end": v(-3.81, -52.24) * mm});
            skArc(sketch, "E90", {"start": v(-3.81, -52.24) * mm, "mid": v(-2.42, -49.93) * mm, "end": v(-1.14, -47.56) * mm});
            skArc(sketch, "E91.0", {"start": v(-2.1, -53.33) * mm, "mid": v(-1.02, -51.57) * mm, "end": v(0, -49.77) * mm});
            skLineSegment(sketch, "E92", {"start": v(-2.1, -53.33) * mm, "end": v(-3.81, -52.24) * mm});
            skLineSegment(sketch, "E93", {"start": v(2.1, -53.33) * mm, "end": v(3.8, -52.24) * mm});
            skArc(sketch, "E94.trimOffspring", {"start": v(0, -45.2) * mm, "mid": v(4.44, -29.94) * mm, "end": v(4.44, -14.04) * mm});
            skArc(sketch, "E95.trimOffspring", {"start": v(1.14, -47.56) * mm, "mid": v(2.42, -49.93) * mm, "end": v(3.8, -52.24) * mm});
            skArc(sketch, "E96.trimOffspring", {"start": v(1.14, -47.56) * mm, "mid": v(5.99, -33.02) * mm, "end": v(6.88, -17.71) * mm});
            skArc(sketch, "E97.trimOffspring", {"start": v(0, -49.77) * mm, "mid": v(1.02, -51.57) * mm, "end": v(2.1, -53.33) * mm});
            skArc(sketch, "E98.1.0", {"start": v(32.2, -35.43) * mm, "mid": v(26.58, -21.17) * mm, "end": v(17.42, -8.87) * mm});
            skArc(sketch, "E98.1.1", {"start": v(29.82, -34.35) * mm, "mid": v(23.42, -19.8) * mm, "end": v(13.2, -7.62) * mm});
            skArc(sketch, "E98.1.5", {"start": v(32.2, -35.43) * mm, "mid": v(34.71, -36.42) * mm, "end": v(37.26, -37.29) * mm});
            skArc(sketch, "E98.1.6", {"start": v(32.76, -37.85) * mm, "mid": v(34.7, -38.57) * mm, "end": v(36.65, -39.23) * mm});
            skLineSegment(sketch, "E98.1.7", {"start": v(36.65, -39.23) * mm, "end": v(37.26, -37.29) * mm});
            skArc(sketch, "E98.1.8", {"start": v(33.44, -41.92) * mm, "mid": v(33.13, -39.88) * mm, "end": v(32.76, -37.85) * mm});
            skLineSegment(sketch, "E98.1.9", {"start": v(33.44, -41.92) * mm, "end": v(31.42, -42.19) * mm});
            skArc(sketch, "E98.1.10", {"start": v(31.42, -42.19) * mm, "mid": v(31.01, -39.53) * mm, "end": v(30.47, -36.89) * mm});
            skArc(sketch, "E98.2.0", {"start": v(48.21, -6.16) * mm, "mid": v(34.73, 1.15) * mm, "end": v(19.81, 4.68) * mm});
            skArc(sketch, "E98.2.1", {"start": v(45.69, -6.87) * mm, "mid": v(31.43, 0.16) * mm, "end": v(15.77, 2.92) * mm});
            skArc(sketch, "E98.2.5", {"start": v(48.21, -6.16) * mm, "mid": v(50.77, -5.3) * mm, "end": v(53.28, -4.33) * mm});
            skArc(sketch, "E98.2.6", {"start": v(50.19, -7.66) * mm, "mid": v(52.13, -6.97) * mm, "end": v(54.06, -6.21) * mm});
            skLineSegment(sketch, "E98.2.7", {"start": v(54.06, -6.21) * mm, "end": v(53.28, -4.33) * mm});
            skArc(sketch, "E98.2.8", {"start": v(53.33, -10.34) * mm, "mid": v(51.78, -8.97) * mm, "end": v(50.19, -7.66) * mm});
            skLineSegment(sketch, "E98.2.9", {"start": v(53.33, -10.34) * mm, "end": v(51.96, -11.84) * mm});
            skArc(sketch, "E98.2.10", {"start": v(51.96, -11.84) * mm, "mid": v(49.93, -10.07) * mm, "end": v(47.82, -8.4) * mm});
            skArc(sketch, "E98.3.0", {"start": v(41.65, 26.55) * mm, "mid": v(26.63, 23.48) * mm, "end": v(12.93, 16.6) * mm});
            skArc(sketch, "E98.3.1", {"start": v(40.18, 24.39) * mm, "mid": v(24.74, 20.6) * mm, "end": v(10.97, 12.65) * mm});
            skArc(sketch, "E98.3.5", {"start": v(41.65, 26.55) * mm, "mid": v(43.07, 28.85) * mm, "end": v(44.37, 31.2) * mm});
            skArc(sketch, "E98.3.6", {"start": v(44.13, 26.67) * mm, "mid": v(45.18, 28.45) * mm, "end": v(46.17, 30.27) * mm});
            skLineSegment(sketch, "E98.3.7", {"start": v(46.17, 30.27) * mm, "end": v(44.37, 31.2) * mm});
            skArc(sketch, "E98.3.8", {"start": v(48.26, 26.64) * mm, "mid": v(46.2, 26.7) * mm, "end": v(44.13, 26.67) * mm});
            skLineSegment(sketch, "E98.3.9", {"start": v(48.26, 26.64) * mm, "end": v(48.18, 24.6) * mm});
            skArc(sketch, "E98.3.10", {"start": v(48.18, 24.6) * mm, "mid": v(45.48, 24.66) * mm, "end": v(42.79, 24.58) * mm});
            skArc(sketch, "E98.4.0", {"start": v(15.6, 47.4) * mm, "mid": v(6.07, 35.39) * mm, "end": v(0, 21.31) * mm});
            skArc(sketch, "E98.4.1", {"start": v(15.87, 44.79) * mm, "mid": v(6.47, 31.96) * mm, "end": v(1.04, 17.02) * mm});
            skArc(sketch, "E98.4.5", {"start": v(15.6, 47.4) * mm, "mid": v(15.21, 50.06) * mm, "end": v(14.7, 52.7) * mm});
            skArc(sketch, "E98.4.6", {"start": v(17.43, 49.08) * mm, "mid": v(17.09, 51.12) * mm, "end": v(16.68, 53.14) * mm});
            skLineSegment(sketch, "E98.4.7", {"start": v(16.68, 53.14) * mm, "end": v(14.7, 52.7) * mm});
            skArc(sketch, "E98.4.8", {"start": v(20.62, 51.7) * mm, "mid": v(19, 50.42) * mm, "end": v(17.43, 49.08) * mm});
            skLineSegment(sketch, "E98.4.9", {"start": v(20.62, 51.7) * mm, "end": v(21.85, 50.1) * mm});
            skArc(sketch, "E98.4.10", {"start": v(21.85, 50.1) * mm, "mid": v(19.76, 48.4) * mm, "end": v(17.74, 46.62) * mm});
            skArc(sketch, "E98.5.0", {"start": v(-17.74, 46.62) * mm, "mid": v(-17.33, 31.3) * mm, "end": v(-12.93, 16.6) * mm});
            skArc(sketch, "E98.5.1", {"start": v(-15.87, 44.79) * mm, "mid": v(-14.82, 28.92) * mm, "end": v(-9.38, 13.99) * mm});
            skArc(sketch, "E98.5.5", {"start": v(-17.74, 46.62) * mm, "mid": v(-19.76, 48.4) * mm, "end": v(-21.85, 50.1) * mm});
            skArc(sketch, "E98.5.6", {"start": v(-17.43, 49.08) * mm, "mid": v(-19, 50.42) * mm, "end": v(-20.62, 51.7) * mm});
            skLineSegment(sketch, "E98.5.7", {"start": v(-20.62, 51.7) * mm, "end": v(-21.85, 50.1) * mm});
            skArc(sketch, "E98.5.8", {"start": v(-16.68, 53.14) * mm, "mid": v(-17.09, 51.12) * mm, "end": v(-17.43, 49.08) * mm});
            skLineSegment(sketch, "E98.5.9", {"start": v(-16.68, 53.14) * mm, "end": v(-14.7, 52.7) * mm});
            skArc(sketch, "E98.5.10", {"start": v(-14.7, 52.7) * mm, "mid": v(-15.21, 50.06) * mm, "end": v(-15.6, 47.4) * mm});
            skArc(sketch, "E98.6.0", {"start": v(-42.8, 24.58) * mm, "mid": v(-32.62, 13.11) * mm, "end": v(-19.81, 4.68) * mm});
            skArc(sketch, "E98.6.1", {"start": v(-40.18, 24.39) * mm, "mid": v(-29.18, 12.9) * mm, "end": v(-15.41, 4.96) * mm});
            skArc(sketch, "E98.6.5", {"start": v(-42.8, 24.58) * mm, "mid": v(-45.48, 24.66) * mm, "end": v(-48.18, 24.6) * mm});
            skArc(sketch, "E98.6.6", {"start": v(-44.13, 26.67) * mm, "mid": v(-46.2, 26.7) * mm, "end": v(-48.27, 26.64) * mm});
            skLineSegment(sketch, "E98.6.7", {"start": v(-48.27, 26.64) * mm, "end": v(-48.18, 24.6) * mm});
            skArc(sketch, "E98.6.8", {"start": v(-46.17, 30.27) * mm, "mid": v(-45.18, 28.45) * mm, "end": v(-44.13, 26.67) * mm});
            skLineSegment(sketch, "E98.6.9", {"start": v(-46.17, 30.27) * mm, "end": v(-44.37, 31.2) * mm});
            skArc(sketch, "E98.6.10", {"start": v(-44.37, 31.2) * mm, "mid": v(-43.07, 28.85) * mm, "end": v(-41.65, 26.55) * mm});
            skArc(sketch, "E98.7.0", {"start": v(-47.82, -8.4) * mm, "mid": v(-32.65, -10.65) * mm, "end": v(-17.42, -8.87) * mm});
            skArc(sketch, "E98.7.1", {"start": v(-45.69, -6.87) * mm, "mid": v(-29.89, -8.6) * mm, "end": v(-14.23, -5.83) * mm});
            skArc(sketch, "E98.7.5", {"start": v(-47.82, -8.4) * mm, "mid": v(-49.93, -10.07) * mm, "end": v(-51.96, -11.84) * mm});
            skArc(sketch, "E98.7.6", {"start": v(-50.19, -7.66) * mm, "mid": v(-51.78, -8.97) * mm, "end": v(-53.33, -10.34) * mm});
            skLineSegment(sketch, "E98.7.7", {"start": v(-53.33, -10.34) * mm, "end": v(-51.96, -11.84) * mm});
            skArc(sketch, "E98.7.8", {"start": v(-54.06, -6.21) * mm, "mid": v(-52.13, -6.97) * mm, "end": v(-50.19, -7.66) * mm});
            skLineSegment(sketch, "E98.7.9", {"start": v(-54.06, -6.21) * mm, "end": v(-53.28, -4.33) * mm});
            skArc(sketch, "E98.7.10", {"start": v(-53.28, -4.33) * mm, "mid": v(-50.77, -5.3) * mm, "end": v(-48.21, -6.16) * mm});
            skArc(sketch, "E98.8.0", {"start": v(-30.47, -36.89) * mm, "mid": v(-17.4, -28.87) * mm, "end": v(-6.88, -17.71) * mm});
            skArc(sketch, "E98.8.1", {"start": v(-29.82, -34.35) * mm, "mid": v(-16.6, -25.51) * mm, "end": v(-6.4, -13.33) * mm});
            skArc(sketch, "E98.8.5", {"start": v(-30.47, -36.89) * mm, "mid": v(-31.01, -39.53) * mm, "end": v(-31.42, -42.19) * mm});
            skArc(sketch, "E98.8.6", {"start": v(-32.76, -37.85) * mm, "mid": v(-33.13, -39.88) * mm, "end": v(-33.44, -41.92) * mm});
            skLineSegment(sketch, "E98.8.7", {"start": v(-33.44, -41.92) * mm, "end": v(-31.42, -42.19) * mm});
            skArc(sketch, "E98.8.8", {"start": v(-36.65, -39.23) * mm, "mid": v(-34.7, -38.57) * mm, "end": v(-32.76, -37.85) * mm});
            skLineSegment(sketch, "E98.8.9", {"start": v(-36.65, -39.23) * mm, "end": v(-37.26, -37.29) * mm});
            skArc(sketch, "E98.8.10", {"start": v(-37.26, -37.29) * mm, "mid": v(-34.71, -36.42) * mm, "end": v(-32.2, -35.43) * mm});
            skArc(sketch, "E99.trimOffspring", {"start": v(-17.42, -8.87) * mm, "mid": v(-26.58, -21.17) * mm, "end": v(-32.2, -35.43) * mm});
            skArc(sketch, "E100.trimOffspring", {"start": v(-13.2, -7.62) * mm, "mid": v(-8.55, -5.84) * mm, "end": v(-4.08, -3.67) * mm});
            skArc(sketch, "E101.trimOffspring", {"start": v(-13.2, -7.62) * mm, "mid": v(-23.42, -19.8) * mm, "end": v(-29.82, -34.35) * mm});
            skArc(sketch, "E102.trimOffspring", {"start": v(-15.77, 2.92) * mm, "mid": v(-11.07, 1.3) * mm, "end": v(-6.25, 0.09) * mm});
            skArc(sketch, "E103.trimOffspring", {"start": v(-19.81, 4.68) * mm, "mid": v(-34.73, 1.15) * mm, "end": v(-48.21, -6.16) * mm});
            skArc(sketch, "E104.trimOffspring", {"start": v(-15.77, 2.92) * mm, "mid": v(-31.43, 0.16) * mm, "end": v(-45.69, -6.87) * mm});
            skArc(sketch, "E105.trimOffspring", {"start": v(-10.97, 12.65) * mm, "mid": v(-24.74, 20.6) * mm, "end": v(-40.18, 24.39) * mm});
            skArc(sketch, "E106.trimOffspring", {"start": v(-12.93, 16.6) * mm, "mid": v(-26.63, 23.48) * mm, "end": v(-41.65, 26.55) * mm});
            skArc(sketch, "E107.trimOffspring", {"start": v(-10.97, 12.65) * mm, "mid": v(-8.41, 8.4) * mm, "end": v(-5.5, 4.36) * mm});
            skArc(sketch, "E108.trimOffspring", {"start": v(-1.04, 17.02) * mm, "mid": v(-6.47, 31.96) * mm, "end": v(-15.87, 44.79) * mm});
            skArc(sketch, "E109.trimOffspring", {"start": v(-1.04, 17.02) * mm, "mid": v(-1.81, 12.11) * mm, "end": v(-2.17, 7.15) * mm});
            skArc(sketch, "E110.trimOffspring", {"start": v(0, 21.31) * mm, "mid": v(-6.07, 35.39) * mm, "end": v(-15.6, 47.4) * mm});
            skArc(sketch, "E111.trimOffspring", {"start": v(9.38, 13.99) * mm, "mid": v(14.82, 28.92) * mm, "end": v(15.87, 44.79) * mm});
            skArc(sketch, "E112.trimOffspring", {"start": v(9.38, 13.99) * mm, "mid": v(5.63, 10.72) * mm, "end": v(2.17, 7.15) * mm});
            skArc(sketch, "E113.trimOffspring", {"start": v(12.93, 16.6) * mm, "mid": v(17.33, 31.3) * mm, "end": v(17.74, 46.62) * mm});
            skArc(sketch, "E114.trimOffspring", {"start": v(19.81, 4.68) * mm, "mid": v(32.62, 13.11) * mm, "end": v(42.79, 24.58) * mm});
            skArc(sketch, "E115.trimOffspring", {"start": v(15.41, 4.96) * mm, "mid": v(10.44, 4.87) * mm, "end": v(5.5, 4.36) * mm});
            skArc(sketch, "E116.trimOffspring", {"start": v(15.41, 4.96) * mm, "mid": v(29.18, 12.9) * mm, "end": v(40.18, 24.39) * mm});
            skArc(sketch, "E117.trimOffspring", {"start": v(14.23, -5.83) * mm, "mid": v(29.89, -8.6) * mm, "end": v(45.69, -6.87) * mm});
            skArc(sketch, "E118.trimOffspring", {"start": v(17.42, -8.87) * mm, "mid": v(32.65, -10.65) * mm, "end": v(47.82, -8.4) * mm});
            skArc(sketch, "E119.trimOffspring", {"start": v(14.23, -5.83) * mm, "mid": v(10.37, -2.7) * mm, "end": v(6.25, 0.09) * mm});
            skArc(sketch, "E120.trimOffspring", {"start": v(6.88, -17.71) * mm, "mid": v(17.4, -28.87) * mm, "end": v(30.47, -36.89) * mm});
            skArc(sketch, "E121.trimOffspring", {"start": v(6.4, -13.33) * mm, "mid": v(5.44, -8.45) * mm, "end": v(4.08, -3.67) * mm});
            skArc(sketch, "E122.trimOffspring", {"start": v(6.4, -13.33) * mm, "mid": v(16.6, -25.51) * mm, "end": v(29.82, -34.35) * mm});
            skArc(sketch, "E123.trimOffspring", {"start": v(-4.44, -14.04) * mm, "mid": v(-4.45, -29.94) * mm, "end": v(0, -45.2) * mm});
            skArc(sketch, "E124.trimOffspring", {"start": v(-4.44, -14.04) * mm, "mid": v(-2.03, -9.7) * mm, "end": v(0, -5.15) * mm});
            skArc(sketch, "E125.trimOffspring", {"start": v(-6.88, -17.71) * mm, "mid": v(-5.99, -33.02) * mm, "end": v(-1.14, -47.56) * mm});
            skArc(sketch, "E126.trimOffspring", {"start": v(-6.25, 0.09) * mm, "mid": v(-10.37, -2.7) * mm, "end": v(-14.23, -5.83) * mm});
            skArc(sketch, "E127.trimOffspring", {"start": v(-4.08, -3.67) * mm, "mid": v(-5.44, -8.45) * mm, "end": v(-6.4, -13.33) * mm});
            skArc(sketch, "E128.trimOffspring", {"start": v(0, -5.15) * mm, "mid": v(2.03, -9.7) * mm, "end": v(4.44, -14.04) * mm});
            skArc(sketch, "E129.trimOffspring", {"start": v(4.08, -3.67) * mm, "mid": v(8.55, -5.84) * mm, "end": v(13.2, -7.62) * mm});
            skArc(sketch, "E130.trimOffspring", {"start": v(6.25, 0.09) * mm, "mid": v(11.07, 1.3) * mm, "end": v(15.77, 2.92) * mm});
            skArc(sketch, "E131.trimOffspring", {"start": v(5.5, 4.36) * mm, "mid": v(8.41, 8.4) * mm, "end": v(10.97, 12.65) * mm});
            skArc(sketch, "E132.trimOffspring", {"start": v(2.17, 7.15) * mm, "mid": v(1.81, 12.11) * mm, "end": v(1.04, 17.02) * mm});
            skArc(sketch, "E133.trimOffspring", {"start": v(-2.17, 7.15) * mm, "mid": v(-5.63, 10.72) * mm, "end": v(-9.38, 13.99) * mm});
            skArc(sketch, "E134.trimOffspring", {"start": v(-5.5, 4.36) * mm, "mid": v(-10.44, 4.87) * mm, "end": v(-15.41, 4.96) * mm});
            skSolve(sketch);
        }
        {
            var Q0;
            Q0 = qSketchRegion(id + "F5", true);
            extrude(context, id + "F6", {"entities" : qUnion([Q0]), "operationType" : NewBodyOperationType.ADD, "oppositeDirection" : true, "depth" : 5.08 * mm});
        }
        {
            var Q0;
            {var subQ0=sQuery(id+"F0.wireOp",EDGE,"E15");Q0=makeQuery(id+"F6.boolean.opBoolean","MERGE",FACE,{"derivedFrom":[makeQuery(id+"F4.boolean.opBoolean","MERGE",FACE,{"derivedFrom":[makeQuery(id+"F2.opChamfer","SPLIT",FACE,{"disambiguationData":[OD(18.0)],"derivedFrom":makeQuery(id+"F1.opExtrude","CAP_FACE",FACE,{"disambiguationData":[OSD([sQuery(id+"F0.wireOp",EDGE,"E12.1.0"),sQuery(id+"F0.wireOp",EDGE,"E12.1.1"),sQuery(id+"F0.wireOp",EDGE,"E12.1.2"),sQuery(id+"F0.wireOp",EDGE,"E12.1.3"),sQuery(id+"F0.wireOp",EDGE,"E12.1.4"),sQuery(id+"F0.wireOp",EDGE,"E12.1.5"),sQuery(id+"F0.wireOp",EDGE,"E12.1.6"),sQuery(id+"F0.wireOp",EDGE,"E12.1.7"),sQuery(id+"F0.wireOp",EDGE,"E12.1.10"),sQuery(id+"F0.wireOp",EDGE,"E12.1.11"),sQuery(id+"F0.wireOp",EDGE,"E12.2.0"),sQuery(id+"F0.wireOp",EDGE,"E12.2.1"),sQuery(id+"F0.wireOp",EDGE,"E12.2.2"),sQuery(id+"F0.wireOp",EDGE,"E12.2.3"),sQuery(id+"F0.wireOp",EDGE,"E12.2.4"),sQuery(id+"F0.wireOp",EDGE,"E12.2.5"),sQuery(id+"F0.wireOp",EDGE,"E12.2.6"),sQuery(id+"F0.wireOp",EDGE,"E12.2.7"),sQuery(id+"F0.wireOp",EDGE,"E12.2.10"),sQuery(id+"F0.wireOp",EDGE,"E12.2.11"),sQuery(id+"F0.wireOp",EDGE,"E12.3.0"),sQuery(id+"F0.wireOp",EDGE,"E12.3.1"),sQuery(id+"F0.wireOp",EDGE,"E12.3.2"),sQuery(id+"F0.wireOp",EDGE,"E12.3.3"),sQuery(id+"F0.wireOp",EDGE,"E12.3.4"),sQuery(id+"F0.wireOp",EDGE,"E12.3.5"),sQuery(id+"F0.wireOp",EDGE,"E12.3.6"),sQuery(id+"F0.wireOp",EDGE,"E12.3.7"),sQuery(id+"F0.wireOp",EDGE,"E12.3.10"),sQuery(id+"F0.wireOp",EDGE,"E12.3.11"),sQuery(id+"F0.wireOp",EDGE,"E12.4.0"),sQuery(id+"F0.wireOp",EDGE,"E12.4.1"),sQuery(id+"F0.wireOp",EDGE,"E12.4.2"),sQuery(id+"F0.wireOp",EDGE,"E12.4.3"),sQuery(id+"F0.wireOp",EDGE,"E12.4.4"),sQuery(id+"F0.wireOp",EDGE,"E12.4.5"),sQuery(id+"F0.wireOp",EDGE,"E12.4.6"),sQuery(id+"F0.wireOp",EDGE,"E12.4.7"),sQuery(id+"F0.wireOp",EDGE,"E12.4.10"),sQuery(id+"F0.wireOp",EDGE,"E12.4.11"),sQuery(id+"F0.wireOp",EDGE,"E12.5.0"),sQuery(id+"F0.wireOp",EDGE,"E12.5.1"),sQuery(id+"F0.wireOp",EDGE,"E12.5.2"),sQuery(id+"F0.wireOp",EDGE,"E12.5.3"),sQuery(id+"F0.wireOp",EDGE,"E12.5.4"),sQuery(id+"F0.wireOp",EDGE,"E12.5.5"),sQuery(id+"F0.wireOp",EDGE,"E12.5.6"),sQuery(id+"F0.wireOp",EDGE,"E12.5.7"),sQuery(id+"F0.wireOp",EDGE,"E12.5.10"),sQuery(id+"F0.wireOp",EDGE,"E12.5.11"),sQuery(id+"F0.wireOp",EDGE,"E12.6.0"),sQuery(id+"F0.wireOp",EDGE,"E12.6.1"),sQuery(id+"F0.wireOp",EDGE,"E12.6.2"),sQuery(id+"F0.wireOp",EDGE,"E12.6.3"),sQuery(id+"F0.wireOp",EDGE,"E12.6.4"),sQuery(id+"F0.wireOp",EDGE,"E12.6.5"),sQuery(id+"F0.wireOp",EDGE,"E12.6.6"),sQuery(id+"F0.wireOp",EDGE,"E12.6.7"),sQuery(id+"F0.wireOp",EDGE,"E12.6.10"),sQuery(id+"F0.wireOp",EDGE,"E12.6.11"),sQuery(id+"F0.wireOp",EDGE,"E12.7.0"),sQuery(id+"F0.wireOp",EDGE,"E12.7.1"),sQuery(id+"F0.wireOp",EDGE,"E12.7.2"),sQuery(id+"F0.wireOp",EDGE,"E12.7.3"),sQuery(id+"F0.wireOp",EDGE,"E12.7.4"),sQuery(id+"F0.wireOp",EDGE,"E12.7.5"),sQuery(id+"F0.wireOp",EDGE,"E12.7.6"),sQuery(id+"F0.wireOp",EDGE,"E12.7.7"),sQuery(id+"F0.wireOp",EDGE,"E12.7.10"),sQuery(id+"F0.wireOp",EDGE,"E12.7.11"),sQuery(id+"F0.wireOp",EDGE,"E12.8.0"),sQuery(id+"F0.wireOp",EDGE,"E12.8.1"),sQuery(id+"F0.wireOp",EDGE,"E12.8.2"),sQuery(id+"F0.wireOp",EDGE,"E12.8.3"),sQuery(id+"F0.wireOp",EDGE,"E12.8.4"),sQuery(id+"F0.wireOp",EDGE,"E12.8.5"),sQuery(id+"F0.wireOp",EDGE,"E12.8.6"),sQuery(id+"F0.wireOp",EDGE,"E12.8.7"),sQuery(id+"F0.wireOp",EDGE,"E12.8.10"),sQuery(id+"F0.wireOp",EDGE,"E12.8.11"),sQuery(id+"F0.wireOp",EDGE,"E12.9.0"),sQuery(id+"F0.wireOp",EDGE,"E12.9.1"),sQuery(id+"F0.wireOp",EDGE,"E12.9.2"),sQuery(id+"F0.wireOp",EDGE,"E12.9.3"),sQuery(id+"F0.wireOp",EDGE,"E12.9.4"),sQuery(id+"F0.wireOp",EDGE,"E12.9.5"),sQuery(id+"F0.wireOp",EDGE,"E12.9.6"),sQuery(id+"F0.wireOp",EDGE,"E12.9.7"),sQuery(id+"F0.wireOp",EDGE,"E12.9.10"),sQuery(id+"F0.wireOp",EDGE,"E12.9.11"),sQuery(id+"F0.wireOp",EDGE,"E13.1.0"),sQuery(id+"F0.wireOp",EDGE,"E13.1.1"),sQuery(id+"F0.wireOp",EDGE,"E13.1.2"),sQuery(id+"F0.wireOp",EDGE,"E13.1.5"),sQuery(id+"F0.wireOp",EDGE,"E13.1.6"),sQuery(id+"F0.wireOp",EDGE,"E13.1.7"),sQuery(id+"F0.wireOp",EDGE,"E13.1.8"),sQuery(id+"F0.wireOp",EDGE,"E13.1.9"),sQuery(id+"F0.wireOp",EDGE,"E13.1.10"),sQuery(id+"F0.wireOp",EDGE,"E13.1.11"),sQuery(id+"F0.wireOp",EDGE,"E13.2.0"),sQuery(id+"F0.wireOp",EDGE,"E13.2.1"),sQuery(id+"F0.wireOp",EDGE,"E13.2.2"),sQuery(id+"F0.wireOp",EDGE,"E13.2.5"),sQuery(id+"F0.wireOp",EDGE,"E13.2.6"),sQuery(id+"F0.wireOp",EDGE,"E13.2.7"),sQuery(id+"F0.wireOp",EDGE,"E13.2.8"),sQuery(id+"F0.wireOp",EDGE,"E13.2.9"),sQuery(id+"F0.wireOp",EDGE,"E13.2.10"),sQuery(id+"F0.wireOp",EDGE,"E13.2.11"),sQuery(id+"F0.wireOp",EDGE,"E13.3.0"),sQuery(id+"F0.wireOp",EDGE,"E13.3.1"),sQuery(id+"F0.wireOp",EDGE,"E13.3.2"),sQuery(id+"F0.wireOp",EDGE,"E13.3.5"),sQuery(id+"F0.wireOp",EDGE,"E13.3.6"),sQuery(id+"F0.wireOp",EDGE,"E13.3.7"),sQuery(id+"F0.wireOp",EDGE,"E13.3.8"),sQuery(id+"F0.wireOp",EDGE,"E13.3.9"),sQuery(id+"F0.wireOp",EDGE,"E13.3.10"),sQuery(id+"F0.wireOp",EDGE,"E13.3.11"),sQuery(id+"F0.wireOp",EDGE,"E13.4.0"),sQuery(id+"F0.wireOp",EDGE,"E13.4.1"),sQuery(id+"F0.wireOp",EDGE,"E13.4.2"),sQuery(id+"F0.wireOp",EDGE,"E13.4.5"),sQuery(id+"F0.wireOp",EDGE,"E13.4.6"),sQuery(id+"F0.wireOp",EDGE,"E13.4.7"),sQuery(id+"F0.wireOp",EDGE,"E13.4.8"),sQuery(id+"F0.wireOp",EDGE,"E13.4.9"),sQuery(id+"F0.wireOp",EDGE,"E13.4.10"),sQuery(id+"F0.wireOp",EDGE,"E13.4.11"),sQuery(id+"F0.wireOp",EDGE,"E13.5.0"),sQuery(id+"F0.wireOp",EDGE,"E13.5.1"),sQuery(id+"F0.wireOp",EDGE,"E13.5.2"),sQuery(id+"F0.wireOp",EDGE,"E13.5.5"),sQuery(id+"F0.wireOp",EDGE,"E13.5.6"),sQuery(id+"F0.wireOp",EDGE,"E13.5.7"),sQuery(id+"F0.wireOp",EDGE,"E13.5.8"),sQuery(id+"F0.wireOp",EDGE,"E13.5.9"),sQuery(id+"F0.wireOp",EDGE,"E13.5.10"),sQuery(id+"F0.wireOp",EDGE,"E13.5.11"),sQuery(id+"F0.wireOp",EDGE,"E13.6.0"),sQuery(id+"F0.wireOp",EDGE,"E13.6.1"),sQuery(id+"F0.wireOp",EDGE,"E13.6.2"),sQuery(id+"F0.wireOp",EDGE,"E13.6.5"),sQuery(id+"F0.wireOp",EDGE,"E13.6.6"),sQuery(id+"F0.wireOp",EDGE,"E13.6.7"),sQuery(id+"F0.wireOp",EDGE,"E13.6.8"),sQuery(id+"F0.wireOp",EDGE,"E13.6.9"),sQuery(id+"F0.wireOp",EDGE,"E13.6.10"),sQuery(id+"F0.wireOp",EDGE,"E13.6.11"),sQuery(id+"F0.wireOp",EDGE,"E13.7.0"),sQuery(id+"F0.wireOp",EDGE,"E13.7.1"),sQuery(id+"F0.wireOp",EDGE,"E13.7.2"),sQuery(id+"F0.wireOp",EDGE,"E13.7.5"),sQuery(id+"F0.wireOp",EDGE,"E13.7.6"),sQuery(id+"F0.wireOp",EDGE,"E13.7.7"),sQuery(id+"F0.wireOp",EDGE,"E13.7.8"),sQuery(id+"F0.wireOp",EDGE,"E13.7.9"),sQuery(id+"F0.wireOp",EDGE,"E13.7.10"),sQuery(id+"F0.wireOp",EDGE,"E13.7.11"),sQuery(id+"F0.wireOp",EDGE,"E13.8.0"),sQuery(id+"F0.wireOp",EDGE,"E13.8.1"),sQuery(id+"F0.wireOp",EDGE,"E13.8.2"),sQuery(id+"F0.wireOp",EDGE,"E13.8.5"),sQuery(id+"F0.wireOp",EDGE,"E13.8.6"),sQuery(id+"F0.wireOp",EDGE,"E13.8.7"),sQuery(id+"F0.wireOp",EDGE,"E13.8.8"),sQuery(id+"F0.wireOp",EDGE,"E13.8.9"),sQuery(id+"F0.wireOp",EDGE,"E13.8.10"),sQuery(id+"F0.wireOp",EDGE,"E13.8.11"),sQuery(id+"F0.wireOp",EDGE,"E3"),sQuery(id+"F0.wireOp",EDGE,"E2"),sQuery(id+"F0.wireOp",EDGE,"E1"),sQuery(id+"F0.wireOp",EDGE,"E4"),sQuery(id+"F0.wireOp",EDGE,"E8"),sQuery(id+"F0.wireOp",EDGE,"E5"),sQuery(id+"F0.wireOp",EDGE,"E11"),sQuery(id+"F0.wireOp",EDGE,"E6"),sQuery(id+"F0.wireOp",EDGE,"E7"),sQuery(id+"F0.wireOp",EDGE,"E10"),sQuery(id+"F0.wireOp",EDGE,"E14"),subQ0,sQuery(id+"F0.wireOp",EDGE,"E20.trimOffspring"),sQuery(id+"F0.wireOp",EDGE,"E21.trimOffspring"),sQuery(id+"F0.wireOp",EDGE,"E22.trimOffspring"),sQuery(id+"F0.wireOp",EDGE,"E23.trimOffspring"),sQuery(id+"F0.wireOp",EDGE,"E24.trimOffspring"),sQuery(id+"F0.wireOp",EDGE,"E25.trimOffspring"),sQuery(id+"F0.wireOp",EDGE,"E26.trimOffspring"),sQuery(id+"F0.wireOp",EDGE,"E27.trimOffspring"),sQuery(id+"F0.wireOp",EDGE,"E28.trimOffspring"),sQuery(id+"F0.wireOp",EDGE,"E29.trimOffspring"),sQuery(id+"F0.wireOp",EDGE,"E30.trimOffspring"),sQuery(id+"F0.wireOp",EDGE,"E31.trimOffspring"),sQuery(id+"F0.wireOp",EDGE,"E32.trimOffspring"),sQuery(id+"F0.wireOp",EDGE,"E33.trimOffspring"),sQuery(id+"F0.wireOp",EDGE,"E34.trimOffspring"),sQuery(id+"F0.wireOp",EDGE,"E35.trimOffspring"),sQuery(id+"F0.wireOp",EDGE,"E36.trimOffspring"),sQuery(id+"F0.wireOp",EDGE,"E37")])],"isStart":false})}),makeQuery(id+"F4.opExtrude","CAP_FACE",FACE,{"disambiguationData":[OSD([subQ0,sQuery(id+"F3.wireOp",EDGE,"E42"),sQuery(id+"F3.wireOp",EDGE,"E43.0"),sQuery(id+"F3.wireOp",EDGE,"E46.trimOffspring"),sQuery(id+"F3.wireOp",EDGE,"E47.trimOffspring"),sQuery(id+"F3.wireOp",EDGE,"E48.trimOffspring"),sQuery(id+"F3.wireOp",EDGE,"E49.trimOffspring"),sQuery(id+"F3.wireOp",EDGE,"E50.1.0"),sQuery(id+"F3.wireOp",EDGE,"E50.1.1"),sQuery(id+"F3.wireOp",EDGE,"E50.1.5"),sQuery(id+"F3.wireOp",EDGE,"E50.1.6"),sQuery(id+"F3.wireOp",EDGE,"E50.1.8"),sQuery(id+"F3.wireOp",EDGE,"E50.1.10"),sQuery(id+"F3.wireOp",EDGE,"E50.2.0"),sQuery(id+"F3.wireOp",EDGE,"E50.2.1"),sQuery(id+"F3.wireOp",EDGE,"E50.2.5"),sQuery(id+"F3.wireOp",EDGE,"E50.2.6"),sQuery(id+"F3.wireOp",EDGE,"E50.2.8"),sQuery(id+"F3.wireOp",EDGE,"E50.2.10"),sQuery(id+"F3.wireOp",EDGE,"E50.3.0"),sQuery(id+"F3.wireOp",EDGE,"E50.3.1"),sQuery(id+"F3.wireOp",EDGE,"E50.3.5"),sQuery(id+"F3.wireOp",EDGE,"E50.3.6"),sQuery(id+"F3.wireOp",EDGE,"E50.3.8"),sQuery(id+"F3.wireOp",EDGE,"E50.3.10"),sQuery(id+"F3.wireOp",EDGE,"E50.4.0"),sQuery(id+"F3.wireOp",EDGE,"E50.4.1"),sQuery(id+"F3.wireOp",EDGE,"E50.4.5"),sQuery(id+"F3.wireOp",EDGE,"E50.4.6"),sQuery(id+"F3.wireOp",EDGE,"E50.4.8"),sQuery(id+"F3.wireOp",EDGE,"E50.4.10"),sQuery(id+"F3.wireOp",EDGE,"E50.5.0"),sQuery(id+"F3.wireOp",EDGE,"E50.5.1"),sQuery(id+"F3.wireOp",EDGE,"E50.5.5"),sQuery(id+"F3.wireOp",EDGE,"E50.5.6"),sQuery(id+"F3.wireOp",EDGE,"E50.5.8"),sQuery(id+"F3.wireOp",EDGE,"E50.5.10"),sQuery(id+"F3.wireOp",EDGE,"E50.6.0"),sQuery(id+"F3.wireOp",EDGE,"E50.6.1"),sQuery(id+"F3.wireOp",EDGE,"E50.6.5"),sQuery(id+"F3.wireOp",EDGE,"E50.6.6"),sQuery(id+"F3.wireOp",EDGE,"E50.6.8"),sQuery(id+"F3.wireOp",EDGE,"E50.6.10"),sQuery(id+"F3.wireOp",EDGE,"E50.7.0"),sQuery(id+"F3.wireOp",EDGE,"E50.7.1"),sQuery(id+"F3.wireOp",EDGE,"E50.7.5"),sQuery(id+"F3.wireOp",EDGE,"E50.7.6"),sQuery(id+"F3.wireOp",EDGE,"E50.7.8"),sQuery(id+"F3.wireOp",EDGE,"E50.7.10"),sQuery(id+"F3.wireOp",EDGE,"E50.8.0"),sQuery(id+"F3.wireOp",EDGE,"E50.8.1"),sQuery(id+"F3.wireOp",EDGE,"E50.8.5"),sQuery(id+"F3.wireOp",EDGE,"E50.8.6"),sQuery(id+"F3.wireOp",EDGE,"E50.8.8"),sQuery(id+"F3.wireOp",EDGE,"E50.8.10"),sQuery(id+"F3.wireOp",EDGE,"E51.trimOffspring"),sQuery(id+"F3.wireOp",EDGE,"E52.trimOffspring"),sQuery(id+"F3.wireOp",EDGE,"E53.trimOffspring"),sQuery(id+"F3.wireOp",EDGE,"E54.trimOffspring"),sQuery(id+"F3.wireOp",EDGE,"E55.trimOffspring"),sQuery(id+"F3.wireOp",EDGE,"E56.trimOffspring"),sQuery(id+"F3.wireOp",EDGE,"E57.trimOffspring"),sQuery(id+"F3.wireOp",EDGE,"E58.trimOffspring"),sQuery(id+"F3.wireOp",EDGE,"E59.trimOffspring"),sQuery(id+"F3.wireOp",EDGE,"E60.trimOffspring"),sQuery(id+"F3.wireOp",EDGE,"E61.trimOffspring"),sQuery(id+"F3.wireOp",EDGE,"E62.trimOffspring"),sQuery(id+"F3.wireOp",EDGE,"E63.trimOffspring"),sQuery(id+"F3.wireOp",EDGE,"E64.trimOffspring"),sQuery(id+"F3.wireOp",EDGE,"E65.trimOffspring"),sQuery(id+"F3.wireOp",EDGE,"E66.trimOffspring"),sQuery(id+"F3.wireOp",EDGE,"E67.trimOffspring"),sQuery(id+"F3.wireOp",EDGE,"E68.trimOffspring"),sQuery(id+"F3.wireOp",EDGE,"E69.trimOffspring"),sQuery(id+"F3.wireOp",EDGE,"E70.trimOffspring"),sQuery(id+"F3.wireOp",EDGE,"E71.trimOffspring"),sQuery(id+"F3.wireOp",EDGE,"E72.trimOffspring"),sQuery(id+"F3.wireOp",EDGE,"E73.trimOffspring"),sQuery(id+"F3.wireOp",EDGE,"E74.trimOffspring"),sQuery(id+"F3.wireOp",EDGE,"E75.trimOffspring"),sQuery(id+"F3.wireOp",EDGE,"E76.trimOffspring"),sQuery(id+"F3.wireOp",EDGE,"E77.trimOffspring"),sQuery(id+"F3.wireOp",EDGE,"E78.trimOffspring"),sQuery(id+"F3.wireOp",EDGE,"E79.trimOffspring"),sQuery(id+"F3.wireOp",EDGE,"E80.trimOffspring"),sQuery(id+"F3.wireOp",EDGE,"E81.trimOffspring"),sQuery(id+"F3.wireOp",EDGE,"E82.trimOffspring"),sQuery(id+"F3.wireOp",EDGE,"E83.trimOffspring"),sQuery(id+"F3.wireOp",EDGE,"E84.trimOffspring"),sQuery(id+"F3.wireOp",EDGE,"E85.trimOffspring"),sQuery(id+"F3.wireOp",EDGE,"E86.trimOffspring")])],"isStart":false})]}),makeQuery(id+"F6.opExtrude","CAP_FACE",FACE,{"disambiguationData":[OSD([sQuery(id+"F5.wireOp",EDGE,"E88"),sQuery(id+"F5.wireOp",EDGE,"E89"),sQuery(id+"F5.wireOp",EDGE,"E90"),sQuery(id+"F5.wireOp",EDGE,"E91.0"),sQuery(id+"F5.wireOp",EDGE,"E92"),sQuery(id+"F5.wireOp",EDGE,"E93"),sQuery(id+"F5.wireOp",EDGE,"E94.trimOffspring"),sQuery(id+"F5.wireOp",EDGE,"E95.trimOffspring"),sQuery(id+"F5.wireOp",EDGE,"E96.trimOffspring"),sQuery(id+"F5.wireOp",EDGE,"E97.trimOffspring"),sQuery(id+"F5.wireOp",EDGE,"E98.1.0"),sQuery(id+"F5.wireOp",EDGE,"E98.1.1"),sQuery(id+"F5.wireOp",EDGE,"E98.1.5"),sQuery(id+"F5.wireOp",EDGE,"E98.1.6"),sQuery(id+"F5.wireOp",EDGE,"E98.1.7"),sQuery(id+"F5.wireOp",EDGE,"E98.1.8"),sQuery(id+"F5.wireOp",EDGE,"E98.1.9"),sQuery(id+"F5.wireOp",EDGE,"E98.1.10"),sQuery(id+"F5.wireOp",EDGE,"E98.2.0"),sQuery(id+"F5.wireOp",EDGE,"E98.2.1"),sQuery(id+"F5.wireOp",EDGE,"E98.2.5"),sQuery(id+"F5.wireOp",EDGE,"E98.2.6"),sQuery(id+"F5.wireOp",EDGE,"E98.2.7"),sQuery(id+"F5.wireOp",EDGE,"E98.2.8"),sQuery(id+"F5.wireOp",EDGE,"E98.2.9"),sQuery(id+"F5.wireOp",EDGE,"E98.2.10"),sQuery(id+"F5.wireOp",EDGE,"E98.3.0"),sQuery(id+"F5.wireOp",EDGE,"E98.3.1"),sQuery(id+"F5.wireOp",EDGE,"E98.3.5"),sQuery(id+"F5.wireOp",EDGE,"E98.3.6"),sQuery(id+"F5.wireOp",EDGE,"E98.3.7"),sQuery(id+"F5.wireOp",EDGE,"E98.3.8"),sQuery(id+"F5.wireOp",EDGE,"E98.3.9"),sQuery(id+"F5.wireOp",EDGE,"E98.3.10"),sQuery(id+"F5.wireOp",EDGE,"E98.4.0"),sQuery(id+"F5.wireOp",EDGE,"E98.4.1"),sQuery(id+"F5.wireOp",EDGE,"E98.4.5"),sQuery(id+"F5.wireOp",EDGE,"E98.4.6"),sQuery(id+"F5.wireOp",EDGE,"E98.4.7"),sQuery(id+"F5.wireOp",EDGE,"E98.4.8"),sQuery(id+"F5.wireOp",EDGE,"E98.4.9"),sQuery(id+"F5.wireOp",EDGE,"E98.4.10"),sQuery(id+"F5.wireOp",EDGE,"E98.5.0"),sQuery(id+"F5.wireOp",EDGE,"E98.5.1"),sQuery(id+"F5.wireOp",EDGE,"E98.5.5"),sQuery(id+"F5.wireOp",EDGE,"E98.5.6"),sQuery(id+"F5.wireOp",EDGE,"E98.5.7"),sQuery(id+"F5.wireOp",EDGE,"E98.5.8"),sQuery(id+"F5.wireOp",EDGE,"E98.5.9"),sQuery(id+"F5.wireOp",EDGE,"E98.5.10"),sQuery(id+"F5.wireOp",EDGE,"E98.6.0"),sQuery(id+"F5.wireOp",EDGE,"E98.6.1"),sQuery(id+"F5.wireOp",EDGE,"E98.6.5"),sQuery(id+"F5.wireOp",EDGE,"E98.6.6"),sQuery(id+"F5.wireOp",EDGE,"E98.6.7"),sQuery(id+"F5.wireOp",EDGE,"E98.6.8"),sQuery(id+"F5.wireOp",EDGE,"E98.6.9"),sQuery(id+"F5.wireOp",EDGE,"E98.6.10"),sQuery(id+"F5.wireOp",EDGE,"E98.7.0"),sQuery(id+"F5.wireOp",EDGE,"E98.7.1"),sQuery(id+"F5.wireOp",EDGE,"E98.7.5"),sQuery(id+"F5.wireOp",EDGE,"E98.7.6"),sQuery(id+"F5.wireOp",EDGE,"E98.7.7"),sQuery(id+"F5.wireOp",EDGE,"E98.7.8"),sQuery(id+"F5.wireOp",EDGE,"E98.7.9"),sQuery(id+"F5.wireOp",EDGE,"E98.7.10"),sQuery(id+"F5.wireOp",EDGE,"E98.8.0"),sQuery(id+"F5.wireOp",EDGE,"E98.8.1"),sQuery(id+"F5.wireOp",EDGE,"E98.8.5"),sQuery(id+"F5.wireOp",EDGE,"E98.8.6"),sQuery(id+"F5.wireOp",EDGE,"E98.8.7"),sQuery(id+"F5.wireOp",EDGE,"E98.8.8"),sQuery(id+"F5.wireOp",EDGE,"E98.8.9"),sQuery(id+"F5.wireOp",EDGE,"E98.8.10"),sQuery(id+"F5.wireOp",EDGE,"E99.trimOffspring"),sQuery(id+"F5.wireOp",EDGE,"E100.trimOffspring"),sQuery(id+"F5.wireOp",EDGE,"E101.trimOffspring"),sQuery(id+"F5.wireOp",EDGE,"E102.trimOffspring"),sQuery(id+"F5.wireOp",EDGE,"E103.trimOffspring"),sQuery(id+"F5.wireOp",EDGE,"E104.trimOffspring"),sQuery(id+"F5.wireOp",EDGE,"E105.trimOffspring"),sQuery(id+"F5.wireOp",EDGE,"E106.trimOffspring"),sQuery(id+"F5.wireOp",EDGE,"E107.trimOffspring"),sQuery(id+"F5.wireOp",EDGE,"E108.trimOffspring"),sQuery(id+"F5.wireOp",EDGE,"E109.trimOffspring"),sQuery(id+"F5.wireOp",EDGE,"E110.trimOffspring"),sQuery(id+"F5.wireOp",EDGE,"E111.trimOffspring"),sQuery(id+"F5.wireOp",EDGE,"E112.trimOffspring"),sQuery(id+"F5.wireOp",EDGE,"E113.trimOffspring"),sQuery(id+"F5.wireOp",EDGE,"E114.trimOffspring"),sQuery(id+"F5.wireOp",EDGE,"E115.trimOffspring"),sQuery(id+"F5.wireOp",EDGE,"E116.trimOffspring"),sQuery(id+"F5.wireOp",EDGE,"E117.trimOffspring"),sQuery(id+"F5.wireOp",EDGE,"E118.trimOffspring"),sQuery(id+"F5.wireOp",EDGE,"E119.trimOffspring"),sQuery(id+"F5.wireOp",EDGE,"E120.trimOffspring"),sQuery(id+"F5.wireOp",EDGE,"E121.trimOffspring"),sQuery(id+"F5.wireOp",EDGE,"E122.trimOffspring"),sQuery(id+"F5.wireOp",EDGE,"E123.trimOffspring"),sQuery(id+"F5.wireOp",EDGE,"E124.trimOffspring"),sQuery(id+"F5.wireOp",EDGE,"E125.trimOffspring"),sQuery(id+"F5.wireOp",EDGE,"E126.trimOffspring"),sQuery(id+"F5.wireOp",EDGE,"E127.trimOffspring"),sQuery(id+"F5.wireOp",EDGE,"E128.trimOffspring"),sQuery(id+"F5.wireOp",EDGE,"E129.trimOffspring"),sQuery(id+"F5.wireOp",EDGE,"E130.trimOffspring"),sQuery(id+"F5.wireOp",EDGE,"E131.trimOffspring"),sQuery(id+"F5.wireOp",EDGE,"E132.trimOffspring"),sQuery(id+"F5.wireOp",EDGE,"E133.trimOffspring"),sQuery(id+"F5.wireOp",EDGE,"E134.trimOffspring")])],"isStart":true})]});}
            var sketch = newSketch(context, id + "F7", { "sketchPlane" : qUnion([Q0])});
            skCircle(sketch, "E135", {"center": v(0, 0) * mm, "radius": 55.24 * mm});
            skCircle(sketch, "E136", {"center": v(0, 0) * mm, "radius": 47.58 * mm});
            skCircle(sketch, "E137", {"center": v(0, 0) * mm, "radius": 49.27 * mm});
            skSolve(sketch);
        }
        {
            var Q0;
            Q0 = qSketchRegion(id + "F7", true);
            extrude(context, id + "F8", {"entities" : qUnion([Q0]), "operationType" : NewBodyOperationType.ADD, "oppositeDirection" : true, "depth" : 5.08 * mm});
        }
        {
            var Q0;
            {var subQ0=sQuery(id+"F0.wireOp",EDGE,"E15");Q0=makeQuery(id+"F8.boolean.opBoolean","MERGE",FACE,{"derivedFrom":[makeQuery(id+"F6.boolean.opBoolean","MERGE",FACE,{"derivedFrom":[makeQuery(id+"F4.boolean.opBoolean","MERGE",FACE,{"derivedFrom":[makeQuery(id+"F2.opChamfer","SPLIT",FACE,{"disambiguationData":[OD(18.0)],"derivedFrom":makeQuery(id+"F1.opExtrude","CAP_FACE",FACE,{"disambiguationData":[OSD([sQuery(id+"F0.wireOp",EDGE,"E12.1.0"),sQuery(id+"F0.wireOp",EDGE,"E12.1.1"),sQuery(id+"F0.wireOp",EDGE,"E12.1.2"),sQuery(id+"F0.wireOp",EDGE,"E12.1.3"),sQuery(id+"F0.wireOp",EDGE,"E12.1.4"),sQuery(id+"F0.wireOp",EDGE,"E12.1.5"),sQuery(id+"F0.wireOp",EDGE,"E12.1.6"),sQuery(id+"F0.wireOp",EDGE,"E12.1.7"),sQuery(id+"F0.wireOp",EDGE,"E12.1.10"),sQuery(id+"F0.wireOp",EDGE,"E12.1.11"),sQuery(id+"F0.wireOp",EDGE,"E12.2.0"),sQuery(id+"F0.wireOp",EDGE,"E12.2.1"),sQuery(id+"F0.wireOp",EDGE,"E12.2.2"),sQuery(id+"F0.wireOp",EDGE,"E12.2.3"),sQuery(id+"F0.wireOp",EDGE,"E12.2.4"),sQuery(id+"F0.wireOp",EDGE,"E12.2.5"),sQuery(id+"F0.wireOp",EDGE,"E12.2.6"),sQuery(id+"F0.wireOp",EDGE,"E12.2.7"),sQuery(id+"F0.wireOp",EDGE,"E12.2.10"),sQuery(id+"F0.wireOp",EDGE,"E12.2.11"),sQuery(id+"F0.wireOp",EDGE,"E12.3.0"),sQuery(id+"F0.wireOp",EDGE,"E12.3.1"),sQuery(id+"F0.wireOp",EDGE,"E12.3.2"),sQuery(id+"F0.wireOp",EDGE,"E12.3.3"),sQuery(id+"F0.wireOp",EDGE,"E12.3.4"),sQuery(id+"F0.wireOp",EDGE,"E12.3.5"),sQuery(id+"F0.wireOp",EDGE,"E12.3.6"),sQuery(id+"F0.wireOp",EDGE,"E12.3.7"),sQuery(id+"F0.wireOp",EDGE,"E12.3.10"),sQuery(id+"F0.wireOp",EDGE,"E12.3.11"),sQuery(id+"F0.wireOp",EDGE,"E12.4.0"),sQuery(id+"F0.wireOp",EDGE,"E12.4.1"),sQuery(id+"F0.wireOp",EDGE,"E12.4.2"),sQuery(id+"F0.wireOp",EDGE,"E12.4.3"),sQuery(id+"F0.wireOp",EDGE,"E12.4.4"),sQuery(id+"F0.wireOp",EDGE,"E12.4.5"),sQuery(id+"F0.wireOp",EDGE,"E12.4.6"),sQuery(id+"F0.wireOp",EDGE,"E12.4.7"),sQuery(id+"F0.wireOp",EDGE,"E12.4.10"),sQuery(id+"F0.wireOp",EDGE,"E12.4.11"),sQuery(id+"F0.wireOp",EDGE,"E12.5.0"),sQuery(id+"F0.wireOp",EDGE,"E12.5.1"),sQuery(id+"F0.wireOp",EDGE,"E12.5.2"),sQuery(id+"F0.wireOp",EDGE,"E12.5.3"),sQuery(id+"F0.wireOp",EDGE,"E12.5.4"),sQuery(id+"F0.wireOp",EDGE,"E12.5.5"),sQuery(id+"F0.wireOp",EDGE,"E12.5.6"),sQuery(id+"F0.wireOp",EDGE,"E12.5.7"),sQuery(id+"F0.wireOp",EDGE,"E12.5.10"),sQuery(id+"F0.wireOp",EDGE,"E12.5.11"),sQuery(id+"F0.wireOp",EDGE,"E12.6.0"),sQuery(id+"F0.wireOp",EDGE,"E12.6.1"),sQuery(id+"F0.wireOp",EDGE,"E12.6.2"),sQuery(id+"F0.wireOp",EDGE,"E12.6.3"),sQuery(id+"F0.wireOp",EDGE,"E12.6.4"),sQuery(id+"F0.wireOp",EDGE,"E12.6.5"),sQuery(id+"F0.wireOp",EDGE,"E12.6.6"),sQuery(id+"F0.wireOp",EDGE,"E12.6.7"),sQuery(id+"F0.wireOp",EDGE,"E12.6.10"),sQuery(id+"F0.wireOp",EDGE,"E12.6.11"),sQuery(id+"F0.wireOp",EDGE,"E12.7.0"),sQuery(id+"F0.wireOp",EDGE,"E12.7.1"),sQuery(id+"F0.wireOp",EDGE,"E12.7.2"),sQuery(id+"F0.wireOp",EDGE,"E12.7.3"),sQuery(id+"F0.wireOp",EDGE,"E12.7.4"),sQuery(id+"F0.wireOp",EDGE,"E12.7.5"),sQuery(id+"F0.wireOp",EDGE,"E12.7.6"),sQuery(id+"F0.wireOp",EDGE,"E12.7.7"),sQuery(id+"F0.wireOp",EDGE,"E12.7.10"),sQuery(id+"F0.wireOp",EDGE,"E12.7.11"),sQuery(id+"F0.wireOp",EDGE,"E12.8.0"),sQuery(id+"F0.wireOp",EDGE,"E12.8.1"),sQuery(id+"F0.wireOp",EDGE,"E12.8.2"),sQuery(id+"F0.wireOp",EDGE,"E12.8.3"),sQuery(id+"F0.wireOp",EDGE,"E12.8.4"),sQuery(id+"F0.wireOp",EDGE,"E12.8.5"),sQuery(id+"F0.wireOp",EDGE,"E12.8.6"),sQuery(id+"F0.wireOp",EDGE,"E12.8.7"),sQuery(id+"F0.wireOp",EDGE,"E12.8.10"),sQuery(id+"F0.wireOp",EDGE,"E12.8.11"),sQuery(id+"F0.wireOp",EDGE,"E12.9.0"),sQuery(id+"F0.wireOp",EDGE,"E12.9.1"),sQuery(id+"F0.wireOp",EDGE,"E12.9.2"),sQuery(id+"F0.wireOp",EDGE,"E12.9.3"),sQuery(id+"F0.wireOp",EDGE,"E12.9.4"),sQuery(id+"F0.wireOp",EDGE,"E12.9.5"),sQuery(id+"F0.wireOp",EDGE,"E12.9.6"),sQuery(id+"F0.wireOp",EDGE,"E12.9.7"),sQuery(id+"F0.wireOp",EDGE,"E12.9.10"),sQuery(id+"F0.wireOp",EDGE,"E12.9.11"),sQuery(id+"F0.wireOp",EDGE,"E13.1.0"),sQuery(id+"F0.wireOp",EDGE,"E13.1.1"),sQuery(id+"F0.wireOp",EDGE,"E13.1.2"),sQuery(id+"F0.wireOp",EDGE,"E13.1.5"),sQuery(id+"F0.wireOp",EDGE,"E13.1.6"),sQuery(id+"F0.wireOp",EDGE,"E13.1.7"),sQuery(id+"F0.wireOp",EDGE,"E13.1.8"),sQuery(id+"F0.wireOp",EDGE,"E13.1.9"),sQuery(id+"F0.wireOp",EDGE,"E13.1.10"),sQuery(id+"F0.wireOp",EDGE,"E13.1.11"),sQuery(id+"F0.wireOp",EDGE,"E13.2.0"),sQuery(id+"F0.wireOp",EDGE,"E13.2.1"),sQuery(id+"F0.wireOp",EDGE,"E13.2.2"),sQuery(id+"F0.wireOp",EDGE,"E13.2.5"),sQuery(id+"F0.wireOp",EDGE,"E13.2.6"),sQuery(id+"F0.wireOp",EDGE,"E13.2.7"),sQuery(id+"F0.wireOp",EDGE,"E13.2.8"),sQuery(id+"F0.wireOp",EDGE,"E13.2.9"),sQuery(id+"F0.wireOp",EDGE,"E13.2.10"),sQuery(id+"F0.wireOp",EDGE,"E13.2.11"),sQuery(id+"F0.wireOp",EDGE,"E13.3.0"),sQuery(id+"F0.wireOp",EDGE,"E13.3.1"),sQuery(id+"F0.wireOp",EDGE,"E13.3.2"),sQuery(id+"F0.wireOp",EDGE,"E13.3.5"),sQuery(id+"F0.wireOp",EDGE,"E13.3.6"),sQuery(id+"F0.wireOp",EDGE,"E13.3.7"),sQuery(id+"F0.wireOp",EDGE,"E13.3.8"),sQuery(id+"F0.wireOp",EDGE,"E13.3.9"),sQuery(id+"F0.wireOp",EDGE,"E13.3.10"),sQuery(id+"F0.wireOp",EDGE,"E13.3.11"),sQuery(id+"F0.wireOp",EDGE,"E13.4.0"),sQuery(id+"F0.wireOp",EDGE,"E13.4.1"),sQuery(id+"F0.wireOp",EDGE,"E13.4.2"),sQuery(id+"F0.wireOp",EDGE,"E13.4.5"),sQuery(id+"F0.wireOp",EDGE,"E13.4.6"),sQuery(id+"F0.wireOp",EDGE,"E13.4.7"),sQuery(id+"F0.wireOp",EDGE,"E13.4.8"),sQuery(id+"F0.wireOp",EDGE,"E13.4.9"),sQuery(id+"F0.wireOp",EDGE,"E13.4.10"),sQuery(id+"F0.wireOp",EDGE,"E13.4.11"),sQuery(id+"F0.wireOp",EDGE,"E13.5.0"),sQuery(id+"F0.wireOp",EDGE,"E13.5.1"),sQuery(id+"F0.wireOp",EDGE,"E13.5.2"),sQuery(id+"F0.wireOp",EDGE,"E13.5.5"),sQuery(id+"F0.wireOp",EDGE,"E13.5.6"),sQuery(id+"F0.wireOp",EDGE,"E13.5.7"),sQuery(id+"F0.wireOp",EDGE,"E13.5.8"),sQuery(id+"F0.wireOp",EDGE,"E13.5.9"),sQuery(id+"F0.wireOp",EDGE,"E13.5.10"),sQuery(id+"F0.wireOp",EDGE,"E13.5.11"),sQuery(id+"F0.wireOp",EDGE,"E13.6.0"),sQuery(id+"F0.wireOp",EDGE,"E13.6.1"),sQuery(id+"F0.wireOp",EDGE,"E13.6.2"),sQuery(id+"F0.wireOp",EDGE,"E13.6.5"),sQuery(id+"F0.wireOp",EDGE,"E13.6.6"),sQuery(id+"F0.wireOp",EDGE,"E13.6.7"),sQuery(id+"F0.wireOp",EDGE,"E13.6.8"),sQuery(id+"F0.wireOp",EDGE,"E13.6.9"),sQuery(id+"F0.wireOp",EDGE,"E13.6.10"),sQuery(id+"F0.wireOp",EDGE,"E13.6.11"),sQuery(id+"F0.wireOp",EDGE,"E13.7.0"),sQuery(id+"F0.wireOp",EDGE,"E13.7.1"),sQuery(id+"F0.wireOp",EDGE,"E13.7.2"),sQuery(id+"F0.wireOp",EDGE,"E13.7.5"),sQuery(id+"F0.wireOp",EDGE,"E13.7.6"),sQuery(id+"F0.wireOp",EDGE,"E13.7.7"),sQuery(id+"F0.wireOp",EDGE,"E13.7.8"),sQuery(id+"F0.wireOp",EDGE,"E13.7.9"),sQuery(id+"F0.wireOp",EDGE,"E13.7.10"),sQuery(id+"F0.wireOp",EDGE,"E13.7.11"),sQuery(id+"F0.wireOp",EDGE,"E13.8.0"),sQuery(id+"F0.wireOp",EDGE,"E13.8.1"),sQuery(id+"F0.wireOp",EDGE,"E13.8.2"),sQuery(id+"F0.wireOp",EDGE,"E13.8.5"),sQuery(id+"F0.wireOp",EDGE,"E13.8.6"),sQuery(id+"F0.wireOp",EDGE,"E13.8.7"),sQuery(id+"F0.wireOp",EDGE,"E13.8.8"),sQuery(id+"F0.wireOp",EDGE,"E13.8.9"),sQuery(id+"F0.wireOp",EDGE,"E13.8.10"),sQuery(id+"F0.wireOp",EDGE,"E13.8.11"),sQuery(id+"F0.wireOp",EDGE,"E3"),sQuery(id+"F0.wireOp",EDGE,"E2"),sQuery(id+"F0.wireOp",EDGE,"E1"),sQuery(id+"F0.wireOp",EDGE,"E4"),sQuery(id+"F0.wireOp",EDGE,"E8"),sQuery(id+"F0.wireOp",EDGE,"E5"),sQuery(id+"F0.wireOp",EDGE,"E11"),sQuery(id+"F0.wireOp",EDGE,"E6"),sQuery(id+"F0.wireOp",EDGE,"E7"),sQuery(id+"F0.wireOp",EDGE,"E10"),sQuery(id+"F0.wireOp",EDGE,"E14"),subQ0,sQuery(id+"F0.wireOp",EDGE,"E20.trimOffspring"),sQuery(id+"F0.wireOp",EDGE,"E21.trimOffspring"),sQuery(id+"F0.wireOp",EDGE,"E22.trimOffspring"),sQuery(id+"F0.wireOp",EDGE,"E23.trimOffspring"),sQuery(id+"F0.wireOp",EDGE,"E24.trimOffspring"),sQuery(id+"F0.wireOp",EDGE,"E25.trimOffspring"),sQuery(id+"F0.wireOp",EDGE,"E26.trimOffspring"),sQuery(id+"F0.wireOp",EDGE,"E27.trimOffspring"),sQuery(id+"F0.wireOp",EDGE,"E28.trimOffspring"),sQuery(id+"F0.wireOp",EDGE,"E29.trimOffspring"),sQuery(id+"F0.wireOp",EDGE,"E30.trimOffspring"),sQuery(id+"F0.wireOp",EDGE,"E31.trimOffspring"),sQuery(id+"F0.wireOp",EDGE,"E32.trimOffspring"),sQuery(id+"F0.wireOp",EDGE,"E33.trimOffspring"),sQuery(id+"F0.wireOp",EDGE,"E34.trimOffspring"),sQuery(id+"F0.wireOp",EDGE,"E35.trimOffspring"),sQuery(id+"F0.wireOp",EDGE,"E36.trimOffspring"),sQuery(id+"F0.wireOp",EDGE,"E37")])],"isStart":false})}),makeQuery(id+"F4.opExtrude","CAP_FACE",FACE,{"disambiguationData":[OSD([subQ0,sQuery(id+"F3.wireOp",EDGE,"E42"),sQuery(id+"F3.wireOp",EDGE,"E43.0"),sQuery(id+"F3.wireOp",EDGE,"E46.trimOffspring"),sQuery(id+"F3.wireOp",EDGE,"E47.trimOffspring"),sQuery(id+"F3.wireOp",EDGE,"E48.trimOffspring"),sQuery(id+"F3.wireOp",EDGE,"E49.trimOffspring"),sQuery(id+"F3.wireOp",EDGE,"E50.1.0"),sQuery(id+"F3.wireOp",EDGE,"E50.1.1"),sQuery(id+"F3.wireOp",EDGE,"E50.1.5"),sQuery(id+"F3.wireOp",EDGE,"E50.1.6"),sQuery(id+"F3.wireOp",EDGE,"E50.1.8"),sQuery(id+"F3.wireOp",EDGE,"E50.1.10"),sQuery(id+"F3.wireOp",EDGE,"E50.2.0"),sQuery(id+"F3.wireOp",EDGE,"E50.2.1"),sQuery(id+"F3.wireOp",EDGE,"E50.2.5"),sQuery(id+"F3.wireOp",EDGE,"E50.2.6"),sQuery(id+"F3.wireOp",EDGE,"E50.2.8"),sQuery(id+"F3.wireOp",EDGE,"E50.2.10"),sQuery(id+"F3.wireOp",EDGE,"E50.3.0"),sQuery(id+"F3.wireOp",EDGE,"E50.3.1"),sQuery(id+"F3.wireOp",EDGE,"E50.3.5"),sQuery(id+"F3.wireOp",EDGE,"E50.3.6"),sQuery(id+"F3.wireOp",EDGE,"E50.3.8"),sQuery(id+"F3.wireOp",EDGE,"E50.3.10"),sQuery(id+"F3.wireOp",EDGE,"E50.4.0"),sQuery(id+"F3.wireOp",EDGE,"E50.4.1"),sQuery(id+"F3.wireOp",EDGE,"E50.4.5"),sQuery(id+"F3.wireOp",EDGE,"E50.4.6"),sQuery(id+"F3.wireOp",EDGE,"E50.4.8"),sQuery(id+"F3.wireOp",EDGE,"E50.4.10"),sQuery(id+"F3.wireOp",EDGE,"E50.5.0"),sQuery(id+"F3.wireOp",EDGE,"E50.5.1"),sQuery(id+"F3.wireOp",EDGE,"E50.5.5"),sQuery(id+"F3.wireOp",EDGE,"E50.5.6"),sQuery(id+"F3.wireOp",EDGE,"E50.5.8"),sQuery(id+"F3.wireOp",EDGE,"E50.5.10"),sQuery(id+"F3.wireOp",EDGE,"E50.6.0"),sQuery(id+"F3.wireOp",EDGE,"E50.6.1"),sQuery(id+"F3.wireOp",EDGE,"E50.6.5"),sQuery(id+"F3.wireOp",EDGE,"E50.6.6"),sQuery(id+"F3.wireOp",EDGE,"E50.6.8"),sQuery(id+"F3.wireOp",EDGE,"E50.6.10"),sQuery(id+"F3.wireOp",EDGE,"E50.7.0"),sQuery(id+"F3.wireOp",EDGE,"E50.7.1"),sQuery(id+"F3.wireOp",EDGE,"E50.7.5"),sQuery(id+"F3.wireOp",EDGE,"E50.7.6"),sQuery(id+"F3.wireOp",EDGE,"E50.7.8"),sQuery(id+"F3.wireOp",EDGE,"E50.7.10"),sQuery(id+"F3.wireOp",EDGE,"E50.8.0"),sQuery(id+"F3.wireOp",EDGE,"E50.8.1"),sQuery(id+"F3.wireOp",EDGE,"E50.8.5"),sQuery(id+"F3.wireOp",EDGE,"E50.8.6"),sQuery(id+"F3.wireOp",EDGE,"E50.8.8"),sQuery(id+"F3.wireOp",EDGE,"E50.8.10"),sQuery(id+"F3.wireOp",EDGE,"E51.trimOffspring"),sQuery(id+"F3.wireOp",EDGE,"E52.trimOffspring"),sQuery(id+"F3.wireOp",EDGE,"E53.trimOffspring"),sQuery(id+"F3.wireOp",EDGE,"E54.trimOffspring"),sQuery(id+"F3.wireOp",EDGE,"E55.trimOffspring"),sQuery(id+"F3.wireOp",EDGE,"E56.trimOffspring"),sQuery(id+"F3.wireOp",EDGE,"E57.trimOffspring"),sQuery(id+"F3.wireOp",EDGE,"E58.trimOffspring"),sQuery(id+"F3.wireOp",EDGE,"E59.trimOffspring"),sQuery(id+"F3.wireOp",EDGE,"E60.trimOffspring"),sQuery(id+"F3.wireOp",EDGE,"E61.trimOffspring"),sQuery(id+"F3.wireOp",EDGE,"E62.trimOffspring"),sQuery(id+"F3.wireOp",EDGE,"E63.trimOffspring"),sQuery(id+"F3.wireOp",EDGE,"E64.trimOffspring"),sQuery(id+"F3.wireOp",EDGE,"E65.trimOffspring"),sQuery(id+"F3.wireOp",EDGE,"E66.trimOffspring"),sQuery(id+"F3.wireOp",EDGE,"E67.trimOffspring"),sQuery(id+"F3.wireOp",EDGE,"E68.trimOffspring"),sQuery(id+"F3.wireOp",EDGE,"E69.trimOffspring"),sQuery(id+"F3.wireOp",EDGE,"E70.trimOffspring"),sQuery(id+"F3.wireOp",EDGE,"E71.trimOffspring"),sQuery(id+"F3.wireOp",EDGE,"E72.trimOffspring"),sQuery(id+"F3.wireOp",EDGE,"E73.trimOffspring"),sQuery(id+"F3.wireOp",EDGE,"E74.trimOffspring"),sQuery(id+"F3.wireOp",EDGE,"E75.trimOffspring"),sQuery(id+"F3.wireOp",EDGE,"E76.trimOffspring"),sQuery(id+"F3.wireOp",EDGE,"E77.trimOffspring"),sQuery(id+"F3.wireOp",EDGE,"E78.trimOffspring"),sQuery(id+"F3.wireOp",EDGE,"E79.trimOffspring"),sQuery(id+"F3.wireOp",EDGE,"E80.trimOffspring"),sQuery(id+"F3.wireOp",EDGE,"E81.trimOffspring"),sQuery(id+"F3.wireOp",EDGE,"E82.trimOffspring"),sQuery(id+"F3.wireOp",EDGE,"E83.trimOffspring"),sQuery(id+"F3.wireOp",EDGE,"E84.trimOffspring"),sQuery(id+"F3.wireOp",EDGE,"E85.trimOffspring"),sQuery(id+"F3.wireOp",EDGE,"E86.trimOffspring")])],"isStart":false})]}),makeQuery(id+"F6.opExtrude","CAP_FACE",FACE,{"disambiguationData":[OSD([sQuery(id+"F5.wireOp",EDGE,"E88"),sQuery(id+"F5.wireOp",EDGE,"E89"),sQuery(id+"F5.wireOp",EDGE,"E90"),sQuery(id+"F5.wireOp",EDGE,"E91.0"),sQuery(id+"F5.wireOp",EDGE,"E92"),sQuery(id+"F5.wireOp",EDGE,"E93"),sQuery(id+"F5.wireOp",EDGE,"E94.trimOffspring"),sQuery(id+"F5.wireOp",EDGE,"E95.trimOffspring"),sQuery(id+"F5.wireOp",EDGE,"E96.trimOffspring"),sQuery(id+"F5.wireOp",EDGE,"E97.trimOffspring"),sQuery(id+"F5.wireOp",EDGE,"E98.1.0"),sQuery(id+"F5.wireOp",EDGE,"E98.1.1"),sQuery(id+"F5.wireOp",EDGE,"E98.1.5"),sQuery(id+"F5.wireOp",EDGE,"E98.1.6"),sQuery(id+"F5.wireOp",EDGE,"E98.1.7"),sQuery(id+"F5.wireOp",EDGE,"E98.1.8"),sQuery(id+"F5.wireOp",EDGE,"E98.1.9"),sQuery(id+"F5.wireOp",EDGE,"E98.1.10"),sQuery(id+"F5.wireOp",EDGE,"E98.2.0"),sQuery(id+"F5.wireOp",EDGE,"E98.2.1"),sQuery(id+"F5.wireOp",EDGE,"E98.2.5"),sQuery(id+"F5.wireOp",EDGE,"E98.2.6"),sQuery(id+"F5.wireOp",EDGE,"E98.2.7"),sQuery(id+"F5.wireOp",EDGE,"E98.2.8"),sQuery(id+"F5.wireOp",EDGE,"E98.2.9"),sQuery(id+"F5.wireOp",EDGE,"E98.2.10"),sQuery(id+"F5.wireOp",EDGE,"E98.3.0"),sQuery(id+"F5.wireOp",EDGE,"E98.3.1"),sQuery(id+"F5.wireOp",EDGE,"E98.3.5"),sQuery(id+"F5.wireOp",EDGE,"E98.3.6"),sQuery(id+"F5.wireOp",EDGE,"E98.3.7"),sQuery(id+"F5.wireOp",EDGE,"E98.3.8"),sQuery(id+"F5.wireOp",EDGE,"E98.3.9"),sQuery(id+"F5.wireOp",EDGE,"E98.3.10"),sQuery(id+"F5.wireOp",EDGE,"E98.4.0"),sQuery(id+"F5.wireOp",EDGE,"E98.4.1"),sQuery(id+"F5.wireOp",EDGE,"E98.4.5"),sQuery(id+"F5.wireOp",EDGE,"E98.4.6"),sQuery(id+"F5.wireOp",EDGE,"E98.4.7"),sQuery(id+"F5.wireOp",EDGE,"E98.4.8"),sQuery(id+"F5.wireOp",EDGE,"E98.4.9"),sQuery(id+"F5.wireOp",EDGE,"E98.4.10"),sQuery(id+"F5.wireOp",EDGE,"E98.5.0"),sQuery(id+"F5.wireOp",EDGE,"E98.5.1"),sQuery(id+"F5.wireOp",EDGE,"E98.5.5"),sQuery(id+"F5.wireOp",EDGE,"E98.5.6"),sQuery(id+"F5.wireOp",EDGE,"E98.5.7"),sQuery(id+"F5.wireOp",EDGE,"E98.5.8"),sQuery(id+"F5.wireOp",EDGE,"E98.5.9"),sQuery(id+"F5.wireOp",EDGE,"E98.5.10"),sQuery(id+"F5.wireOp",EDGE,"E98.6.0"),sQuery(id+"F5.wireOp",EDGE,"E98.6.1"),sQuery(id+"F5.wireOp",EDGE,"E98.6.5"),sQuery(id+"F5.wireOp",EDGE,"E98.6.6"),sQuery(id+"F5.wireOp",EDGE,"E98.6.7"),sQuery(id+"F5.wireOp",EDGE,"E98.6.8"),sQuery(id+"F5.wireOp",EDGE,"E98.6.9"),sQuery(id+"F5.wireOp",EDGE,"E98.6.10"),sQuery(id+"F5.wireOp",EDGE,"E98.7.0"),sQuery(id+"F5.wireOp",EDGE,"E98.7.1"),sQuery(id+"F5.wireOp",EDGE,"E98.7.5"),sQuery(id+"F5.wireOp",EDGE,"E98.7.6"),sQuery(id+"F5.wireOp",EDGE,"E98.7.7"),sQuery(id+"F5.wireOp",EDGE,"E98.7.8"),sQuery(id+"F5.wireOp",EDGE,"E98.7.9"),sQuery(id+"F5.wireOp",EDGE,"E98.7.10"),sQuery(id+"F5.wireOp",EDGE,"E98.8.0"),sQuery(id+"F5.wireOp",EDGE,"E98.8.1"),sQuery(id+"F5.wireOp",EDGE,"E98.8.5"),sQuery(id+"F5.wireOp",EDGE,"E98.8.6"),sQuery(id+"F5.wireOp",EDGE,"E98.8.7"),sQuery(id+"F5.wireOp",EDGE,"E98.8.8"),sQuery(id+"F5.wireOp",EDGE,"E98.8.9"),sQuery(id+"F5.wireOp",EDGE,"E98.8.10"),sQuery(id+"F5.wireOp",EDGE,"E99.trimOffspring"),sQuery(id+"F5.wireOp",EDGE,"E100.trimOffspring"),sQuery(id+"F5.wireOp",EDGE,"E101.trimOffspring"),sQuery(id+"F5.wireOp",EDGE,"E102.trimOffspring"),sQuery(id+"F5.wireOp",EDGE,"E103.trimOffspring"),sQuery(id+"F5.wireOp",EDGE,"E104.trimOffspring"),sQuery(id+"F5.wireOp",EDGE,"E105.trimOffspring"),sQuery(id+"F5.wireOp",EDGE,"E106.trimOffspring"),sQuery(id+"F5.wireOp",EDGE,"E107.trimOffspring"),sQuery(id+"F5.wireOp",EDGE,"E108.trimOffspring"),sQuery(id+"F5.wireOp",EDGE,"E109.trimOffspring"),sQuery(id+"F5.wireOp",EDGE,"E110.trimOffspring"),sQuery(id+"F5.wireOp",EDGE,"E111.trimOffspring"),sQuery(id+"F5.wireOp",EDGE,"E112.trimOffspring"),sQuery(id+"F5.wireOp",EDGE,"E113.trimOffspring"),sQuery(id+"F5.wireOp",EDGE,"E114.trimOffspring"),sQuery(id+"F5.wireOp",EDGE,"E115.trimOffspring"),sQuery(id+"F5.wireOp",EDGE,"E116.trimOffspring"),sQuery(id+"F5.wireOp",EDGE,"E117.trimOffspring"),sQuery(id+"F5.wireOp",EDGE,"E118.trimOffspring"),sQuery(id+"F5.wireOp",EDGE,"E119.trimOffspring"),sQuery(id+"F5.wireOp",EDGE,"E120.trimOffspring"),sQuery(id+"F5.wireOp",EDGE,"E121.trimOffspring"),sQuery(id+"F5.wireOp",EDGE,"E122.trimOffspring"),sQuery(id+"F5.wireOp",EDGE,"E123.trimOffspring"),sQuery(id+"F5.wireOp",EDGE,"E124.trimOffspring"),sQuery(id+"F5.wireOp",EDGE,"E125.trimOffspring"),sQuery(id+"F5.wireOp",EDGE,"E126.trimOffspring"),sQuery(id+"F5.wireOp",EDGE,"E127.trimOffspring"),sQuery(id+"F5.wireOp",EDGE,"E128.trimOffspring"),sQuery(id+"F5.wireOp",EDGE,"E129.trimOffspring"),sQuery(id+"F5.wireOp",EDGE,"E130.trimOffspring"),sQuery(id+"F5.wireOp",EDGE,"E131.trimOffspring"),sQuery(id+"F5.wireOp",EDGE,"E132.trimOffspring"),sQuery(id+"F5.wireOp",EDGE,"E133.trimOffspring"),sQuery(id+"F5.wireOp",EDGE,"E134.trimOffspring")])],"isStart":true})]}),makeQuery(id+"F8.opExtrude","CAP_FACE",FACE,{"disambiguationData":[OSD([sQuery(id+"F7.wireOp",EDGE,"E135"),sQuery(id+"F7.wireOp",EDGE,"E137")])],"isStart":true})]});}
            var sketch = newSketch(context, id + "F9", { "sketchPlane" : qUnion([Q0])});
            skCircle(sketch, "E138", {"center": v(0, 0) * mm, "radius": 54.45 * mm});
            skCircle(sketch, "E139", {"center": v(0, 0) * mm, "radius": 51.6 * mm});
            skSolve(sketch);
        }
        {
            var Q0;
            Q0 = qSketchRegion(id + "F9", true);
            extrude(context, id + "F10", {"entities" : qUnion([Q0]), "operationType" : NewBodyOperationType.REMOVE, "oppositeDirection" : true, "depth" : 25.4 * mm});
        }
        {
            var Q0;
            {var subQ0=sQuery(id+"F5.wireOp",EDGE,"E98.7.0");var subQ1=sQuery(id+"F5.wireOp",EDGE,"E98.6.0");var subQ2=sQuery(id+"F5.wireOp",EDGE,"E134.trimOffspring");var subQ3=sQuery(id+"F5.wireOp",EDGE,"E98.5.1");var subQ4=sQuery(id+"F5.wireOp",EDGE,"E98.3.0");var subQ5=sQuery(id+"F5.wireOp",EDGE,"E110.trimOffspring");var subQ6=sQuery(id+"F5.wireOp",EDGE,"E98.2.5");var subQ7=sQuery(id+"F5.wireOp",EDGE,"E98.2.0");var subQ8=sQuery(id+"F3.wireOp",EDGE,"E80.trimOffspring");var subQ9=sQuery(id+"F5.wireOp",EDGE,"E102.trimOffspring");var subQ10=sQuery(id+"F5.wireOp",EDGE,"E98.1.5");var subQ11=sQuery(id+"F5.wireOp",EDGE,"E98.4.0");var subQ12=sQuery(id+"F5.wireOp",EDGE,"E118.trimOffspring");var subQ13=sQuery(id+"F5.wireOp",EDGE,"E96.trimOffspring");var subQ14=sQuery(id+"F5.wireOp",EDGE,"E98.8.1");var subQ15=sQuery(id+"F5.wireOp",EDGE,"E94.trimOffspring");var subQ16=sQuery(id+"F5.wireOp",EDGE,"E90");var subQ17=sQuery(id+"F5.wireOp",EDGE,"E98.6.1");var subQ18=sQuery(id+"F3.wireOp",EDGE,"E42");var subQ19=sQuery(id+"F3.wireOp",EDGE,"E85.trimOffspring");var subQ20=sQuery(id+"F3.wireOp",EDGE,"E84.trimOffspring");var subQ21=sQuery(id+"F5.wireOp",EDGE,"E98.8.10");var subQ22=sQuery(id+"F3.wireOp",EDGE,"E83.trimOffspring");var subQ23=sQuery(id+"F3.wireOp",EDGE,"E82.trimOffspring");var subQ24=sQuery(id+"F3.wireOp",EDGE,"E81.trimOffspring");var subQ25=sQuery(id+"F3.wireOp",EDGE,"E79.trimOffspring");var subQ26=sQuery(id+"F3.wireOp",EDGE,"E76.trimOffspring");var subQ27=sQuery(id+"F5.wireOp",EDGE,"E98.7.10");var subQ28=sQuery(id+"F3.wireOp",EDGE,"E71.trimOffspring");var subQ29=sQuery(id+"F3.wireOp",EDGE,"E68.trimOffspring");var subQ30=sQuery(id+"F5.wireOp",EDGE,"E114.trimOffspring");var subQ31=sQuery(id+"F3.wireOp",EDGE,"E67.trimOffspring");var subQ32=sQuery(id+"F5.wireOp",EDGE,"E98.1.0");var subQ33=sQuery(id+"F5.wireOp",EDGE,"E98.7.1");var subQ34=sQuery(id+"F3.wireOp",EDGE,"E50.1.0");var subQ35=sQuery(id+"F3.wireOp",EDGE,"E66.trimOffspring");var subQ36=sQuery(id+"F7.wireOp",EDGE,"E137");var subQ37=sQuery(id+"F3.wireOp",EDGE,"E65.trimOffspring");var subQ38=sQuery(id+"F3.wireOp",EDGE,"E64.trimOffspring");var subQ39=sQuery(id+"F3.wireOp",EDGE,"E63.trimOffspring");var subQ40=sQuery(id+"F3.wireOp",EDGE,"E61.trimOffspring");var subQ41=sQuery(id+"F5.wireOp",EDGE,"E119.trimOffspring");var subQ42=sQuery(id+"F5.wireOp",EDGE,"E98.2.1");var subQ43=sQuery(id+"F3.wireOp",EDGE,"E50.5.0");var subQ44=sQuery(id+"F3.wireOp",EDGE,"E86.trimOffspring");var subQ45=sQuery(id+"F5.wireOp",EDGE,"E98.4.1");var subQ46=sQuery(id+"F3.wireOp",EDGE,"E50.2.5");var subQ47=sQuery(id+"F3.wireOp",EDGE,"E62.trimOffspring");var subQ48=sQuery(id+"F5.wireOp",EDGE,"E98.8.5");var subQ49=sQuery(id+"F3.wireOp",EDGE,"E50.4.10");var subQ50=sQuery(id+"F3.wireOp",EDGE,"E50.4.5");var subQ51=sQuery(id+"F5.wireOp",EDGE,"E98.7.5");var subQ52=sQuery(id+"F3.wireOp",EDGE,"E50.4.1");var subQ53=sQuery(id+"F3.wireOp",EDGE,"E72.trimOffspring");var subQ54=sQuery(id+"F3.wireOp",EDGE,"E50.6.10");var subQ55=sQuery(id+"F5.wireOp",EDGE,"E133.trimOffspring");var subQ56=sQuery(id+"F3.wireOp",EDGE,"E50.8.5");var subQ57=sQuery(id+"F3.wireOp",EDGE,"E50.4.0");var subQ58=sQuery(id+"F5.wireOp",EDGE,"E98.1.10");var subQ59=sQuery(id+"F3.wireOp",EDGE,"E70.trimOffspring");var subQ60=sQuery(id+"F5.wireOp",EDGE,"E101.trimOffspring");var subQ61=sQuery(id+"F3.wireOp",EDGE,"E50.8.1");var subQ62=sQuery(id+"F3.wireOp",EDGE,"E50.3.10");var subQ63=sQuery(id+"F3.wireOp",EDGE,"E50.8.0");var subQ64=sQuery(id+"F3.wireOp",EDGE,"E50.5.1");var subQ65=sQuery(id+"F3.wireOp",EDGE,"E73.trimOffspring");var subQ66=sQuery(id+"F3.wireOp",EDGE,"E50.7.0");var subQ67=sQuery(id+"F3.wireOp",EDGE,"E50.2.10");var subQ68=sQuery(id+"F3.wireOp",EDGE,"E75.trimOffspring");var subQ69=sQuery(id+"F3.wireOp",EDGE,"E50.1.5");var subQ70=sQuery(id+"F3.wireOp",EDGE,"E48.trimOffspring");var subQ71=sQuery(id+"F3.wireOp",EDGE,"E50.2.1");var subQ72=sQuery(id+"F3.wireOp",EDGE,"E47.trimOffspring");var subQ73=sQuery(id+"F3.wireOp",EDGE,"E50.1.10");var subQ74=sQuery(id+"F3.wireOp",EDGE,"E77.trimOffspring");var subQ75=sQuery(id+"F3.wireOp",EDGE,"E78.trimOffspring");var subQ76=sQuery(id+"F3.wireOp",EDGE,"E50.3.5");var subQ77=sQuery(id+"F3.wireOp",EDGE,"E50.2.0");var subQ78=sQuery(id+"F3.wireOp",EDGE,"E52.trimOffspring");var subQ79=sQuery(id+"F5.wireOp",EDGE,"E130.trimOffspring");var subQ80=sQuery(id+"F3.wireOp",EDGE,"E50.1.1");var subQ81=sQuery(id+"F3.wireOp",EDGE,"E50.5.5");var subQ82=sQuery(id+"F5.wireOp",EDGE,"E112.trimOffspring");var subQ83=sQuery(id+"F3.wireOp",EDGE,"E50.3.1");var subQ84=sQuery(id+"F3.wireOp",EDGE,"E50.5.10");var subQ85=sQuery(id+"F3.wireOp",EDGE,"E50.6.0");var subQ86=sQuery(id+"F3.wireOp",EDGE,"E50.7.5");var subQ87=sQuery(id+"F3.wireOp",EDGE,"E69.trimOffspring");var subQ88=sQuery(id+"F5.wireOp",EDGE,"E127.trimOffspring");var subQ89=sQuery(id+"F3.wireOp",EDGE,"E57.trimOffspring");var subQ90=sQuery(id+"F5.wireOp",EDGE,"E111.trimOffspring");var subQ91=sQuery(id+"F5.wireOp",EDGE,"E98.5.0");var subQ92=sQuery(id+"F5.wireOp",EDGE,"E126.trimOffspring");var subQ93=sQuery(id+"F3.wireOp",EDGE,"E50.6.1");var subQ94=sQuery(id+"F3.wireOp",EDGE,"E46.trimOffspring");var subQ95=sQuery(id+"F3.wireOp",EDGE,"E58.trimOffspring");var subQ96=sQuery(id+"F3.wireOp",EDGE,"E59.trimOffspring");var subQ97=sQuery(id+"F5.wireOp",EDGE,"E98.3.1");var subQ98=sQuery(id+"F3.wireOp",EDGE,"E50.6.5");var subQ99=sQuery(id+"F3.wireOp",EDGE,"E50.7.10");var subQ100=sQuery(id+"F5.wireOp",EDGE,"E122.trimOffspring");var subQ101=sQuery(id+"F3.wireOp",EDGE,"E60.trimOffspring");var subQ102=sQuery(id+"F5.wireOp",EDGE,"E106.trimOffspring");var subQ103=sQuery(id+"F3.wireOp",EDGE,"E74.trimOffspring");var subQ104=sQuery(id+"F3.wireOp",EDGE,"E50.3.0");var subQ105=sQuery(id+"F3.wireOp",EDGE,"E50.7.1");var subQ106=sQuery(id+"F3.wireOp",EDGE,"E50.8.10");var subQ107=sQuery(id+"F5.wireOp",EDGE,"E98.1.1");var subQ108=sQuery(id+"F3.wireOp",EDGE,"E51.trimOffspring");var subQ109=sQuery(id+"F3.wireOp",EDGE,"E53.trimOffspring");var subQ110=sQuery(id+"F5.wireOp",EDGE,"E104.trimOffspring");var subQ111=sQuery(id+"F5.wireOp",EDGE,"E98.2.10");var subQ112=sQuery(id+"F5.wireOp",EDGE,"E109.trimOffspring");var subQ113=sQuery(id+"F3.wireOp",EDGE,"E54.trimOffspring");var subQ114=sQuery(id+"F5.wireOp",EDGE,"E117.trimOffspring");var subQ115=sQuery(id+"F5.wireOp",EDGE,"E95.trimOffspring");var subQ116=sQuery(id+"F3.wireOp",EDGE,"E55.trimOffspring");var subQ117=sQuery(id+"F3.wireOp",EDGE,"E56.trimOffspring");var subQ118=sQuery(id+"F5.wireOp",EDGE,"E98.8.0");var subQ119=sQuery(id+"F5.wireOp",EDGE,"E99.trimOffspring");var subQ120=sQuery(id+"F5.wireOp",EDGE,"E100.trimOffspring");var subQ121=sQuery(id+"F5.wireOp",EDGE,"E103.trimOffspring");var subQ122=sQuery(id+"F5.wireOp",EDGE,"E105.trimOffspring");var subQ123=sQuery(id+"F5.wireOp",EDGE,"E107.trimOffspring");var subQ124=sQuery(id+"F5.wireOp",EDGE,"E108.trimOffspring");var subQ125=sQuery(id+"F5.wireOp",EDGE,"E113.trimOffspring");var subQ126=sQuery(id+"F5.wireOp",EDGE,"E115.trimOffspring");var subQ127=sQuery(id+"F5.wireOp",EDGE,"E116.trimOffspring");var subQ128=sQuery(id+"F5.wireOp",EDGE,"E120.trimOffspring");var subQ129=sQuery(id+"F5.wireOp",EDGE,"E121.trimOffspring");var subQ130=sQuery(id+"F5.wireOp",EDGE,"E123.trimOffspring");var subQ131=sQuery(id+"F5.wireOp",EDGE,"E124.trimOffspring");var subQ132=sQuery(id+"F5.wireOp",EDGE,"E125.trimOffspring");var subQ133=sQuery(id+"F5.wireOp",EDGE,"E128.trimOffspring");var subQ134=sQuery(id+"F5.wireOp",EDGE,"E129.trimOffspring");var subQ135=sQuery(id+"F5.wireOp",EDGE,"E131.trimOffspring");var subQ136=sQuery(id+"F5.wireOp",EDGE,"E132.trimOffspring");var subQ137=sQuery(id+"F0.wireOp",EDGE,"E15");Q0=makeQuery(id+"F10.boolean.opBoolean","SPLIT",FACE,{"disambiguationData":[TD([makeQuery(id+"F4.opExtrude","SWEPT_FACE",FACE,{"disambiguationData":[OSD([subQ18])]})])],"derivedFrom":makeQuery(id+"F8.boolean.opBoolean","MERGE",FACE,{"derivedFrom":[makeQuery(id+"F6.boolean.opBoolean","MERGE",FACE,{"derivedFrom":[makeQuery(id+"F4.boolean.opBoolean","MERGE",FACE,{"derivedFrom":[makeQuery(id+"F2.opChamfer","SPLIT",FACE,{"disambiguationData":[OD(18.0)],"derivedFrom":makeQuery(id+"F1.opExtrude","CAP_FACE",FACE,{"disambiguationData":[OSD([sQuery(id+"F0.wireOp",EDGE,"E12.1.0"),sQuery(id+"F0.wireOp",EDGE,"E12.1.1"),sQuery(id+"F0.wireOp",EDGE,"E12.1.2"),sQuery(id+"F0.wireOp",EDGE,"E12.1.3"),sQuery(id+"F0.wireOp",EDGE,"E12.1.4"),sQuery(id+"F0.wireOp",EDGE,"E12.1.5"),sQuery(id+"F0.wireOp",EDGE,"E12.1.6"),sQuery(id+"F0.wireOp",EDGE,"E12.1.7"),sQuery(id+"F0.wireOp",EDGE,"E12.1.10"),sQuery(id+"F0.wireOp",EDGE,"E12.1.11"),sQuery(id+"F0.wireOp",EDGE,"E12.2.0"),sQuery(id+"F0.wireOp",EDGE,"E12.2.1"),sQuery(id+"F0.wireOp",EDGE,"E12.2.2"),sQuery(id+"F0.wireOp",EDGE,"E12.2.3"),sQuery(id+"F0.wireOp",EDGE,"E12.2.4"),sQuery(id+"F0.wireOp",EDGE,"E12.2.5"),sQuery(id+"F0.wireOp",EDGE,"E12.2.6"),sQuery(id+"F0.wireOp",EDGE,"E12.2.7"),sQuery(id+"F0.wireOp",EDGE,"E12.2.10"),sQuery(id+"F0.wireOp",EDGE,"E12.2.11"),sQuery(id+"F0.wireOp",EDGE,"E12.3.0"),sQuery(id+"F0.wireOp",EDGE,"E12.3.1"),sQuery(id+"F0.wireOp",EDGE,"E12.3.2"),sQuery(id+"F0.wireOp",EDGE,"E12.3.3"),sQuery(id+"F0.wireOp",EDGE,"E12.3.4"),sQuery(id+"F0.wireOp",EDGE,"E12.3.5"),sQuery(id+"F0.wireOp",EDGE,"E12.3.6"),sQuery(id+"F0.wireOp",EDGE,"E12.3.7"),sQuery(id+"F0.wireOp",EDGE,"E12.3.10"),sQuery(id+"F0.wireOp",EDGE,"E12.3.11"),sQuery(id+"F0.wireOp",EDGE,"E12.4.0"),sQuery(id+"F0.wireOp",EDGE,"E12.4.1"),sQuery(id+"F0.wireOp",EDGE,"E12.4.2"),sQuery(id+"F0.wireOp",EDGE,"E12.4.3"),sQuery(id+"F0.wireOp",EDGE,"E12.4.4"),sQuery(id+"F0.wireOp",EDGE,"E12.4.5"),sQuery(id+"F0.wireOp",EDGE,"E12.4.6"),sQuery(id+"F0.wireOp",EDGE,"E12.4.7"),sQuery(id+"F0.wireOp",EDGE,"E12.4.10"),sQuery(id+"F0.wireOp",EDGE,"E12.4.11"),sQuery(id+"F0.wireOp",EDGE,"E12.5.0"),sQuery(id+"F0.wireOp",EDGE,"E12.5.1"),sQuery(id+"F0.wireOp",EDGE,"E12.5.2"),sQuery(id+"F0.wireOp",EDGE,"E12.5.3"),sQuery(id+"F0.wireOp",EDGE,"E12.5.4"),sQuery(id+"F0.wireOp",EDGE,"E12.5.5"),sQuery(id+"F0.wireOp",EDGE,"E12.5.6"),sQuery(id+"F0.wireOp",EDGE,"E12.5.7"),sQuery(id+"F0.wireOp",EDGE,"E12.5.10"),sQuery(id+"F0.wireOp",EDGE,"E12.5.11"),sQuery(id+"F0.wireOp",EDGE,"E12.6.0"),sQuery(id+"F0.wireOp",EDGE,"E12.6.1"),sQuery(id+"F0.wireOp",EDGE,"E12.6.2"),sQuery(id+"F0.wireOp",EDGE,"E12.6.3"),sQuery(id+"F0.wireOp",EDGE,"E12.6.4"),sQuery(id+"F0.wireOp",EDGE,"E12.6.5"),sQuery(id+"F0.wireOp",EDGE,"E12.6.6"),sQuery(id+"F0.wireOp",EDGE,"E12.6.7"),sQuery(id+"F0.wireOp",EDGE,"E12.6.10"),sQuery(id+"F0.wireOp",EDGE,"E12.6.11"),sQuery(id+"F0.wireOp",EDGE,"E12.7.0"),sQuery(id+"F0.wireOp",EDGE,"E12.7.1"),sQuery(id+"F0.wireOp",EDGE,"E12.7.2"),sQuery(id+"F0.wireOp",EDGE,"E12.7.3"),sQuery(id+"F0.wireOp",EDGE,"E12.7.4"),sQuery(id+"F0.wireOp",EDGE,"E12.7.5"),sQuery(id+"F0.wireOp",EDGE,"E12.7.6"),sQuery(id+"F0.wireOp",EDGE,"E12.7.7"),sQuery(id+"F0.wireOp",EDGE,"E12.7.10"),sQuery(id+"F0.wireOp",EDGE,"E12.7.11"),sQuery(id+"F0.wireOp",EDGE,"E12.8.0"),sQuery(id+"F0.wireOp",EDGE,"E12.8.1"),sQuery(id+"F0.wireOp",EDGE,"E12.8.2"),sQuery(id+"F0.wireOp",EDGE,"E12.8.3"),sQuery(id+"F0.wireOp",EDGE,"E12.8.4"),sQuery(id+"F0.wireOp",EDGE,"E12.8.5"),sQuery(id+"F0.wireOp",EDGE,"E12.8.6"),sQuery(id+"F0.wireOp",EDGE,"E12.8.7"),sQuery(id+"F0.wireOp",EDGE,"E12.8.10"),sQuery(id+"F0.wireOp",EDGE,"E12.8.11"),sQuery(id+"F0.wireOp",EDGE,"E12.9.0"),sQuery(id+"F0.wireOp",EDGE,"E12.9.1"),sQuery(id+"F0.wireOp",EDGE,"E12.9.2"),sQuery(id+"F0.wireOp",EDGE,"E12.9.3"),sQuery(id+"F0.wireOp",EDGE,"E12.9.4"),sQuery(id+"F0.wireOp",EDGE,"E12.9.5"),sQuery(id+"F0.wireOp",EDGE,"E12.9.6"),sQuery(id+"F0.wireOp",EDGE,"E12.9.7"),sQuery(id+"F0.wireOp",EDGE,"E12.9.10"),sQuery(id+"F0.wireOp",EDGE,"E12.9.11"),sQuery(id+"F0.wireOp",EDGE,"E13.1.0"),sQuery(id+"F0.wireOp",EDGE,"E13.1.1"),sQuery(id+"F0.wireOp",EDGE,"E13.1.2"),sQuery(id+"F0.wireOp",EDGE,"E13.1.5"),sQuery(id+"F0.wireOp",EDGE,"E13.1.6"),sQuery(id+"F0.wireOp",EDGE,"E13.1.7"),sQuery(id+"F0.wireOp",EDGE,"E13.1.8"),sQuery(id+"F0.wireOp",EDGE,"E13.1.9"),sQuery(id+"F0.wireOp",EDGE,"E13.1.10"),sQuery(id+"F0.wireOp",EDGE,"E13.1.11"),sQuery(id+"F0.wireOp",EDGE,"E13.2.0"),sQuery(id+"F0.wireOp",EDGE,"E13.2.1"),sQuery(id+"F0.wireOp",EDGE,"E13.2.2"),sQuery(id+"F0.wireOp",EDGE,"E13.2.5"),sQuery(id+"F0.wireOp",EDGE,"E13.2.6"),sQuery(id+"F0.wireOp",EDGE,"E13.2.7"),sQuery(id+"F0.wireOp",EDGE,"E13.2.8"),sQuery(id+"F0.wireOp",EDGE,"E13.2.9"),sQuery(id+"F0.wireOp",EDGE,"E13.2.10"),sQuery(id+"F0.wireOp",EDGE,"E13.2.11"),sQuery(id+"F0.wireOp",EDGE,"E13.3.0"),sQuery(id+"F0.wireOp",EDGE,"E13.3.1"),sQuery(id+"F0.wireOp",EDGE,"E13.3.2"),sQuery(id+"F0.wireOp",EDGE,"E13.3.5"),sQuery(id+"F0.wireOp",EDGE,"E13.3.6"),sQuery(id+"F0.wireOp",EDGE,"E13.3.7"),sQuery(id+"F0.wireOp",EDGE,"E13.3.8"),sQuery(id+"F0.wireOp",EDGE,"E13.3.9"),sQuery(id+"F0.wireOp",EDGE,"E13.3.10"),sQuery(id+"F0.wireOp",EDGE,"E13.3.11"),sQuery(id+"F0.wireOp",EDGE,"E13.4.0"),sQuery(id+"F0.wireOp",EDGE,"E13.4.1"),sQuery(id+"F0.wireOp",EDGE,"E13.4.2"),sQuery(id+"F0.wireOp",EDGE,"E13.4.5"),sQuery(id+"F0.wireOp",EDGE,"E13.4.6"),sQuery(id+"F0.wireOp",EDGE,"E13.4.7"),sQuery(id+"F0.wireOp",EDGE,"E13.4.8"),sQuery(id+"F0.wireOp",EDGE,"E13.4.9"),sQuery(id+"F0.wireOp",EDGE,"E13.4.10"),sQuery(id+"F0.wireOp",EDGE,"E13.4.11"),sQuery(id+"F0.wireOp",EDGE,"E13.5.0"),sQuery(id+"F0.wireOp",EDGE,"E13.5.1"),sQuery(id+"F0.wireOp",EDGE,"E13.5.2"),sQuery(id+"F0.wireOp",EDGE,"E13.5.5"),sQuery(id+"F0.wireOp",EDGE,"E13.5.6"),sQuery(id+"F0.wireOp",EDGE,"E13.5.7"),sQuery(id+"F0.wireOp",EDGE,"E13.5.8"),sQuery(id+"F0.wireOp",EDGE,"E13.5.9"),sQuery(id+"F0.wireOp",EDGE,"E13.5.10"),sQuery(id+"F0.wireOp",EDGE,"E13.5.11"),sQuery(id+"F0.wireOp",EDGE,"E13.6.0"),sQuery(id+"F0.wireOp",EDGE,"E13.6.1"),sQuery(id+"F0.wireOp",EDGE,"E13.6.2"),sQuery(id+"F0.wireOp",EDGE,"E13.6.5"),sQuery(id+"F0.wireOp",EDGE,"E13.6.6"),sQuery(id+"F0.wireOp",EDGE,"E13.6.7"),sQuery(id+"F0.wireOp",EDGE,"E13.6.8"),sQuery(id+"F0.wireOp",EDGE,"E13.6.9"),sQuery(id+"F0.wireOp",EDGE,"E13.6.10"),sQuery(id+"F0.wireOp",EDGE,"E13.6.11"),sQuery(id+"F0.wireOp",EDGE,"E13.7.0"),sQuery(id+"F0.wireOp",EDGE,"E13.7.1"),sQuery(id+"F0.wireOp",EDGE,"E13.7.2"),sQuery(id+"F0.wireOp",EDGE,"E13.7.5"),sQuery(id+"F0.wireOp",EDGE,"E13.7.6"),sQuery(id+"F0.wireOp",EDGE,"E13.7.7"),sQuery(id+"F0.wireOp",EDGE,"E13.7.8"),sQuery(id+"F0.wireOp",EDGE,"E13.7.9"),sQuery(id+"F0.wireOp",EDGE,"E13.7.10"),sQuery(id+"F0.wireOp",EDGE,"E13.7.11"),sQuery(id+"F0.wireOp",EDGE,"E13.8.0"),sQuery(id+"F0.wireOp",EDGE,"E13.8.1"),sQuery(id+"F0.wireOp",EDGE,"E13.8.2"),sQuery(id+"F0.wireOp",EDGE,"E13.8.5"),sQuery(id+"F0.wireOp",EDGE,"E13.8.6"),sQuery(id+"F0.wireOp",EDGE,"E13.8.7"),sQuery(id+"F0.wireOp",EDGE,"E13.8.8"),sQuery(id+"F0.wireOp",EDGE,"E13.8.9"),sQuery(id+"F0.wireOp",EDGE,"E13.8.10"),sQuery(id+"F0.wireOp",EDGE,"E13.8.11"),sQuery(id+"F0.wireOp",EDGE,"E3"),sQuery(id+"F0.wireOp",EDGE,"E2"),sQuery(id+"F0.wireOp",EDGE,"E1"),sQuery(id+"F0.wireOp",EDGE,"E4"),sQuery(id+"F0.wireOp",EDGE,"E8"),sQuery(id+"F0.wireOp",EDGE,"E5"),sQuery(id+"F0.wireOp",EDGE,"E11"),sQuery(id+"F0.wireOp",EDGE,"E6"),sQuery(id+"F0.wireOp",EDGE,"E7"),sQuery(id+"F0.wireOp",EDGE,"E10"),sQuery(id+"F0.wireOp",EDGE,"E14"),subQ137,sQuery(id+"F0.wireOp",EDGE,"E20.trimOffspring"),sQuery(id+"F0.wireOp",EDGE,"E21.trimOffspring"),sQuery(id+"F0.wireOp",EDGE,"E22.trimOffspring"),sQuery(id+"F0.wireOp",EDGE,"E23.trimOffspring"),sQuery(id+"F0.wireOp",EDGE,"E24.trimOffspring"),sQuery(id+"F0.wireOp",EDGE,"E25.trimOffspring"),sQuery(id+"F0.wireOp",EDGE,"E26.trimOffspring"),sQuery(id+"F0.wireOp",EDGE,"E27.trimOffspring"),sQuery(id+"F0.wireOp",EDGE,"E28.trimOffspring"),sQuery(id+"F0.wireOp",EDGE,"E29.trimOffspring"),sQuery(id+"F0.wireOp",EDGE,"E30.trimOffspring"),sQuery(id+"F0.wireOp",EDGE,"E31.trimOffspring"),sQuery(id+"F0.wireOp",EDGE,"E32.trimOffspring"),sQuery(id+"F0.wireOp",EDGE,"E33.trimOffspring"),sQuery(id+"F0.wireOp",EDGE,"E34.trimOffspring"),sQuery(id+"F0.wireOp",EDGE,"E35.trimOffspring"),sQuery(id+"F0.wireOp",EDGE,"E36.trimOffspring"),sQuery(id+"F0.wireOp",EDGE,"E37")])],"isStart":false})}),makeQuery(id+"F4.opExtrude","CAP_FACE",FACE,{"disambiguationData":[OSD([subQ137,subQ18,sQuery(id+"F3.wireOp",EDGE,"E43.0"),subQ94,subQ72,subQ70,sQuery(id+"F3.wireOp",EDGE,"E49.trimOffspring"),subQ34,subQ80,subQ69,sQuery(id+"F3.wireOp",EDGE,"E50.1.6"),sQuery(id+"F3.wireOp",EDGE,"E50.1.8"),subQ73,subQ77,subQ71,subQ46,sQuery(id+"F3.wireOp",EDGE,"E50.2.6"),sQuery(id+"F3.wireOp",EDGE,"E50.2.8"),subQ67,subQ104,subQ83,subQ76,sQuery(id+"F3.wireOp",EDGE,"E50.3.6"),sQuery(id+"F3.wireOp",EDGE,"E50.3.8"),subQ62,subQ57,subQ52,subQ50,sQuery(id+"F3.wireOp",EDGE,"E50.4.6"),sQuery(id+"F3.wireOp",EDGE,"E50.4.8"),subQ49,subQ43,subQ64,subQ81,sQuery(id+"F3.wireOp",EDGE,"E50.5.6"),sQuery(id+"F3.wireOp",EDGE,"E50.5.8"),subQ84,subQ85,subQ93,subQ98,sQuery(id+"F3.wireOp",EDGE,"E50.6.6"),sQuery(id+"F3.wireOp",EDGE,"E50.6.8"),subQ54,subQ66,subQ105,subQ86,sQuery(id+"F3.wireOp",EDGE,"E50.7.6"),sQuery(id+"F3.wireOp",EDGE,"E50.7.8"),subQ99,subQ63,subQ61,subQ56,sQuery(id+"F3.wireOp",EDGE,"E50.8.6"),sQuery(id+"F3.wireOp",EDGE,"E50.8.8"),subQ106,subQ108,subQ78,subQ109,subQ113,subQ116,subQ117,subQ89,subQ95,subQ96,subQ101,subQ40,subQ47,subQ39,subQ38,subQ37,subQ35,subQ31,subQ29,subQ87,subQ59,subQ28,subQ53,subQ65,subQ103,subQ68,subQ26,subQ74,subQ75,subQ25,subQ8,subQ24,subQ23,subQ22,subQ20,subQ19,subQ44])],"isStart":false})]}),makeQuery(id+"F6.opExtrude","CAP_FACE",FACE,{"disambiguationData":[OSD([sQuery(id+"F5.wireOp",EDGE,"E88"),sQuery(id+"F5.wireOp",EDGE,"E89"),subQ16,sQuery(id+"F5.wireOp",EDGE,"E91.0"),sQuery(id+"F5.wireOp",EDGE,"E92"),sQuery(id+"F5.wireOp",EDGE,"E93"),subQ15,subQ115,subQ13,sQuery(id+"F5.wireOp",EDGE,"E97.trimOffspring"),subQ32,subQ107,subQ10,sQuery(id+"F5.wireOp",EDGE,"E98.1.6"),sQuery(id+"F5.wireOp",EDGE,"E98.1.7"),sQuery(id+"F5.wireOp",EDGE,"E98.1.8"),sQuery(id+"F5.wireOp",EDGE,"E98.1.9"),subQ58,subQ7,subQ42,subQ6,sQuery(id+"F5.wireOp",EDGE,"E98.2.6"),sQuery(id+"F5.wireOp",EDGE,"E98.2.7"),sQuery(id+"F5.wireOp",EDGE,"E98.2.8"),sQuery(id+"F5.wireOp",EDGE,"E98.2.9"),subQ111,subQ4,subQ97,sQuery(id+"F5.wireOp",EDGE,"E98.3.5"),sQuery(id+"F5.wireOp",EDGE,"E98.3.6"),sQuery(id+"F5.wireOp",EDGE,"E98.3.7"),sQuery(id+"F5.wireOp",EDGE,"E98.3.8"),sQuery(id+"F5.wireOp",EDGE,"E98.3.9"),sQuery(id+"F5.wireOp",EDGE,"E98.3.10"),subQ11,subQ45,sQuery(id+"F5.wireOp",EDGE,"E98.4.5"),sQuery(id+"F5.wireOp",EDGE,"E98.4.6"),sQuery(id+"F5.wireOp",EDGE,"E98.4.7"),sQuery(id+"F5.wireOp",EDGE,"E98.4.8"),sQuery(id+"F5.wireOp",EDGE,"E98.4.9"),sQuery(id+"F5.wireOp",EDGE,"E98.4.10"),subQ91,subQ3,sQuery(id+"F5.wireOp",EDGE,"E98.5.5"),sQuery(id+"F5.wireOp",EDGE,"E98.5.6"),sQuery(id+"F5.wireOp",EDGE,"E98.5.7"),sQuery(id+"F5.wireOp",EDGE,"E98.5.8"),sQuery(id+"F5.wireOp",EDGE,"E98.5.9"),sQuery(id+"F5.wireOp",EDGE,"E98.5.10"),subQ1,subQ17,sQuery(id+"F5.wireOp",EDGE,"E98.6.5"),sQuery(id+"F5.wireOp",EDGE,"E98.6.6"),sQuery(id+"F5.wireOp",EDGE,"E98.6.7"),sQuery(id+"F5.wireOp",EDGE,"E98.6.8"),sQuery(id+"F5.wireOp",EDGE,"E98.6.9"),sQuery(id+"F5.wireOp",EDGE,"E98.6.10"),subQ0,subQ33,subQ51,sQuery(id+"F5.wireOp",EDGE,"E98.7.6"),sQuery(id+"F5.wireOp",EDGE,"E98.7.7"),sQuery(id+"F5.wireOp",EDGE,"E98.7.8"),sQuery(id+"F5.wireOp",EDGE,"E98.7.9"),subQ27,subQ118,subQ14,subQ48,sQuery(id+"F5.wireOp",EDGE,"E98.8.6"),sQuery(id+"F5.wireOp",EDGE,"E98.8.7"),sQuery(id+"F5.wireOp",EDGE,"E98.8.8"),sQuery(id+"F5.wireOp",EDGE,"E98.8.9"),subQ21,subQ119,subQ120,subQ60,subQ9,subQ121,subQ110,subQ122,subQ102,subQ123,subQ124,subQ112,subQ5,subQ90,subQ82,subQ125,subQ30,subQ126,subQ127,subQ114,subQ12,subQ41,subQ128,subQ129,subQ100,subQ130,subQ131,subQ132,subQ92,subQ88,subQ133,subQ134,subQ79,subQ135,subQ136,subQ55,subQ2])],"isStart":true})]}),makeQuery(id+"F8.opExtrude","CAP_FACE",FACE,{"disambiguationData":[OSD([sQuery(id+"F7.wireOp",EDGE,"E135"),subQ36])],"isStart":true})]})});}
            var sketch = newSketch(context, id + "F11", { "sketchPlane" : qUnion([Q0])});
            skLineSegment(sketch, "E140", {"start": v(0, 0) * mm, "end": v(0, 51.6) * mm});
            skLineSegment(sketch, "E141", {"start": v(0, 51.6) * mm, "end": v(0, 55.33) * mm});
            skLineSegment(sketch, "E142", {"start": v(0, 55.33) * mm, "end": v(-2.86, 51.52) * mm});
            skLineSegment(sketch, "E143.MirrorCS", {"start": v(0, 55.33) * mm, "end": v(2.86, 51.52) * mm});
            skLineSegment(sketch, "E144", {"start": v(-2.86, 51.52) * mm, "end": v(0, 50.05) * mm});
            skLineSegment(sketch, "E145", {"start": v(0, 50.05) * mm, "end": v(2.86, 51.52) * mm});
            skLineSegment(sketch, "E146.1.0", {"start": v(-39.12, 39.12) * mm, "end": v(-34.4, 38.45) * mm});
            skLineSegment(sketch, "E146.1.1", {"start": v(-39.12, 39.12) * mm, "end": v(-38.45, 34.4) * mm});
            skLineSegment(sketch, "E146.1.2", {"start": v(-38.45, 34.4) * mm, "end": v(-35.39, 35.39) * mm});
            skLineSegment(sketch, "E146.1.3", {"start": v(-35.39, 35.39) * mm, "end": v(-34.4, 38.45) * mm});
            skLineSegment(sketch, "E146.2.0", {"start": v(-55.33, 0) * mm, "end": v(-51.52, 2.86) * mm});
            skLineSegment(sketch, "E146.2.1", {"start": v(-55.33, 0) * mm, "end": v(-51.52, -2.86) * mm});
            skLineSegment(sketch, "E146.2.2", {"start": v(-51.52, -2.86) * mm, "end": v(-50.05, 0) * mm});
            skLineSegment(sketch, "E146.2.3", {"start": v(-50.05, 0) * mm, "end": v(-51.52, 2.86) * mm});
            skLineSegment(sketch, "E146.3.0", {"start": v(-39.12, -39.12) * mm, "end": v(-38.45, -34.4) * mm});
            skLineSegment(sketch, "E146.3.1", {"start": v(-39.12, -39.12) * mm, "end": v(-34.4, -38.45) * mm});
            skLineSegment(sketch, "E146.3.2", {"start": v(-34.4, -38.45) * mm, "end": v(-35.39, -35.39) * mm});
            skLineSegment(sketch, "E146.3.3", {"start": v(-35.39, -35.39) * mm, "end": v(-38.45, -34.4) * mm});
            skLineSegment(sketch, "E146.4.0", {"start": v(0, -55.33) * mm, "end": v(-2.86, -51.52) * mm});
            skLineSegment(sketch, "E146.4.1", {"start": v(0, -55.33) * mm, "end": v(2.86, -51.52) * mm});
            skLineSegment(sketch, "E146.4.2", {"start": v(2.86, -51.52) * mm, "end": v(0, -50.05) * mm});
            skLineSegment(sketch, "E146.4.3", {"start": v(0, -50.05) * mm, "end": v(-2.86, -51.52) * mm});
            skLineSegment(sketch, "E146.5.0", {"start": v(39.12, -39.12) * mm, "end": v(34.4, -38.45) * mm});
            skLineSegment(sketch, "E146.5.1", {"start": v(39.12, -39.12) * mm, "end": v(38.45, -34.4) * mm});
            skLineSegment(sketch, "E146.5.2", {"start": v(38.45, -34.4) * mm, "end": v(35.39, -35.39) * mm});
            skLineSegment(sketch, "E146.5.3", {"start": v(35.39, -35.39) * mm, "end": v(34.4, -38.45) * mm});
            skLineSegment(sketch, "E146.6.0", {"start": v(55.33, 0) * mm, "end": v(51.52, -2.86) * mm});
            skLineSegment(sketch, "E146.6.1", {"start": v(55.33, 0) * mm, "end": v(51.52, 2.86) * mm});
            skLineSegment(sketch, "E146.6.2", {"start": v(51.52, 2.86) * mm, "end": v(50.05, 0) * mm});
            skLineSegment(sketch, "E146.6.3", {"start": v(50.05, 0) * mm, "end": v(51.52, -2.86) * mm});
            skLineSegment(sketch, "E146.7.0", {"start": v(39.12, 39.12) * mm, "end": v(38.45, 34.4) * mm});
            skLineSegment(sketch, "E146.7.1", {"start": v(39.12, 39.12) * mm, "end": v(34.4, 38.45) * mm});
            skLineSegment(sketch, "E146.7.2", {"start": v(34.4, 38.45) * mm, "end": v(35.39, 35.39) * mm});
            skLineSegment(sketch, "E146.7.3", {"start": v(35.39, 35.39) * mm, "end": v(38.45, 34.4) * mm});
            skPoint(sketch, "E146.center", {"position": v(0, 0) * mm});
            skSolve(sketch);
        }
        {
            var Q0;
            Q0 = qSketchRegion(id + "F11", true);
            extrude(context, id + "F12", {"entities" : qUnion([Q0]), "oppositeDirection" : true, "depth" : 5.08 * mm});
        }
        {
            var Q0;
            Q0=makeQuery(id+"F10.boolean.opBoolean","SPLIT",BODY,{"disambiguationData":[OD(0.0)],"derivedFrom":makeQuery(id+"F1.opExtrude","SWEPT_BODY",BODY,{"disambiguationData":[OSD([sQuery(id+"F0.wireOp",EDGE,"E12.1.0"),sQuery(id+"F0.wireOp",EDGE,"E12.1.1"),sQuery(id+"F0.wireOp",EDGE,"E12.1.2"),sQuery(id+"F0.wireOp",EDGE,"E12.1.3"),sQuery(id+"F0.wireOp",EDGE,"E12.1.4"),sQuery(id+"F0.wireOp",EDGE,"E12.1.5"),sQuery(id+"F0.wireOp",EDGE,"E12.1.6"),sQuery(id+"F0.wireOp",EDGE,"E12.1.7"),sQuery(id+"F0.wireOp",EDGE,"E12.1.10"),sQuery(id+"F0.wireOp",EDGE,"E12.1.11"),sQuery(id+"F0.wireOp",EDGE,"E12.2.0"),sQuery(id+"F0.wireOp",EDGE,"E12.2.1"),sQuery(id+"F0.wireOp",EDGE,"E12.2.2"),sQuery(id+"F0.wireOp",EDGE,"E12.2.3"),sQuery(id+"F0.wireOp",EDGE,"E12.2.4"),sQuery(id+"F0.wireOp",EDGE,"E12.2.5"),sQuery(id+"F0.wireOp",EDGE,"E12.2.6"),sQuery(id+"F0.wireOp",EDGE,"E12.2.7"),sQuery(id+"F0.wireOp",EDGE,"E12.2.10"),sQuery(id+"F0.wireOp",EDGE,"E12.2.11"),sQuery(id+"F0.wireOp",EDGE,"E12.3.0"),sQuery(id+"F0.wireOp",EDGE,"E12.3.1"),sQuery(id+"F0.wireOp",EDGE,"E12.3.2"),sQuery(id+"F0.wireOp",EDGE,"E12.3.3"),sQuery(id+"F0.wireOp",EDGE,"E12.3.4"),sQuery(id+"F0.wireOp",EDGE,"E12.3.5"),sQuery(id+"F0.wireOp",EDGE,"E12.3.6"),sQuery(id+"F0.wireOp",EDGE,"E12.3.7"),sQuery(id+"F0.wireOp",EDGE,"E12.3.10"),sQuery(id+"F0.wireOp",EDGE,"E12.3.11"),sQuery(id+"F0.wireOp",EDGE,"E12.4.0"),sQuery(id+"F0.wireOp",EDGE,"E12.4.1"),sQuery(id+"F0.wireOp",EDGE,"E12.4.2"),sQuery(id+"F0.wireOp",EDGE,"E12.4.3"),sQuery(id+"F0.wireOp",EDGE,"E12.4.4"),sQuery(id+"F0.wireOp",EDGE,"E12.4.5"),sQuery(id+"F0.wireOp",EDGE,"E12.4.6"),sQuery(id+"F0.wireOp",EDGE,"E12.4.7"),sQuery(id+"F0.wireOp",EDGE,"E12.4.10"),sQuery(id+"F0.wireOp",EDGE,"E12.4.11"),sQuery(id+"F0.wireOp",EDGE,"E12.5.0"),sQuery(id+"F0.wireOp",EDGE,"E12.5.1"),sQuery(id+"F0.wireOp",EDGE,"E12.5.2"),sQuery(id+"F0.wireOp",EDGE,"E12.5.3"),sQuery(id+"F0.wireOp",EDGE,"E12.5.4"),sQuery(id+"F0.wireOp",EDGE,"E12.5.5"),sQuery(id+"F0.wireOp",EDGE,"E12.5.6"),sQuery(id+"F0.wireOp",EDGE,"E12.5.7"),sQuery(id+"F0.wireOp",EDGE,"E12.5.10"),sQuery(id+"F0.wireOp",EDGE,"E12.5.11"),sQuery(id+"F0.wireOp",EDGE,"E12.6.0"),sQuery(id+"F0.wireOp",EDGE,"E12.6.1"),sQuery(id+"F0.wireOp",EDGE,"E12.6.2"),sQuery(id+"F0.wireOp",EDGE,"E12.6.3"),sQuery(id+"F0.wireOp",EDGE,"E12.6.4"),sQuery(id+"F0.wireOp",EDGE,"E12.6.5"),sQuery(id+"F0.wireOp",EDGE,"E12.6.6"),sQuery(id+"F0.wireOp",EDGE,"E12.6.7"),sQuery(id+"F0.wireOp",EDGE,"E12.6.10"),sQuery(id+"F0.wireOp",EDGE,"E12.6.11"),sQuery(id+"F0.wireOp",EDGE,"E12.7.0"),sQuery(id+"F0.wireOp",EDGE,"E12.7.1"),sQuery(id+"F0.wireOp",EDGE,"E12.7.2"),sQuery(id+"F0.wireOp",EDGE,"E12.7.3"),sQuery(id+"F0.wireOp",EDGE,"E12.7.4"),sQuery(id+"F0.wireOp",EDGE,"E12.7.5"),sQuery(id+"F0.wireOp",EDGE,"E12.7.6"),sQuery(id+"F0.wireOp",EDGE,"E12.7.7"),sQuery(id+"F0.wireOp",EDGE,"E12.7.10"),sQuery(id+"F0.wireOp",EDGE,"E12.7.11"),sQuery(id+"F0.wireOp",EDGE,"E12.8.0"),sQuery(id+"F0.wireOp",EDGE,"E12.8.1"),sQuery(id+"F0.wireOp",EDGE,"E12.8.2"),sQuery(id+"F0.wireOp",EDGE,"E12.8.3"),sQuery(id+"F0.wireOp",EDGE,"E12.8.4"),sQuery(id+"F0.wireOp",EDGE,"E12.8.5"),sQuery(id+"F0.wireOp",EDGE,"E12.8.6"),sQuery(id+"F0.wireOp",EDGE,"E12.8.7"),sQuery(id+"F0.wireOp",EDGE,"E12.8.10"),sQuery(id+"F0.wireOp",EDGE,"E12.8.11"),sQuery(id+"F0.wireOp",EDGE,"E12.9.0"),sQuery(id+"F0.wireOp",EDGE,"E12.9.1"),sQuery(id+"F0.wireOp",EDGE,"E12.9.2"),sQuery(id+"F0.wireOp",EDGE,"E12.9.3"),sQuery(id+"F0.wireOp",EDGE,"E12.9.4"),sQuery(id+"F0.wireOp",EDGE,"E12.9.5"),sQuery(id+"F0.wireOp",EDGE,"E12.9.6"),sQuery(id+"F0.wireOp",EDGE,"E12.9.7"),sQuery(id+"F0.wireOp",EDGE,"E12.9.10"),sQuery(id+"F0.wireOp",EDGE,"E12.9.11"),sQuery(id+"F0.wireOp",EDGE,"E13.1.0"),sQuery(id+"F0.wireOp",EDGE,"E13.1.1"),sQuery(id+"F0.wireOp",EDGE,"E13.1.2"),sQuery(id+"F0.wireOp",EDGE,"E13.1.5"),sQuery(id+"F0.wireOp",EDGE,"E13.1.6"),sQuery(id+"F0.wireOp",EDGE,"E13.1.7"),sQuery(id+"F0.wireOp",EDGE,"E13.1.8"),sQuery(id+"F0.wireOp",EDGE,"E13.1.9"),sQuery(id+"F0.wireOp",EDGE,"E13.1.10"),sQuery(id+"F0.wireOp",EDGE,"E13.1.11"),sQuery(id+"F0.wireOp",EDGE,"E13.2.0"),sQuery(id+"F0.wireOp",EDGE,"E13.2.1"),sQuery(id+"F0.wireOp",EDGE,"E13.2.2"),sQuery(id+"F0.wireOp",EDGE,"E13.2.5"),sQuery(id+"F0.wireOp",EDGE,"E13.2.6"),sQuery(id+"F0.wireOp",EDGE,"E13.2.7"),sQuery(id+"F0.wireOp",EDGE,"E13.2.8"),sQuery(id+"F0.wireOp",EDGE,"E13.2.9"),sQuery(id+"F0.wireOp",EDGE,"E13.2.10"),sQuery(id+"F0.wireOp",EDGE,"E13.2.11"),sQuery(id+"F0.wireOp",EDGE,"E13.3.0"),sQuery(id+"F0.wireOp",EDGE,"E13.3.1"),sQuery(id+"F0.wireOp",EDGE,"E13.3.2"),sQuery(id+"F0.wireOp",EDGE,"E13.3.5"),sQuery(id+"F0.wireOp",EDGE,"E13.3.6"),sQuery(id+"F0.wireOp",EDGE,"E13.3.7"),sQuery(id+"F0.wireOp",EDGE,"E13.3.8"),sQuery(id+"F0.wireOp",EDGE,"E13.3.9"),sQuery(id+"F0.wireOp",EDGE,"E13.3.10"),sQuery(id+"F0.wireOp",EDGE,"E13.3.11"),sQuery(id+"F0.wireOp",EDGE,"E13.4.0"),sQuery(id+"F0.wireOp",EDGE,"E13.4.1"),sQuery(id+"F0.wireOp",EDGE,"E13.4.2"),sQuery(id+"F0.wireOp",EDGE,"E13.4.5"),sQuery(id+"F0.wireOp",EDGE,"E13.4.6"),sQuery(id+"F0.wireOp",EDGE,"E13.4.7"),sQuery(id+"F0.wireOp",EDGE,"E13.4.8"),sQuery(id+"F0.wireOp",EDGE,"E13.4.9"),sQuery(id+"F0.wireOp",EDGE,"E13.4.10"),sQuery(id+"F0.wireOp",EDGE,"E13.4.11"),sQuery(id+"F0.wireOp",EDGE,"E13.5.0"),sQuery(id+"F0.wireOp",EDGE,"E13.5.1"),sQuery(id+"F0.wireOp",EDGE,"E13.5.2"),sQuery(id+"F0.wireOp",EDGE,"E13.5.5"),sQuery(id+"F0.wireOp",EDGE,"E13.5.6"),sQuery(id+"F0.wireOp",EDGE,"E13.5.7"),sQuery(id+"F0.wireOp",EDGE,"E13.5.8"),sQuery(id+"F0.wireOp",EDGE,"E13.5.9"),sQuery(id+"F0.wireOp",EDGE,"E13.5.10"),sQuery(id+"F0.wireOp",EDGE,"E13.5.11"),sQuery(id+"F0.wireOp",EDGE,"E13.6.0"),sQuery(id+"F0.wireOp",EDGE,"E13.6.1"),sQuery(id+"F0.wireOp",EDGE,"E13.6.2"),sQuery(id+"F0.wireOp",EDGE,"E13.6.5"),sQuery(id+"F0.wireOp",EDGE,"E13.6.6"),sQuery(id+"F0.wireOp",EDGE,"E13.6.7"),sQuery(id+"F0.wireOp",EDGE,"E13.6.8"),sQuery(id+"F0.wireOp",EDGE,"E13.6.9"),sQuery(id+"F0.wireOp",EDGE,"E13.6.10"),sQuery(id+"F0.wireOp",EDGE,"E13.6.11"),sQuery(id+"F0.wireOp",EDGE,"E13.7.0"),sQuery(id+"F0.wireOp",EDGE,"E13.7.1"),sQuery(id+"F0.wireOp",EDGE,"E13.7.2"),sQuery(id+"F0.wireOp",EDGE,"E13.7.5"),sQuery(id+"F0.wireOp",EDGE,"E13.7.6"),sQuery(id+"F0.wireOp",EDGE,"E13.7.7"),sQuery(id+"F0.wireOp",EDGE,"E13.7.8"),sQuery(id+"F0.wireOp",EDGE,"E13.7.9"),sQuery(id+"F0.wireOp",EDGE,"E13.7.10"),sQuery(id+"F0.wireOp",EDGE,"E13.7.11"),sQuery(id+"F0.wireOp",EDGE,"E13.8.0"),sQuery(id+"F0.wireOp",EDGE,"E13.8.1"),sQuery(id+"F0.wireOp",EDGE,"E13.8.2"),sQuery(id+"F0.wireOp",EDGE,"E13.8.5"),sQuery(id+"F0.wireOp",EDGE,"E13.8.6"),sQuery(id+"F0.wireOp",EDGE,"E13.8.7"),sQuery(id+"F0.wireOp",EDGE,"E13.8.8"),sQuery(id+"F0.wireOp",EDGE,"E13.8.9"),sQuery(id+"F0.wireOp",EDGE,"E13.8.10"),sQuery(id+"F0.wireOp",EDGE,"E13.8.11"),sQuery(id+"F0.wireOp",EDGE,"E3"),sQuery(id+"F0.wireOp",EDGE,"E2"),sQuery(id+"F0.wireOp",EDGE,"E1"),sQuery(id+"F0.wireOp",EDGE,"E4"),sQuery(id+"F0.wireOp",EDGE,"E8"),sQuery(id+"F0.wireOp",EDGE,"E5"),sQuery(id+"F0.wireOp",EDGE,"E11"),sQuery(id+"F0.wireOp",EDGE,"E6"),sQuery(id+"F0.wireOp",EDGE,"E7"),sQuery(id+"F0.wireOp",EDGE,"E10"),sQuery(id+"F0.wireOp",EDGE,"E14"),sQuery(id+"F0.wireOp",EDGE,"E15"),sQuery(id+"F0.wireOp",EDGE,"E20.trimOffspring"),sQuery(id+"F0.wireOp",EDGE,"E21.trimOffspring"),sQuery(id+"F0.wireOp",EDGE,"E22.trimOffspring"),sQuery(id+"F0.wireOp",EDGE,"E23.trimOffspring"),sQuery(id+"F0.wireOp",EDGE,"E24.trimOffspring"),sQuery(id+"F0.wireOp",EDGE,"E25.trimOffspring"),sQuery(id+"F0.wireOp",EDGE,"E26.trimOffspring"),sQuery(id+"F0.wireOp",EDGE,"E27.trimOffspring"),sQuery(id+"F0.wireOp",EDGE,"E28.trimOffspring"),sQuery(id+"F0.wireOp",EDGE,"E29.trimOffspring"),sQuery(id+"F0.wireOp",EDGE,"E30.trimOffspring"),sQuery(id+"F0.wireOp",EDGE,"E31.trimOffspring"),sQuery(id+"F0.wireOp",EDGE,"E32.trimOffspring"),sQuery(id+"F0.wireOp",EDGE,"E33.trimOffspring"),sQuery(id+"F0.wireOp",EDGE,"E34.trimOffspring"),sQuery(id+"F0.wireOp",EDGE,"E35.trimOffspring"),sQuery(id+"F0.wireOp",EDGE,"E36.trimOffspring"),sQuery(id+"F0.wireOp",EDGE,"E37")])]})});
            var Q1;
            Q1=makeQuery(id+"F10.boolean.opBoolean","SPLIT",BODY,{"disambiguationData":[OD(1.0)],"derivedFrom":makeQuery(id+"F1.opExtrude","SWEPT_BODY",BODY,{"disambiguationData":[OSD([sQuery(id+"F0.wireOp",EDGE,"E12.1.0"),sQuery(id+"F0.wireOp",EDGE,"E12.1.1"),sQuery(id+"F0.wireOp",EDGE,"E12.1.2"),sQuery(id+"F0.wireOp",EDGE,"E12.1.3"),sQuery(id+"F0.wireOp",EDGE,"E12.1.4"),sQuery(id+"F0.wireOp",EDGE,"E12.1.5"),sQuery(id+"F0.wireOp",EDGE,"E12.1.6"),sQuery(id+"F0.wireOp",EDGE,"E12.1.7"),sQuery(id+"F0.wireOp",EDGE,"E12.1.10"),sQuery(id+"F0.wireOp",EDGE,"E12.1.11"),sQuery(id+"F0.wireOp",EDGE,"E12.2.0"),sQuery(id+"F0.wireOp",EDGE,"E12.2.1"),sQuery(id+"F0.wireOp",EDGE,"E12.2.2"),sQuery(id+"F0.wireOp",EDGE,"E12.2.3"),sQuery(id+"F0.wireOp",EDGE,"E12.2.4"),sQuery(id+"F0.wireOp",EDGE,"E12.2.5"),sQuery(id+"F0.wireOp",EDGE,"E12.2.6"),sQuery(id+"F0.wireOp",EDGE,"E12.2.7"),sQuery(id+"F0.wireOp",EDGE,"E12.2.10"),sQuery(id+"F0.wireOp",EDGE,"E12.2.11"),sQuery(id+"F0.wireOp",EDGE,"E12.3.0"),sQuery(id+"F0.wireOp",EDGE,"E12.3.1"),sQuery(id+"F0.wireOp",EDGE,"E12.3.2"),sQuery(id+"F0.wireOp",EDGE,"E12.3.3"),sQuery(id+"F0.wireOp",EDGE,"E12.3.4"),sQuery(id+"F0.wireOp",EDGE,"E12.3.5"),sQuery(id+"F0.wireOp",EDGE,"E12.3.6"),sQuery(id+"F0.wireOp",EDGE,"E12.3.7"),sQuery(id+"F0.wireOp",EDGE,"E12.3.10"),sQuery(id+"F0.wireOp",EDGE,"E12.3.11"),sQuery(id+"F0.wireOp",EDGE,"E12.4.0"),sQuery(id+"F0.wireOp",EDGE,"E12.4.1"),sQuery(id+"F0.wireOp",EDGE,"E12.4.2"),sQuery(id+"F0.wireOp",EDGE,"E12.4.3"),sQuery(id+"F0.wireOp",EDGE,"E12.4.4"),sQuery(id+"F0.wireOp",EDGE,"E12.4.5"),sQuery(id+"F0.wireOp",EDGE,"E12.4.6"),sQuery(id+"F0.wireOp",EDGE,"E12.4.7"),sQuery(id+"F0.wireOp",EDGE,"E12.4.10"),sQuery(id+"F0.wireOp",EDGE,"E12.4.11"),sQuery(id+"F0.wireOp",EDGE,"E12.5.0"),sQuery(id+"F0.wireOp",EDGE,"E12.5.1"),sQuery(id+"F0.wireOp",EDGE,"E12.5.2"),sQuery(id+"F0.wireOp",EDGE,"E12.5.3"),sQuery(id+"F0.wireOp",EDGE,"E12.5.4"),sQuery(id+"F0.wireOp",EDGE,"E12.5.5"),sQuery(id+"F0.wireOp",EDGE,"E12.5.6"),sQuery(id+"F0.wireOp",EDGE,"E12.5.7"),sQuery(id+"F0.wireOp",EDGE,"E12.5.10"),sQuery(id+"F0.wireOp",EDGE,"E12.5.11"),sQuery(id+"F0.wireOp",EDGE,"E12.6.0"),sQuery(id+"F0.wireOp",EDGE,"E12.6.1"),sQuery(id+"F0.wireOp",EDGE,"E12.6.2"),sQuery(id+"F0.wireOp",EDGE,"E12.6.3"),sQuery(id+"F0.wireOp",EDGE,"E12.6.4"),sQuery(id+"F0.wireOp",EDGE,"E12.6.5"),sQuery(id+"F0.wireOp",EDGE,"E12.6.6"),sQuery(id+"F0.wireOp",EDGE,"E12.6.7"),sQuery(id+"F0.wireOp",EDGE,"E12.6.10"),sQuery(id+"F0.wireOp",EDGE,"E12.6.11"),sQuery(id+"F0.wireOp",EDGE,"E12.7.0"),sQuery(id+"F0.wireOp",EDGE,"E12.7.1"),sQuery(id+"F0.wireOp",EDGE,"E12.7.2"),sQuery(id+"F0.wireOp",EDGE,"E12.7.3"),sQuery(id+"F0.wireOp",EDGE,"E12.7.4"),sQuery(id+"F0.wireOp",EDGE,"E12.7.5"),sQuery(id+"F0.wireOp",EDGE,"E12.7.6"),sQuery(id+"F0.wireOp",EDGE,"E12.7.7"),sQuery(id+"F0.wireOp",EDGE,"E12.7.10"),sQuery(id+"F0.wireOp",EDGE,"E12.7.11"),sQuery(id+"F0.wireOp",EDGE,"E12.8.0"),sQuery(id+"F0.wireOp",EDGE,"E12.8.1"),sQuery(id+"F0.wireOp",EDGE,"E12.8.2"),sQuery(id+"F0.wireOp",EDGE,"E12.8.3"),sQuery(id+"F0.wireOp",EDGE,"E12.8.4"),sQuery(id+"F0.wireOp",EDGE,"E12.8.5"),sQuery(id+"F0.wireOp",EDGE,"E12.8.6"),sQuery(id+"F0.wireOp",EDGE,"E12.8.7"),sQuery(id+"F0.wireOp",EDGE,"E12.8.10"),sQuery(id+"F0.wireOp",EDGE,"E12.8.11"),sQuery(id+"F0.wireOp",EDGE,"E12.9.0"),sQuery(id+"F0.wireOp",EDGE,"E12.9.1"),sQuery(id+"F0.wireOp",EDGE,"E12.9.2"),sQuery(id+"F0.wireOp",EDGE,"E12.9.3"),sQuery(id+"F0.wireOp",EDGE,"E12.9.4"),sQuery(id+"F0.wireOp",EDGE,"E12.9.5"),sQuery(id+"F0.wireOp",EDGE,"E12.9.6"),sQuery(id+"F0.wireOp",EDGE,"E12.9.7"),sQuery(id+"F0.wireOp",EDGE,"E12.9.10"),sQuery(id+"F0.wireOp",EDGE,"E12.9.11"),sQuery(id+"F0.wireOp",EDGE,"E13.1.0"),sQuery(id+"F0.wireOp",EDGE,"E13.1.1"),sQuery(id+"F0.wireOp",EDGE,"E13.1.2"),sQuery(id+"F0.wireOp",EDGE,"E13.1.5"),sQuery(id+"F0.wireOp",EDGE,"E13.1.6"),sQuery(id+"F0.wireOp",EDGE,"E13.1.7"),sQuery(id+"F0.wireOp",EDGE,"E13.1.8"),sQuery(id+"F0.wireOp",EDGE,"E13.1.9"),sQuery(id+"F0.wireOp",EDGE,"E13.1.10"),sQuery(id+"F0.wireOp",EDGE,"E13.1.11"),sQuery(id+"F0.wireOp",EDGE,"E13.2.0"),sQuery(id+"F0.wireOp",EDGE,"E13.2.1"),sQuery(id+"F0.wireOp",EDGE,"E13.2.2"),sQuery(id+"F0.wireOp",EDGE,"E13.2.5"),sQuery(id+"F0.wireOp",EDGE,"E13.2.6"),sQuery(id+"F0.wireOp",EDGE,"E13.2.7"),sQuery(id+"F0.wireOp",EDGE,"E13.2.8"),sQuery(id+"F0.wireOp",EDGE,"E13.2.9"),sQuery(id+"F0.wireOp",EDGE,"E13.2.10"),sQuery(id+"F0.wireOp",EDGE,"E13.2.11"),sQuery(id+"F0.wireOp",EDGE,"E13.3.0"),sQuery(id+"F0.wireOp",EDGE,"E13.3.1"),sQuery(id+"F0.wireOp",EDGE,"E13.3.2"),sQuery(id+"F0.wireOp",EDGE,"E13.3.5"),sQuery(id+"F0.wireOp",EDGE,"E13.3.6"),sQuery(id+"F0.wireOp",EDGE,"E13.3.7"),sQuery(id+"F0.wireOp",EDGE,"E13.3.8"),sQuery(id+"F0.wireOp",EDGE,"E13.3.9"),sQuery(id+"F0.wireOp",EDGE,"E13.3.10"),sQuery(id+"F0.wireOp",EDGE,"E13.3.11"),sQuery(id+"F0.wireOp",EDGE,"E13.4.0"),sQuery(id+"F0.wireOp",EDGE,"E13.4.1"),sQuery(id+"F0.wireOp",EDGE,"E13.4.2"),sQuery(id+"F0.wireOp",EDGE,"E13.4.5"),sQuery(id+"F0.wireOp",EDGE,"E13.4.6"),sQuery(id+"F0.wireOp",EDGE,"E13.4.7"),sQuery(id+"F0.wireOp",EDGE,"E13.4.8"),sQuery(id+"F0.wireOp",EDGE,"E13.4.9"),sQuery(id+"F0.wireOp",EDGE,"E13.4.10"),sQuery(id+"F0.wireOp",EDGE,"E13.4.11"),sQuery(id+"F0.wireOp",EDGE,"E13.5.0"),sQuery(id+"F0.wireOp",EDGE,"E13.5.1"),sQuery(id+"F0.wireOp",EDGE,"E13.5.2"),sQuery(id+"F0.wireOp",EDGE,"E13.5.5"),sQuery(id+"F0.wireOp",EDGE,"E13.5.6"),sQuery(id+"F0.wireOp",EDGE,"E13.5.7"),sQuery(id+"F0.wireOp",EDGE,"E13.5.8"),sQuery(id+"F0.wireOp",EDGE,"E13.5.9"),sQuery(id+"F0.wireOp",EDGE,"E13.5.10"),sQuery(id+"F0.wireOp",EDGE,"E13.5.11"),sQuery(id+"F0.wireOp",EDGE,"E13.6.0"),sQuery(id+"F0.wireOp",EDGE,"E13.6.1"),sQuery(id+"F0.wireOp",EDGE,"E13.6.2"),sQuery(id+"F0.wireOp",EDGE,"E13.6.5"),sQuery(id+"F0.wireOp",EDGE,"E13.6.6"),sQuery(id+"F0.wireOp",EDGE,"E13.6.7"),sQuery(id+"F0.wireOp",EDGE,"E13.6.8"),sQuery(id+"F0.wireOp",EDGE,"E13.6.9"),sQuery(id+"F0.wireOp",EDGE,"E13.6.10"),sQuery(id+"F0.wireOp",EDGE,"E13.6.11"),sQuery(id+"F0.wireOp",EDGE,"E13.7.0"),sQuery(id+"F0.wireOp",EDGE,"E13.7.1"),sQuery(id+"F0.wireOp",EDGE,"E13.7.2"),sQuery(id+"F0.wireOp",EDGE,"E13.7.5"),sQuery(id+"F0.wireOp",EDGE,"E13.7.6"),sQuery(id+"F0.wireOp",EDGE,"E13.7.7"),sQuery(id+"F0.wireOp",EDGE,"E13.7.8"),sQuery(id+"F0.wireOp",EDGE,"E13.7.9"),sQuery(id+"F0.wireOp",EDGE,"E13.7.10"),sQuery(id+"F0.wireOp",EDGE,"E13.7.11"),sQuery(id+"F0.wireOp",EDGE,"E13.8.0"),sQuery(id+"F0.wireOp",EDGE,"E13.8.1"),sQuery(id+"F0.wireOp",EDGE,"E13.8.2"),sQuery(id+"F0.wireOp",EDGE,"E13.8.5"),sQuery(id+"F0.wireOp",EDGE,"E13.8.6"),sQuery(id+"F0.wireOp",EDGE,"E13.8.7"),sQuery(id+"F0.wireOp",EDGE,"E13.8.8"),sQuery(id+"F0.wireOp",EDGE,"E13.8.9"),sQuery(id+"F0.wireOp",EDGE,"E13.8.10"),sQuery(id+"F0.wireOp",EDGE,"E13.8.11"),sQuery(id+"F0.wireOp",EDGE,"E3"),sQuery(id+"F0.wireOp",EDGE,"E2"),sQuery(id+"F0.wireOp",EDGE,"E1"),sQuery(id+"F0.wireOp",EDGE,"E4"),sQuery(id+"F0.wireOp",EDGE,"E8"),sQuery(id+"F0.wireOp",EDGE,"E5"),sQuery(id+"F0.wireOp",EDGE,"E11"),sQuery(id+"F0.wireOp",EDGE,"E6"),sQuery(id+"F0.wireOp",EDGE,"E7"),sQuery(id+"F0.wireOp",EDGE,"E10"),sQuery(id+"F0.wireOp",EDGE,"E14"),sQuery(id+"F0.wireOp",EDGE,"E15"),sQuery(id+"F0.wireOp",EDGE,"E20.trimOffspring"),sQuery(id+"F0.wireOp",EDGE,"E21.trimOffspring"),sQuery(id+"F0.wireOp",EDGE,"E22.trimOffspring"),sQuery(id+"F0.wireOp",EDGE,"E23.trimOffspring"),sQuery(id+"F0.wireOp",EDGE,"E24.trimOffspring"),sQuery(id+"F0.wireOp",EDGE,"E25.trimOffspring"),sQuery(id+"F0.wireOp",EDGE,"E26.trimOffspring"),sQuery(id+"F0.wireOp",EDGE,"E27.trimOffspring"),sQuery(id+"F0.wireOp",EDGE,"E28.trimOffspring"),sQuery(id+"F0.wireOp",EDGE,"E29.trimOffspring"),sQuery(id+"F0.wireOp",EDGE,"E30.trimOffspring"),sQuery(id+"F0.wireOp",EDGE,"E31.trimOffspring"),sQuery(id+"F0.wireOp",EDGE,"E32.trimOffspring"),sQuery(id+"F0.wireOp",EDGE,"E33.trimOffspring"),sQuery(id+"F0.wireOp",EDGE,"E34.trimOffspring"),sQuery(id+"F0.wireOp",EDGE,"E35.trimOffspring"),sQuery(id+"F0.wireOp",EDGE,"E36.trimOffspring"),sQuery(id+"F0.wireOp",EDGE,"E37")])]})});
            var Q2;
            Q2=makeQuery(id+"F12.opExtrude","SWEPT_BODY",BODY,{"disambiguationData":[OSD([sQuery(id+"F11.wireOp",EDGE,"E142"),sQuery(id+"F11.wireOp",EDGE,"E143.MirrorCS"),sQuery(id+"F11.wireOp",EDGE,"E144"),sQuery(id+"F11.wireOp",EDGE,"E145")])]});
            var Q3;
            Q3=makeQuery(id+"F12.opExtrude","SWEPT_BODY",BODY,{"disambiguationData":[OSD([sQuery(id+"F11.wireOp",EDGE,"E146.1.0"),sQuery(id+"F11.wireOp",EDGE,"E146.1.1"),sQuery(id+"F11.wireOp",EDGE,"E146.1.2"),sQuery(id+"F11.wireOp",EDGE,"E146.1.3")])]});
            var Q4;
            Q4=makeQuery(id+"F12.opExtrude","SWEPT_BODY",BODY,{"disambiguationData":[OSD([sQuery(id+"F11.wireOp",EDGE,"E146.2.0"),sQuery(id+"F11.wireOp",EDGE,"E146.2.1"),sQuery(id+"F11.wireOp",EDGE,"E146.2.2"),sQuery(id+"F11.wireOp",EDGE,"E146.2.3")])]});
            var Q5;
            Q5=makeQuery(id+"F12.opExtrude","SWEPT_BODY",BODY,{"disambiguationData":[OSD([sQuery(id+"F11.wireOp",EDGE,"E146.3.0"),sQuery(id+"F11.wireOp",EDGE,"E146.3.1"),sQuery(id+"F11.wireOp",EDGE,"E146.3.2"),sQuery(id+"F11.wireOp",EDGE,"E146.3.3")])]});
            var Q6;
            Q6=makeQuery(id+"F12.opExtrude","SWEPT_BODY",BODY,{"disambiguationData":[OSD([sQuery(id+"F11.wireOp",EDGE,"E146.4.0"),sQuery(id+"F11.wireOp",EDGE,"E146.4.1"),sQuery(id+"F11.wireOp",EDGE,"E146.4.2"),sQuery(id+"F11.wireOp",EDGE,"E146.4.3")])]});
            var Q7;
            Q7=makeQuery(id+"F12.opExtrude","SWEPT_BODY",BODY,{"disambiguationData":[OSD([sQuery(id+"F11.wireOp",EDGE,"E146.5.0"),sQuery(id+"F11.wireOp",EDGE,"E146.5.1"),sQuery(id+"F11.wireOp",EDGE,"E146.5.2"),sQuery(id+"F11.wireOp",EDGE,"E146.5.3")])]});
            var Q8;
            Q8=makeQuery(id+"F12.opExtrude","SWEPT_BODY",BODY,{"disambiguationData":[OSD([sQuery(id+"F11.wireOp",EDGE,"E146.6.0"),sQuery(id+"F11.wireOp",EDGE,"E146.6.1"),sQuery(id+"F11.wireOp",EDGE,"E146.6.2"),sQuery(id+"F11.wireOp",EDGE,"E146.6.3")])]});
            var Q9;
            Q9=makeQuery(id+"F12.opExtrude","SWEPT_BODY",BODY,{"disambiguationData":[OSD([sQuery(id+"F11.wireOp",EDGE,"E146.7.0"),sQuery(id+"F11.wireOp",EDGE,"E146.7.1"),sQuery(id+"F11.wireOp",EDGE,"E146.7.2"),sQuery(id+"F11.wireOp",EDGE,"E146.7.3")])]});
            booleanBodies(context, id + "F13", {"operationType" : BooleanOperationType.UNION, "tools" : qUnion([Q0, Q1, Q2, Q3, Q4, Q5, Q6, Q7, Q8, Q9])});
        }
        {
            var Q0;
            {var subQ0=sQuery(id+"F5.wireOp",EDGE,"E98.7.0");var subQ1=sQuery(id+"F5.wireOp",EDGE,"E98.6.0");var subQ2=sQuery(id+"F5.wireOp",EDGE,"E134.trimOffspring");var subQ3=sQuery(id+"F5.wireOp",EDGE,"E98.5.1");var subQ4=sQuery(id+"F5.wireOp",EDGE,"E98.3.0");var subQ5=sQuery(id+"F5.wireOp",EDGE,"E110.trimOffspring");var subQ6=sQuery(id+"F5.wireOp",EDGE,"E98.2.5");var subQ7=sQuery(id+"F5.wireOp",EDGE,"E98.2.0");var subQ8=sQuery(id+"F3.wireOp",EDGE,"E80.trimOffspring");var subQ9=sQuery(id+"F5.wireOp",EDGE,"E102.trimOffspring");var subQ10=sQuery(id+"F5.wireOp",EDGE,"E98.1.5");var subQ11=sQuery(id+"F5.wireOp",EDGE,"E98.4.0");var subQ12=sQuery(id+"F5.wireOp",EDGE,"E118.trimOffspring");var subQ13=sQuery(id+"F5.wireOp",EDGE,"E96.trimOffspring");var subQ14=sQuery(id+"F5.wireOp",EDGE,"E98.8.1");var subQ15=sQuery(id+"F5.wireOp",EDGE,"E94.trimOffspring");var subQ16=sQuery(id+"F5.wireOp",EDGE,"E90");var subQ17=sQuery(id+"F5.wireOp",EDGE,"E98.6.1");var subQ18=sQuery(id+"F3.wireOp",EDGE,"E42");var subQ19=sQuery(id+"F3.wireOp",EDGE,"E85.trimOffspring");var subQ20=sQuery(id+"F3.wireOp",EDGE,"E84.trimOffspring");var subQ21=sQuery(id+"F5.wireOp",EDGE,"E98.8.10");var subQ22=sQuery(id+"F3.wireOp",EDGE,"E83.trimOffspring");var subQ23=sQuery(id+"F3.wireOp",EDGE,"E82.trimOffspring");var subQ24=sQuery(id+"F3.wireOp",EDGE,"E81.trimOffspring");var subQ25=sQuery(id+"F3.wireOp",EDGE,"E79.trimOffspring");var subQ26=sQuery(id+"F3.wireOp",EDGE,"E76.trimOffspring");var subQ27=sQuery(id+"F5.wireOp",EDGE,"E98.7.10");var subQ28=sQuery(id+"F3.wireOp",EDGE,"E71.trimOffspring");var subQ29=sQuery(id+"F3.wireOp",EDGE,"E68.trimOffspring");var subQ30=sQuery(id+"F5.wireOp",EDGE,"E114.trimOffspring");var subQ31=sQuery(id+"F3.wireOp",EDGE,"E67.trimOffspring");var subQ32=sQuery(id+"F5.wireOp",EDGE,"E98.1.0");var subQ33=sQuery(id+"F5.wireOp",EDGE,"E98.7.1");var subQ34=sQuery(id+"F3.wireOp",EDGE,"E50.1.0");var subQ35=sQuery(id+"F3.wireOp",EDGE,"E66.trimOffspring");var subQ36=sQuery(id+"F7.wireOp",EDGE,"E137");var subQ37=sQuery(id+"F3.wireOp",EDGE,"E65.trimOffspring");var subQ38=sQuery(id+"F3.wireOp",EDGE,"E64.trimOffspring");var subQ39=sQuery(id+"F3.wireOp",EDGE,"E63.trimOffspring");var subQ40=sQuery(id+"F3.wireOp",EDGE,"E61.trimOffspring");var subQ41=sQuery(id+"F5.wireOp",EDGE,"E119.trimOffspring");var subQ42=sQuery(id+"F5.wireOp",EDGE,"E98.2.1");var subQ43=sQuery(id+"F3.wireOp",EDGE,"E50.5.0");var subQ44=sQuery(id+"F3.wireOp",EDGE,"E86.trimOffspring");var subQ45=sQuery(id+"F5.wireOp",EDGE,"E98.4.1");var subQ46=sQuery(id+"F3.wireOp",EDGE,"E50.2.5");var subQ47=sQuery(id+"F3.wireOp",EDGE,"E62.trimOffspring");var subQ48=sQuery(id+"F5.wireOp",EDGE,"E98.8.5");var subQ49=sQuery(id+"F3.wireOp",EDGE,"E50.4.10");var subQ50=sQuery(id+"F3.wireOp",EDGE,"E50.4.5");var subQ51=sQuery(id+"F5.wireOp",EDGE,"E98.7.5");var subQ52=sQuery(id+"F3.wireOp",EDGE,"E50.4.1");var subQ53=sQuery(id+"F3.wireOp",EDGE,"E72.trimOffspring");var subQ54=sQuery(id+"F3.wireOp",EDGE,"E50.6.10");var subQ55=sQuery(id+"F5.wireOp",EDGE,"E133.trimOffspring");var subQ56=sQuery(id+"F3.wireOp",EDGE,"E50.8.5");var subQ57=sQuery(id+"F3.wireOp",EDGE,"E50.4.0");var subQ58=sQuery(id+"F5.wireOp",EDGE,"E98.1.10");var subQ59=sQuery(id+"F3.wireOp",EDGE,"E70.trimOffspring");var subQ60=sQuery(id+"F5.wireOp",EDGE,"E101.trimOffspring");var subQ61=sQuery(id+"F3.wireOp",EDGE,"E50.8.1");var subQ62=sQuery(id+"F3.wireOp",EDGE,"E50.3.10");var subQ63=sQuery(id+"F3.wireOp",EDGE,"E50.8.0");var subQ64=sQuery(id+"F3.wireOp",EDGE,"E50.5.1");var subQ65=sQuery(id+"F3.wireOp",EDGE,"E73.trimOffspring");var subQ66=sQuery(id+"F3.wireOp",EDGE,"E50.7.0");var subQ67=sQuery(id+"F3.wireOp",EDGE,"E50.2.10");var subQ68=sQuery(id+"F3.wireOp",EDGE,"E75.trimOffspring");var subQ69=sQuery(id+"F3.wireOp",EDGE,"E50.1.5");var subQ70=sQuery(id+"F3.wireOp",EDGE,"E48.trimOffspring");var subQ71=sQuery(id+"F3.wireOp",EDGE,"E50.2.1");var subQ72=sQuery(id+"F3.wireOp",EDGE,"E47.trimOffspring");var subQ73=sQuery(id+"F3.wireOp",EDGE,"E50.1.10");var subQ74=sQuery(id+"F3.wireOp",EDGE,"E77.trimOffspring");var subQ75=sQuery(id+"F3.wireOp",EDGE,"E78.trimOffspring");var subQ76=sQuery(id+"F3.wireOp",EDGE,"E50.3.5");var subQ77=sQuery(id+"F3.wireOp",EDGE,"E50.2.0");var subQ78=sQuery(id+"F3.wireOp",EDGE,"E52.trimOffspring");var subQ79=sQuery(id+"F5.wireOp",EDGE,"E130.trimOffspring");var subQ80=sQuery(id+"F3.wireOp",EDGE,"E50.1.1");var subQ81=sQuery(id+"F3.wireOp",EDGE,"E50.5.5");var subQ82=sQuery(id+"F5.wireOp",EDGE,"E112.trimOffspring");var subQ83=sQuery(id+"F3.wireOp",EDGE,"E50.3.1");var subQ84=sQuery(id+"F3.wireOp",EDGE,"E50.5.10");var subQ85=sQuery(id+"F3.wireOp",EDGE,"E50.6.0");var subQ86=sQuery(id+"F3.wireOp",EDGE,"E50.7.5");var subQ87=sQuery(id+"F3.wireOp",EDGE,"E69.trimOffspring");var subQ88=sQuery(id+"F5.wireOp",EDGE,"E127.trimOffspring");var subQ89=sQuery(id+"F3.wireOp",EDGE,"E57.trimOffspring");var subQ90=sQuery(id+"F5.wireOp",EDGE,"E111.trimOffspring");var subQ91=sQuery(id+"F5.wireOp",EDGE,"E98.5.0");var subQ92=sQuery(id+"F5.wireOp",EDGE,"E126.trimOffspring");var subQ93=sQuery(id+"F3.wireOp",EDGE,"E50.6.1");var subQ94=sQuery(id+"F3.wireOp",EDGE,"E46.trimOffspring");var subQ95=sQuery(id+"F3.wireOp",EDGE,"E58.trimOffspring");var subQ96=sQuery(id+"F3.wireOp",EDGE,"E59.trimOffspring");var subQ97=sQuery(id+"F5.wireOp",EDGE,"E98.3.1");var subQ98=sQuery(id+"F3.wireOp",EDGE,"E50.6.5");var subQ99=sQuery(id+"F3.wireOp",EDGE,"E50.7.10");var subQ100=sQuery(id+"F5.wireOp",EDGE,"E122.trimOffspring");var subQ101=sQuery(id+"F3.wireOp",EDGE,"E60.trimOffspring");var subQ102=sQuery(id+"F5.wireOp",EDGE,"E106.trimOffspring");var subQ103=sQuery(id+"F3.wireOp",EDGE,"E74.trimOffspring");var subQ104=sQuery(id+"F3.wireOp",EDGE,"E50.3.0");var subQ105=sQuery(id+"F3.wireOp",EDGE,"E50.7.1");var subQ106=sQuery(id+"F3.wireOp",EDGE,"E50.8.10");var subQ107=sQuery(id+"F5.wireOp",EDGE,"E98.1.1");var subQ108=sQuery(id+"F3.wireOp",EDGE,"E51.trimOffspring");var subQ109=sQuery(id+"F3.wireOp",EDGE,"E53.trimOffspring");var subQ110=sQuery(id+"F5.wireOp",EDGE,"E104.trimOffspring");var subQ111=sQuery(id+"F5.wireOp",EDGE,"E98.2.10");var subQ112=sQuery(id+"F5.wireOp",EDGE,"E109.trimOffspring");var subQ113=sQuery(id+"F3.wireOp",EDGE,"E54.trimOffspring");var subQ114=sQuery(id+"F5.wireOp",EDGE,"E117.trimOffspring");var subQ115=sQuery(id+"F5.wireOp",EDGE,"E95.trimOffspring");var subQ116=sQuery(id+"F3.wireOp",EDGE,"E55.trimOffspring");var subQ117=sQuery(id+"F3.wireOp",EDGE,"E56.trimOffspring");var subQ118=sQuery(id+"F5.wireOp",EDGE,"E98.8.0");var subQ119=sQuery(id+"F5.wireOp",EDGE,"E99.trimOffspring");var subQ120=sQuery(id+"F5.wireOp",EDGE,"E100.trimOffspring");var subQ121=sQuery(id+"F5.wireOp",EDGE,"E103.trimOffspring");var subQ122=sQuery(id+"F5.wireOp",EDGE,"E105.trimOffspring");var subQ123=sQuery(id+"F5.wireOp",EDGE,"E107.trimOffspring");var subQ124=sQuery(id+"F5.wireOp",EDGE,"E108.trimOffspring");var subQ125=sQuery(id+"F5.wireOp",EDGE,"E113.trimOffspring");var subQ126=sQuery(id+"F5.wireOp",EDGE,"E115.trimOffspring");var subQ127=sQuery(id+"F5.wireOp",EDGE,"E116.trimOffspring");var subQ128=sQuery(id+"F5.wireOp",EDGE,"E120.trimOffspring");var subQ129=sQuery(id+"F5.wireOp",EDGE,"E121.trimOffspring");var subQ130=sQuery(id+"F5.wireOp",EDGE,"E123.trimOffspring");var subQ131=sQuery(id+"F5.wireOp",EDGE,"E124.trimOffspring");var subQ132=sQuery(id+"F5.wireOp",EDGE,"E125.trimOffspring");var subQ133=sQuery(id+"F5.wireOp",EDGE,"E128.trimOffspring");var subQ134=sQuery(id+"F5.wireOp",EDGE,"E129.trimOffspring");var subQ135=sQuery(id+"F5.wireOp",EDGE,"E131.trimOffspring");var subQ136=sQuery(id+"F5.wireOp",EDGE,"E132.trimOffspring");var subQ137=sQuery(id+"F0.wireOp",EDGE,"E15");var subQ138=sQuery(id+"F0.wireOp",EDGE,"E37");var subQ139=sQuery(id+"F0.wireOp",EDGE,"E36.trimOffspring");var subQ140=sQuery(id+"F0.wireOp",EDGE,"E35.trimOffspring");var subQ141=sQuery(id+"F0.wireOp",EDGE,"E34.trimOffspring");var subQ142=sQuery(id+"F0.wireOp",EDGE,"E33.trimOffspring");var subQ143=sQuery(id+"F0.wireOp",EDGE,"E32.trimOffspring");var subQ144=sQuery(id+"F0.wireOp",EDGE,"E31.trimOffspring");var subQ145=sQuery(id+"F0.wireOp",EDGE,"E30.trimOffspring");var subQ146=sQuery(id+"F0.wireOp",EDGE,"E29.trimOffspring");var subQ147=sQuery(id+"F0.wireOp",EDGE,"E28.trimOffspring");var subQ148=sQuery(id+"F0.wireOp",EDGE,"E27.trimOffspring");var subQ149=sQuery(id+"F0.wireOp",EDGE,"E26.trimOffspring");var subQ150=sQuery(id+"F0.wireOp",EDGE,"E25.trimOffspring");var subQ151=sQuery(id+"F0.wireOp",EDGE,"E24.trimOffspring");var subQ152=sQuery(id+"F0.wireOp",EDGE,"E23.trimOffspring");var subQ153=sQuery(id+"F0.wireOp",EDGE,"E22.trimOffspring");var subQ154=sQuery(id+"F0.wireOp",EDGE,"E21.trimOffspring");var subQ155=sQuery(id+"F0.wireOp",EDGE,"E20.trimOffspring");var subQ156=sQuery(id+"F0.wireOp",EDGE,"E14");var subQ157=sQuery(id+"F0.wireOp",EDGE,"E5");var subQ158=sQuery(id+"F0.wireOp",EDGE,"E8");var subQ159=sQuery(id+"F0.wireOp",EDGE,"E4");var subQ160=sQuery(id+"F0.wireOp",EDGE,"E1");var subQ161=sQuery(id+"F0.wireOp",EDGE,"E2");var subQ162=sQuery(id+"F0.wireOp",EDGE,"E3");var subQ163=sQuery(id+"F0.wireOp",EDGE,"E13.8.7");var subQ164=sQuery(id+"F0.wireOp",EDGE,"E13.8.6");var subQ165=sQuery(id+"F0.wireOp",EDGE,"E13.8.5");var subQ166=sQuery(id+"F0.wireOp",EDGE,"E13.8.2");var subQ167=sQuery(id+"F0.wireOp",EDGE,"E13.8.1");var subQ168=sQuery(id+"F0.wireOp",EDGE,"E13.8.0");var subQ169=sQuery(id+"F0.wireOp",EDGE,"E13.7.7");var subQ170=sQuery(id+"F0.wireOp",EDGE,"E13.7.6");var subQ171=sQuery(id+"F0.wireOp",EDGE,"E13.7.5");var subQ172=sQuery(id+"F0.wireOp",EDGE,"E13.7.2");var subQ173=sQuery(id+"F0.wireOp",EDGE,"E13.7.1");var subQ174=sQuery(id+"F0.wireOp",EDGE,"E13.7.0");var subQ175=sQuery(id+"F0.wireOp",EDGE,"E13.6.7");var subQ176=sQuery(id+"F0.wireOp",EDGE,"E13.6.6");var subQ177=sQuery(id+"F0.wireOp",EDGE,"E13.6.5");var subQ178=sQuery(id+"F0.wireOp",EDGE,"E13.6.2");var subQ179=sQuery(id+"F0.wireOp",EDGE,"E13.6.1");var subQ180=sQuery(id+"F0.wireOp",EDGE,"E13.6.0");var subQ181=sQuery(id+"F0.wireOp",EDGE,"E13.5.7");var subQ182=sQuery(id+"F0.wireOp",EDGE,"E13.5.6");var subQ183=sQuery(id+"F0.wireOp",EDGE,"E13.5.5");var subQ184=sQuery(id+"F0.wireOp",EDGE,"E13.5.2");var subQ185=sQuery(id+"F0.wireOp",EDGE,"E13.5.1");var subQ186=sQuery(id+"F0.wireOp",EDGE,"E13.5.0");var subQ187=sQuery(id+"F0.wireOp",EDGE,"E13.4.7");var subQ188=sQuery(id+"F0.wireOp",EDGE,"E13.4.6");var subQ189=sQuery(id+"F0.wireOp",EDGE,"E13.4.5");var subQ190=sQuery(id+"F0.wireOp",EDGE,"E13.4.2");var subQ191=sQuery(id+"F0.wireOp",EDGE,"E13.4.1");var subQ192=sQuery(id+"F0.wireOp",EDGE,"E13.4.0");var subQ193=sQuery(id+"F0.wireOp",EDGE,"E13.3.7");var subQ194=sQuery(id+"F0.wireOp",EDGE,"E13.3.6");var subQ195=sQuery(id+"F0.wireOp",EDGE,"E13.3.5");var subQ196=sQuery(id+"F0.wireOp",EDGE,"E13.3.2");var subQ197=sQuery(id+"F0.wireOp",EDGE,"E13.3.1");var subQ198=sQuery(id+"F0.wireOp",EDGE,"E13.3.0");var subQ199=sQuery(id+"F0.wireOp",EDGE,"E13.2.7");var subQ200=sQuery(id+"F0.wireOp",EDGE,"E13.2.6");var subQ201=sQuery(id+"F0.wireOp",EDGE,"E13.2.5");var subQ202=sQuery(id+"F0.wireOp",EDGE,"E13.2.2");var subQ203=sQuery(id+"F0.wireOp",EDGE,"E13.2.1");var subQ204=sQuery(id+"F0.wireOp",EDGE,"E13.2.0");var subQ205=sQuery(id+"F0.wireOp",EDGE,"E13.1.7");var subQ206=sQuery(id+"F0.wireOp",EDGE,"E13.1.6");var subQ207=sQuery(id+"F0.wireOp",EDGE,"E13.1.5");var subQ208=sQuery(id+"F0.wireOp",EDGE,"E13.1.2");var subQ209=sQuery(id+"F0.wireOp",EDGE,"E13.1.1");var subQ210=sQuery(id+"F0.wireOp",EDGE,"E13.1.0");var subQ211=sQuery(id+"F0.wireOp",EDGE,"E12.9.11");var subQ212=sQuery(id+"F0.wireOp",EDGE,"E12.9.10");var subQ213=sQuery(id+"F0.wireOp",EDGE,"E12.9.5");var subQ214=sQuery(id+"F0.wireOp",EDGE,"E12.9.4");var subQ215=sQuery(id+"F0.wireOp",EDGE,"E12.9.1");var subQ216=sQuery(id+"F0.wireOp",EDGE,"E12.9.0");var subQ217=sQuery(id+"F0.wireOp",EDGE,"E12.8.11");var subQ218=sQuery(id+"F0.wireOp",EDGE,"E12.8.10");var subQ219=sQuery(id+"F0.wireOp",EDGE,"E12.8.5");var subQ220=sQuery(id+"F0.wireOp",EDGE,"E12.8.4");var subQ221=sQuery(id+"F0.wireOp",EDGE,"E12.8.1");var subQ222=sQuery(id+"F0.wireOp",EDGE,"E12.8.0");var subQ223=sQuery(id+"F0.wireOp",EDGE,"E12.7.11");var subQ224=sQuery(id+"F0.wireOp",EDGE,"E12.7.10");var subQ225=sQuery(id+"F0.wireOp",EDGE,"E12.7.5");var subQ226=sQuery(id+"F0.wireOp",EDGE,"E12.7.4");var subQ227=sQuery(id+"F0.wireOp",EDGE,"E12.7.1");var subQ228=sQuery(id+"F0.wireOp",EDGE,"E12.7.0");var subQ229=sQuery(id+"F0.wireOp",EDGE,"E12.6.11");var subQ230=sQuery(id+"F0.wireOp",EDGE,"E12.6.10");var subQ231=sQuery(id+"F0.wireOp",EDGE,"E12.6.5");var subQ232=sQuery(id+"F0.wireOp",EDGE,"E12.6.4");var subQ233=sQuery(id+"F0.wireOp",EDGE,"E12.6.1");var subQ234=sQuery(id+"F0.wireOp",EDGE,"E12.6.0");var subQ235=sQuery(id+"F0.wireOp",EDGE,"E12.5.11");var subQ236=sQuery(id+"F0.wireOp",EDGE,"E12.5.10");var subQ237=sQuery(id+"F0.wireOp",EDGE,"E12.5.5");var subQ238=sQuery(id+"F0.wireOp",EDGE,"E12.5.4");var subQ239=sQuery(id+"F0.wireOp",EDGE,"E12.5.1");var subQ240=sQuery(id+"F0.wireOp",EDGE,"E12.5.0");var subQ241=sQuery(id+"F0.wireOp",EDGE,"E12.4.11");var subQ242=sQuery(id+"F0.wireOp",EDGE,"E12.4.10");var subQ243=sQuery(id+"F0.wireOp",EDGE,"E12.4.5");var subQ244=sQuery(id+"F0.wireOp",EDGE,"E12.4.4");var subQ245=sQuery(id+"F0.wireOp",EDGE,"E12.4.1");var subQ246=sQuery(id+"F0.wireOp",EDGE,"E12.4.0");var subQ247=sQuery(id+"F0.wireOp",EDGE,"E12.3.11");var subQ248=sQuery(id+"F0.wireOp",EDGE,"E12.3.10");var subQ249=sQuery(id+"F0.wireOp",EDGE,"E12.3.5");var subQ250=sQuery(id+"F0.wireOp",EDGE,"E12.3.4");var subQ251=sQuery(id+"F0.wireOp",EDGE,"E12.3.1");var subQ252=sQuery(id+"F0.wireOp",EDGE,"E12.3.0");var subQ253=sQuery(id+"F0.wireOp",EDGE,"E12.2.11");var subQ254=sQuery(id+"F0.wireOp",EDGE,"E12.2.10");var subQ255=sQuery(id+"F0.wireOp",EDGE,"E12.2.5");var subQ256=sQuery(id+"F0.wireOp",EDGE,"E12.2.4");var subQ257=sQuery(id+"F0.wireOp",EDGE,"E12.2.1");var subQ258=sQuery(id+"F0.wireOp",EDGE,"E12.2.0");var subQ259=sQuery(id+"F0.wireOp",EDGE,"E12.1.11");var subQ260=sQuery(id+"F0.wireOp",EDGE,"E12.1.10");var subQ261=sQuery(id+"F0.wireOp",EDGE,"E12.1.5");var subQ262=sQuery(id+"F0.wireOp",EDGE,"E12.1.4");var subQ263=sQuery(id+"F0.wireOp",EDGE,"E12.1.1");var subQ264=sQuery(id+"F0.wireOp",EDGE,"E12.1.0");var subQ265=makeQuery(id+"F8.boolean.opBoolean","MERGE",FACE,{"derivedFrom":[makeQuery(id+"F6.boolean.opBoolean","MERGE",FACE,{"derivedFrom":[makeQuery(id+"F4.boolean.opBoolean","MERGE",FACE,{"derivedFrom":[makeQuery(id+"F2.opChamfer","SPLIT",FACE,{"disambiguationData":[OD(18.0)],"derivedFrom":makeQuery(id+"F1.opExtrude","CAP_FACE",FACE,{"disambiguationData":[OSD([subQ264,subQ263,sQuery(id+"F0.wireOp",EDGE,"E12.1.2"),sQuery(id+"F0.wireOp",EDGE,"E12.1.3"),subQ262,subQ261,sQuery(id+"F0.wireOp",EDGE,"E12.1.6"),sQuery(id+"F0.wireOp",EDGE,"E12.1.7"),subQ260,subQ259,subQ258,subQ257,sQuery(id+"F0.wireOp",EDGE,"E12.2.2"),sQuery(id+"F0.wireOp",EDGE,"E12.2.3"),subQ256,subQ255,sQuery(id+"F0.wireOp",EDGE,"E12.2.6"),sQuery(id+"F0.wireOp",EDGE,"E12.2.7"),subQ254,subQ253,subQ252,subQ251,sQuery(id+"F0.wireOp",EDGE,"E12.3.2"),sQuery(id+"F0.wireOp",EDGE,"E12.3.3"),subQ250,subQ249,sQuery(id+"F0.wireOp",EDGE,"E12.3.6"),sQuery(id+"F0.wireOp",EDGE,"E12.3.7"),subQ248,subQ247,subQ246,subQ245,sQuery(id+"F0.wireOp",EDGE,"E12.4.2"),sQuery(id+"F0.wireOp",EDGE,"E12.4.3"),subQ244,subQ243,sQuery(id+"F0.wireOp",EDGE,"E12.4.6"),sQuery(id+"F0.wireOp",EDGE,"E12.4.7"),subQ242,subQ241,subQ240,subQ239,sQuery(id+"F0.wireOp",EDGE,"E12.5.2"),sQuery(id+"F0.wireOp",EDGE,"E12.5.3"),subQ238,subQ237,sQuery(id+"F0.wireOp",EDGE,"E12.5.6"),sQuery(id+"F0.wireOp",EDGE,"E12.5.7"),subQ236,subQ235,subQ234,subQ233,sQuery(id+"F0.wireOp",EDGE,"E12.6.2"),sQuery(id+"F0.wireOp",EDGE,"E12.6.3"),subQ232,subQ231,sQuery(id+"F0.wireOp",EDGE,"E12.6.6"),sQuery(id+"F0.wireOp",EDGE,"E12.6.7"),subQ230,subQ229,subQ228,subQ227,sQuery(id+"F0.wireOp",EDGE,"E12.7.2"),sQuery(id+"F0.wireOp",EDGE,"E12.7.3"),subQ226,subQ225,sQuery(id+"F0.wireOp",EDGE,"E12.7.6"),sQuery(id+"F0.wireOp",EDGE,"E12.7.7"),subQ224,subQ223,subQ222,subQ221,sQuery(id+"F0.wireOp",EDGE,"E12.8.2"),sQuery(id+"F0.wireOp",EDGE,"E12.8.3"),subQ220,subQ219,sQuery(id+"F0.wireOp",EDGE,"E12.8.6"),sQuery(id+"F0.wireOp",EDGE,"E12.8.7"),subQ218,subQ217,subQ216,subQ215,sQuery(id+"F0.wireOp",EDGE,"E12.9.2"),sQuery(id+"F0.wireOp",EDGE,"E12.9.3"),subQ214,subQ213,sQuery(id+"F0.wireOp",EDGE,"E12.9.6"),sQuery(id+"F0.wireOp",EDGE,"E12.9.7"),subQ212,subQ211,subQ210,subQ209,subQ208,subQ207,subQ206,subQ205,sQuery(id+"F0.wireOp",EDGE,"E13.1.8"),sQuery(id+"F0.wireOp",EDGE,"E13.1.9"),sQuery(id+"F0.wireOp",EDGE,"E13.1.10"),sQuery(id+"F0.wireOp",EDGE,"E13.1.11"),subQ204,subQ203,subQ202,subQ201,subQ200,subQ199,sQuery(id+"F0.wireOp",EDGE,"E13.2.8"),sQuery(id+"F0.wireOp",EDGE,"E13.2.9"),sQuery(id+"F0.wireOp",EDGE,"E13.2.10"),sQuery(id+"F0.wireOp",EDGE,"E13.2.11"),subQ198,subQ197,subQ196,subQ195,subQ194,subQ193,sQuery(id+"F0.wireOp",EDGE,"E13.3.8"),sQuery(id+"F0.wireOp",EDGE,"E13.3.9"),sQuery(id+"F0.wireOp",EDGE,"E13.3.10"),sQuery(id+"F0.wireOp",EDGE,"E13.3.11"),subQ192,subQ191,subQ190,subQ189,subQ188,subQ187,sQuery(id+"F0.wireOp",EDGE,"E13.4.8"),sQuery(id+"F0.wireOp",EDGE,"E13.4.9"),sQuery(id+"F0.wireOp",EDGE,"E13.4.10"),sQuery(id+"F0.wireOp",EDGE,"E13.4.11"),subQ186,subQ185,subQ184,subQ183,subQ182,subQ181,sQuery(id+"F0.wireOp",EDGE,"E13.5.8"),sQuery(id+"F0.wireOp",EDGE,"E13.5.9"),sQuery(id+"F0.wireOp",EDGE,"E13.5.10"),sQuery(id+"F0.wireOp",EDGE,"E13.5.11"),subQ180,subQ179,subQ178,subQ177,subQ176,subQ175,sQuery(id+"F0.wireOp",EDGE,"E13.6.8"),sQuery(id+"F0.wireOp",EDGE,"E13.6.9"),sQuery(id+"F0.wireOp",EDGE,"E13.6.10"),sQuery(id+"F0.wireOp",EDGE,"E13.6.11"),subQ174,subQ173,subQ172,subQ171,subQ170,subQ169,sQuery(id+"F0.wireOp",EDGE,"E13.7.8"),sQuery(id+"F0.wireOp",EDGE,"E13.7.9"),sQuery(id+"F0.wireOp",EDGE,"E13.7.10"),sQuery(id+"F0.wireOp",EDGE,"E13.7.11"),subQ168,subQ167,subQ166,subQ165,subQ164,subQ163,sQuery(id+"F0.wireOp",EDGE,"E13.8.8"),sQuery(id+"F0.wireOp",EDGE,"E13.8.9"),sQuery(id+"F0.wireOp",EDGE,"E13.8.10"),sQuery(id+"F0.wireOp",EDGE,"E13.8.11"),subQ162,subQ161,subQ160,subQ159,subQ158,subQ157,sQuery(id+"F0.wireOp",EDGE,"E11"),sQuery(id+"F0.wireOp",EDGE,"E6"),sQuery(id+"F0.wireOp",EDGE,"E7"),sQuery(id+"F0.wireOp",EDGE,"E10"),subQ156,subQ137,subQ155,subQ154,subQ153,subQ152,subQ151,subQ150,subQ149,subQ148,subQ147,subQ146,subQ145,subQ144,subQ143,subQ142,subQ141,subQ140,subQ139,subQ138])],"isStart":false})}),makeQuery(id+"F4.opExtrude","CAP_FACE",FACE,{"disambiguationData":[OSD([subQ137,subQ18,sQuery(id+"F3.wireOp",EDGE,"E43.0"),subQ94,subQ72,subQ70,sQuery(id+"F3.wireOp",EDGE,"E49.trimOffspring"),subQ34,subQ80,subQ69,sQuery(id+"F3.wireOp",EDGE,"E50.1.6"),sQuery(id+"F3.wireOp",EDGE,"E50.1.8"),subQ73,subQ77,subQ71,subQ46,sQuery(id+"F3.wireOp",EDGE,"E50.2.6"),sQuery(id+"F3.wireOp",EDGE,"E50.2.8"),subQ67,subQ104,subQ83,subQ76,sQuery(id+"F3.wireOp",EDGE,"E50.3.6"),sQuery(id+"F3.wireOp",EDGE,"E50.3.8"),subQ62,subQ57,subQ52,subQ50,sQuery(id+"F3.wireOp",EDGE,"E50.4.6"),sQuery(id+"F3.wireOp",EDGE,"E50.4.8"),subQ49,subQ43,subQ64,subQ81,sQuery(id+"F3.wireOp",EDGE,"E50.5.6"),sQuery(id+"F3.wireOp",EDGE,"E50.5.8"),subQ84,subQ85,subQ93,subQ98,sQuery(id+"F3.wireOp",EDGE,"E50.6.6"),sQuery(id+"F3.wireOp",EDGE,"E50.6.8"),subQ54,subQ66,subQ105,subQ86,sQuery(id+"F3.wireOp",EDGE,"E50.7.6"),sQuery(id+"F3.wireOp",EDGE,"E50.7.8"),subQ99,subQ63,subQ61,subQ56,sQuery(id+"F3.wireOp",EDGE,"E50.8.6"),sQuery(id+"F3.wireOp",EDGE,"E50.8.8"),subQ106,subQ108,subQ78,subQ109,subQ113,subQ116,subQ117,subQ89,subQ95,subQ96,subQ101,subQ40,subQ47,subQ39,subQ38,subQ37,subQ35,subQ31,subQ29,subQ87,subQ59,subQ28,subQ53,subQ65,subQ103,subQ68,subQ26,subQ74,subQ75,subQ25,subQ8,subQ24,subQ23,subQ22,subQ20,subQ19,subQ44])],"isStart":false})]}),makeQuery(id+"F6.opExtrude","CAP_FACE",FACE,{"disambiguationData":[OSD([sQuery(id+"F5.wireOp",EDGE,"E88"),sQuery(id+"F5.wireOp",EDGE,"E89"),subQ16,sQuery(id+"F5.wireOp",EDGE,"E91.0"),sQuery(id+"F5.wireOp",EDGE,"E92"),sQuery(id+"F5.wireOp",EDGE,"E93"),subQ15,subQ115,subQ13,sQuery(id+"F5.wireOp",EDGE,"E97.trimOffspring"),subQ32,subQ107,subQ10,sQuery(id+"F5.wireOp",EDGE,"E98.1.6"),sQuery(id+"F5.wireOp",EDGE,"E98.1.7"),sQuery(id+"F5.wireOp",EDGE,"E98.1.8"),sQuery(id+"F5.wireOp",EDGE,"E98.1.9"),subQ58,subQ7,subQ42,subQ6,sQuery(id+"F5.wireOp",EDGE,"E98.2.6"),sQuery(id+"F5.wireOp",EDGE,"E98.2.7"),sQuery(id+"F5.wireOp",EDGE,"E98.2.8"),sQuery(id+"F5.wireOp",EDGE,"E98.2.9"),subQ111,subQ4,subQ97,sQuery(id+"F5.wireOp",EDGE,"E98.3.5"),sQuery(id+"F5.wireOp",EDGE,"E98.3.6"),sQuery(id+"F5.wireOp",EDGE,"E98.3.7"),sQuery(id+"F5.wireOp",EDGE,"E98.3.8"),sQuery(id+"F5.wireOp",EDGE,"E98.3.9"),sQuery(id+"F5.wireOp",EDGE,"E98.3.10"),subQ11,subQ45,sQuery(id+"F5.wireOp",EDGE,"E98.4.5"),sQuery(id+"F5.wireOp",EDGE,"E98.4.6"),sQuery(id+"F5.wireOp",EDGE,"E98.4.7"),sQuery(id+"F5.wireOp",EDGE,"E98.4.8"),sQuery(id+"F5.wireOp",EDGE,"E98.4.9"),sQuery(id+"F5.wireOp",EDGE,"E98.4.10"),subQ91,subQ3,sQuery(id+"F5.wireOp",EDGE,"E98.5.5"),sQuery(id+"F5.wireOp",EDGE,"E98.5.6"),sQuery(id+"F5.wireOp",EDGE,"E98.5.7"),sQuery(id+"F5.wireOp",EDGE,"E98.5.8"),sQuery(id+"F5.wireOp",EDGE,"E98.5.9"),sQuery(id+"F5.wireOp",EDGE,"E98.5.10"),subQ1,subQ17,sQuery(id+"F5.wireOp",EDGE,"E98.6.5"),sQuery(id+"F5.wireOp",EDGE,"E98.6.6"),sQuery(id+"F5.wireOp",EDGE,"E98.6.7"),sQuery(id+"F5.wireOp",EDGE,"E98.6.8"),sQuery(id+"F5.wireOp",EDGE,"E98.6.9"),sQuery(id+"F5.wireOp",EDGE,"E98.6.10"),subQ0,subQ33,subQ51,sQuery(id+"F5.wireOp",EDGE,"E98.7.6"),sQuery(id+"F5.wireOp",EDGE,"E98.7.7"),sQuery(id+"F5.wireOp",EDGE,"E98.7.8"),sQuery(id+"F5.wireOp",EDGE,"E98.7.9"),subQ27,subQ118,subQ14,subQ48,sQuery(id+"F5.wireOp",EDGE,"E98.8.6"),sQuery(id+"F5.wireOp",EDGE,"E98.8.7"),sQuery(id+"F5.wireOp",EDGE,"E98.8.8"),sQuery(id+"F5.wireOp",EDGE,"E98.8.9"),subQ21,subQ119,subQ120,subQ60,subQ9,subQ121,subQ110,subQ122,subQ102,subQ123,subQ124,subQ112,subQ5,subQ90,subQ82,subQ125,subQ30,subQ126,subQ127,subQ114,subQ12,subQ41,subQ128,subQ129,subQ100,subQ130,subQ131,subQ132,subQ92,subQ88,subQ133,subQ134,subQ79,subQ135,subQ136,subQ55,subQ2])],"isStart":true})]}),makeQuery(id+"F8.opExtrude","CAP_FACE",FACE,{"disambiguationData":[OSD([sQuery(id+"F7.wireOp",EDGE,"E135"),subQ36])],"isStart":true})]});Q0=makeQuery(id+"F13.opBoolean","MERGE",FACE,{"derivedFrom":[makeQuery(id+"F10.boolean.opBoolean","SPLIT",FACE,{"disambiguationData":[TD([makeQuery(id+"F1.opExtrude","SWEPT_FACE",FACE,{"disambiguationData":[OSD([subQ262])]})])],"derivedFrom":subQ265}),makeQuery(id+"F10.boolean.opBoolean","SPLIT",FACE,{"disambiguationData":[TD([makeQuery(id+"F4.opExtrude","SWEPT_FACE",FACE,{"disambiguationData":[OSD([subQ18])]})])],"derivedFrom":subQ265}),makeQuery(id+"F12.opExtrude","CAP_FACE",FACE,{"disambiguationData":[OSD([sQuery(id+"F11.wireOp",EDGE,"E142"),sQuery(id+"F11.wireOp",EDGE,"E143.MirrorCS"),sQuery(id+"F11.wireOp",EDGE,"E144"),sQuery(id+"F11.wireOp",EDGE,"E145")])],"isStart":true}),makeQuery(id+"F12.opExtrude","CAP_FACE",FACE,{"disambiguationData":[OSD([sQuery(id+"F11.wireOp",EDGE,"E146.1.0"),sQuery(id+"F11.wireOp",EDGE,"E146.1.1"),sQuery(id+"F11.wireOp",EDGE,"E146.1.2"),sQuery(id+"F11.wireOp",EDGE,"E146.1.3")])],"isStart":true}),makeQuery(id+"F12.opExtrude","CAP_FACE",FACE,{"disambiguationData":[OSD([sQuery(id+"F11.wireOp",EDGE,"E146.2.0"),sQuery(id+"F11.wireOp",EDGE,"E146.2.1"),sQuery(id+"F11.wireOp",EDGE,"E146.2.2"),sQuery(id+"F11.wireOp",EDGE,"E146.2.3")])],"isStart":true}),makeQuery(id+"F12.opExtrude","CAP_FACE",FACE,{"disambiguationData":[OSD([sQuery(id+"F11.wireOp",EDGE,"E146.3.0"),sQuery(id+"F11.wireOp",EDGE,"E146.3.1"),sQuery(id+"F11.wireOp",EDGE,"E146.3.2"),sQuery(id+"F11.wireOp",EDGE,"E146.3.3")])],"isStart":true}),makeQuery(id+"F12.opExtrude","CAP_FACE",FACE,{"disambiguationData":[OSD([sQuery(id+"F11.wireOp",EDGE,"E146.4.0"),sQuery(id+"F11.wireOp",EDGE,"E146.4.1"),sQuery(id+"F11.wireOp",EDGE,"E146.4.2"),sQuery(id+"F11.wireOp",EDGE,"E146.4.3")])],"isStart":true}),makeQuery(id+"F12.opExtrude","CAP_FACE",FACE,{"disambiguationData":[OSD([sQuery(id+"F11.wireOp",EDGE,"E146.5.0"),sQuery(id+"F11.wireOp",EDGE,"E146.5.1"),sQuery(id+"F11.wireOp",EDGE,"E146.5.2"),sQuery(id+"F11.wireOp",EDGE,"E146.5.3")])],"isStart":true}),makeQuery(id+"F12.opExtrude","CAP_FACE",FACE,{"disambiguationData":[OSD([sQuery(id+"F11.wireOp",EDGE,"E146.6.0"),sQuery(id+"F11.wireOp",EDGE,"E146.6.1"),sQuery(id+"F11.wireOp",EDGE,"E146.6.2"),sQuery(id+"F11.wireOp",EDGE,"E146.6.3")])],"isStart":true}),makeQuery(id+"F12.opExtrude","CAP_FACE",FACE,{"disambiguationData":[OSD([sQuery(id+"F11.wireOp",EDGE,"E146.7.0"),sQuery(id+"F11.wireOp",EDGE,"E146.7.1"),sQuery(id+"F11.wireOp",EDGE,"E146.7.2"),sQuery(id+"F11.wireOp",EDGE,"E146.7.3")])],"isStart":true})]});}
            var sketch = newSketch(context, id + "F14", { "sketchPlane" : qUnion([Q0])});
            skCircle(sketch, "E147", {"center": v(0, 0) * mm, "radius": 4.03 * mm});
            skSolve(sketch);
        }
        {
            var Q0;
            Q0=makeQuery(id+"F14.imprint","IMPRINT",FACE,{"disambiguationData":[TD([[makeQuery(id+"F14.imprint","IMPRINT",EDGE,{"derivedFrom":sQuery(id+"F14.wireOp",EDGE,"E147")}),1.0]])]});
            extrude(context, id + "F15", {"entities" : qUnion([Q0]), "operationType" : NewBodyOperationType.REMOVE, "oppositeDirection" : true, "depth" : 25.4 * mm});
        }
    });
